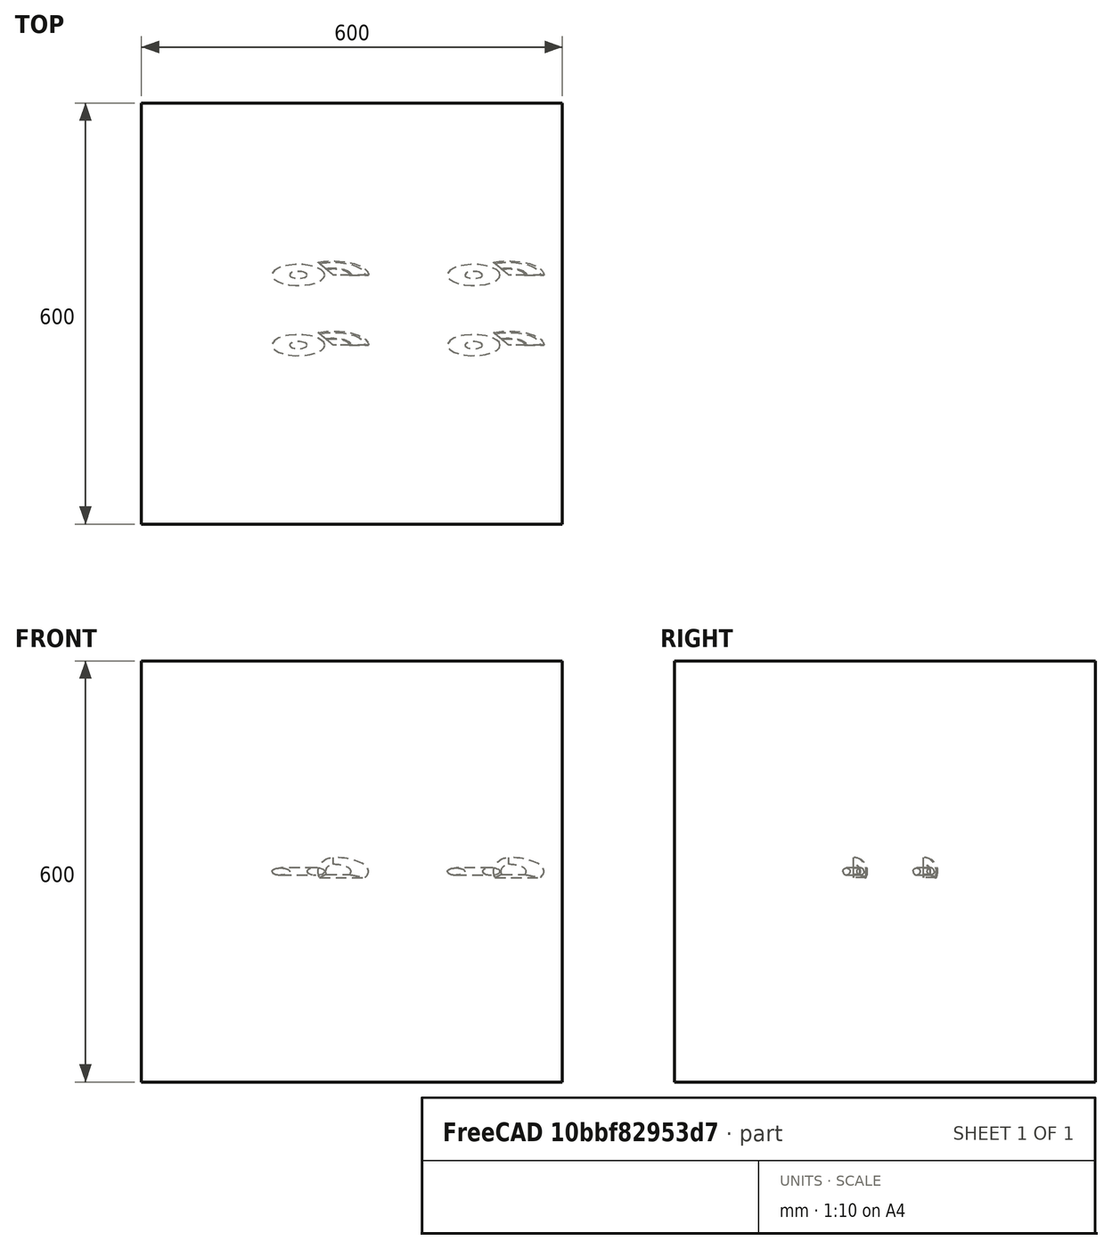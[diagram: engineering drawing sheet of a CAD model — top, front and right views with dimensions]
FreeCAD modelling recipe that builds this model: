
FCSTD DOCUMENT  (FreeCAD 0.19RUnknown)
Label: arrayTest-6_scaled
License: All rights reserved
LicenseURL: http://en.wikipedia.org/wiki/All_rights_reserved
objects: App::DocumentObjectGroupPython×1248, Part::FeaturePython×5, App::Part×2, Part::MultiFuse×1
note: 6 computed .brp shape members not serialized (recipe doc carries the construction recipe); baked Part::Feature solids carry a one-line shape summary decoded from their .brp

FEATURE [App::DocumentObjectGroupPython] HALFPI  # scripted group (container) (typed FeaturePython)
  name = HALFPI
  value = pi/2.
FEATURE [App::DocumentObjectGroupPython] PI  # scripted group (container) (typed FeaturePython)
  name = PI
  value = 1.*pi
FEATURE [App::DocumentObjectGroupPython] TWOPI  # scripted group (container) (typed FeaturePython)
  name = TWOPI
  value = 2.*pi
FEATURE [App::DocumentObjectGroupPython] Constants  # scripted group (container) (typed FeaturePython)
  Group = -> [HALFPI,PI,TWOPI]
FEATURE [App::DocumentObjectGroupPython] Variables  # scripted group (container) (typed FeaturePython)
FEATURE [App::DocumentObjectGroupPython] Quantities  # scripted group (container) (typed FeaturePython)
FEATURE [App::DocumentObjectGroupPython] Isotopes  # scripted group (container) (typed FeaturePython)
FEATURE [App::DocumentObjectGroupPython] Elements  # scripted group (container) (typed FeaturePython)
FEATURE [App::DocumentObjectGroupPython] G4Isotopes  # scripted group (container) (typed FeaturePython)
FEATURE [App::DocumentObjectGroupPython] H_element  # scripted group (container) (typed FeaturePython)
  Z = 1
  atom_value = 1.008
  formula = H
  name = H_element
FEATURE [App::DocumentObjectGroupPython] He_element  # scripted group (container) (typed FeaturePython)
  Z = 2
  atom_value = 4.0026
  formula = He
  name = He_element
FEATURE [App::DocumentObjectGroupPython] Li_element  # scripted group (container) (typed FeaturePython)
  Z = 3
  atom_value = 6.94
  formula = Li
  name = Li_element
FEATURE [App::DocumentObjectGroupPython] Be_element  # scripted group (container) (typed FeaturePython)
  Z = 4
  atom_value = 9.01218
  formula = Be
  name = Be_element
FEATURE [App::DocumentObjectGroupPython] B_element  # scripted group (container) (typed FeaturePython)
  Z = 5
  atom_value = 10.81
  formula = B
  name = B_element
FEATURE [App::DocumentObjectGroupPython] C_element  # scripted group (container) (typed FeaturePython)
  Z = 6
  atom_value = 12.011
  formula = C
  name = C_element
FEATURE [App::DocumentObjectGroupPython] N_element  # scripted group (container) (typed FeaturePython)
  Z = 7
  atom_value = 14.007
  formula = N
  name = N_element
FEATURE [App::DocumentObjectGroupPython] O_element  # scripted group (container) (typed FeaturePython)
  Z = 8
  atom_value = 15.999
  formula = O
  name = O_element
FEATURE [App::DocumentObjectGroupPython] F_element  # scripted group (container) (typed FeaturePython)
  Z = 9
  atom_value = 18.9984
  formula = F
  name = F_element
FEATURE [App::DocumentObjectGroupPython] Ne_element  # scripted group (container) (typed FeaturePython)
  Z = 10
  atom_value = 20.1797
  formula = Ne
  name = Ne_element
FEATURE [App::DocumentObjectGroupPython] Na_element  # scripted group (container) (typed FeaturePython)
  Z = 11
  atom_value = 22.9898
  formula = Na
  name = Na_element
FEATURE [App::DocumentObjectGroupPython] Mg_element  # scripted group (container) (typed FeaturePython)
  Z = 12
  atom_value = 24.305
  formula = Mg
  name = Mg_element
FEATURE [App::DocumentObjectGroupPython] Al_element  # scripted group (container) (typed FeaturePython)
  Z = 13
  atom_value = 26.9815
  formula = Al
  name = Al_element
FEATURE [App::DocumentObjectGroupPython] Si_element  # scripted group (container) (typed FeaturePython)
  Z = 14
  atom_value = 28.085
  formula = Si
  name = Si_element
FEATURE [App::DocumentObjectGroupPython] P_element  # scripted group (container) (typed FeaturePython)
  Z = 15
  atom_value = 30.9738
  formula = P
  name = P_element
FEATURE [App::DocumentObjectGroupPython] S_element  # scripted group (container) (typed FeaturePython)
  Z = 16
  atom_value = 32.06
  formula = S
  name = S_element
FEATURE [App::DocumentObjectGroupPython] Cl_element  # scripted group (container) (typed FeaturePython)
  Z = 17
  atom_value = 35.45
  formula = Cl
  name = Cl_element
FEATURE [App::DocumentObjectGroupPython] Ar_element  # scripted group (container) (typed FeaturePython)
  Z = 18
  atom_value = 39.95
  formula = Ar
  name = Ar_element
FEATURE [App::DocumentObjectGroupPython] K_element  # scripted group (container) (typed FeaturePython)
  Z = 19
  atom_value = 39.0983
  formula = K
  name = K_element
FEATURE [App::DocumentObjectGroupPython] Ca_element  # scripted group (container) (typed FeaturePython)
  Z = 20
  atom_value = 40.078
  formula = Ca
  name = Ca_element
FEATURE [App::DocumentObjectGroupPython] Sc_element  # scripted group (container) (typed FeaturePython)
  Z = 21
  atom_value = 44.9559
  formula = Sc
  name = Sc_element
FEATURE [App::DocumentObjectGroupPython] Ti_element  # scripted group (container) (typed FeaturePython)
  Z = 22
  atom_value = 47.867
  formula = Ti
  name = Ti_element
FEATURE [App::DocumentObjectGroupPython] V_element  # scripted group (container) (typed FeaturePython)
  Z = 23
  atom_value = 50.9415
  formula = V
  name = V_element
FEATURE [App::DocumentObjectGroupPython] Cr_element  # scripted group (container) (typed FeaturePython)
  Z = 24
  atom_value = 51.9961
  formula = Cr
  name = Cr_element
FEATURE [App::DocumentObjectGroupPython] Mn_element  # scripted group (container) (typed FeaturePython)
  Z = 25
  atom_value = 54.938
  formula = Mn
  name = Mn_element
FEATURE [App::DocumentObjectGroupPython] Fe_element  # scripted group (container) (typed FeaturePython)
  Z = 26
  atom_value = 55.845
  formula = Fe
  name = Fe_element
FEATURE [App::DocumentObjectGroupPython] Co_element  # scripted group (container) (typed FeaturePython)
  Z = 27
  atom_value = 58.9332
  formula = Co
  name = Co_element
FEATURE [App::DocumentObjectGroupPython] Ni_element  # scripted group (container) (typed FeaturePython)
  Z = 28
  atom_value = 58.6934
  formula = Ni
  name = Ni_element
FEATURE [App::DocumentObjectGroupPython] Cu_element  # scripted group (container) (typed FeaturePython)
  Z = 29
  atom_value = 63.546
  formula = Cu
  name = Cu_element
FEATURE [App::DocumentObjectGroupPython] Zn_element  # scripted group (container) (typed FeaturePython)
  Z = 30
  atom_value = 65.38
  formula = Zn
  name = Zn_element
FEATURE [App::DocumentObjectGroupPython] Ga_element  # scripted group (container) (typed FeaturePython)
  Z = 31
  atom_value = 69.723
  formula = Ga
  name = Ga_element
FEATURE [App::DocumentObjectGroupPython] Ge_element  # scripted group (container) (typed FeaturePython)
  Z = 32
  atom_value = 72.63
  formula = Ge
  name = Ge_element
FEATURE [App::DocumentObjectGroupPython] As_element  # scripted group (container) (typed FeaturePython)
  Z = 33
  atom_value = 74.9216
  formula = As
  name = As_element
FEATURE [App::DocumentObjectGroupPython] Se_element  # scripted group (container) (typed FeaturePython)
  Z = 34
  atom_value = 78.971
  formula = Se
  name = Se_element
FEATURE [App::DocumentObjectGroupPython] Br_element  # scripted group (container) (typed FeaturePython)
  Z = 35
  atom_value = 79.904
  formula = Br
  name = Br_element
FEATURE [App::DocumentObjectGroupPython] Kr_element  # scripted group (container) (typed FeaturePython)
  Z = 36
  atom_value = 83.798
  formula = Kr
  name = Kr_element
FEATURE [App::DocumentObjectGroupPython] Rb_element  # scripted group (container) (typed FeaturePython)
  Z = 37
  atom_value = 85.4678
  formula = Rb
  name = Rb_element
FEATURE [App::DocumentObjectGroupPython] Sr_element  # scripted group (container) (typed FeaturePython)
  Z = 38
  atom_value = 87.62
  formula = Sr
  name = Sr_element
FEATURE [App::DocumentObjectGroupPython] Y_element  # scripted group (container) (typed FeaturePython)
  Z = 39
  atom_value = 88.9058
  formula = Y
  name = Y_element
FEATURE [App::DocumentObjectGroupPython] Zr_element  # scripted group (container) (typed FeaturePython)
  Z = 40
  atom_value = 91.224
  formula = Zr
  name = Zr_element
FEATURE [App::DocumentObjectGroupPython] Nb_element  # scripted group (container) (typed FeaturePython)
  Z = 41
  atom_value = 92.9064
  formula = Nb
  name = Nb_element
FEATURE [App::DocumentObjectGroupPython] Mo_element  # scripted group (container) (typed FeaturePython)
  Z = 42
  atom_value = 95.95
  formula = Mo
  name = Mo_element
FEATURE [App::DocumentObjectGroupPython] Tc_element  # scripted group (container) (typed FeaturePython)
  Z = 43
  atom_value = 97
  formula = Tc
  name = Tc_element
FEATURE [App::DocumentObjectGroupPython] Ru_element  # scripted group (container) (typed FeaturePython)
  Z = 44
  atom_value = 101.07
  formula = Ru
  name = Ru_element
FEATURE [App::DocumentObjectGroupPython] Rh_element  # scripted group (container) (typed FeaturePython)
  Z = 45
  atom_value = 102.905
  formula = Rh
  name = Rh_element
FEATURE [App::DocumentObjectGroupPython] Pd_element  # scripted group (container) (typed FeaturePython)
  Z = 46
  atom_value = 106.42
  formula = Pd
  name = Pd_element
FEATURE [App::DocumentObjectGroupPython] Ag_element  # scripted group (container) (typed FeaturePython)
  Z = 47
  atom_value = 107.868
  formula = Ag
  name = Ag_element
FEATURE [App::DocumentObjectGroupPython] Cd_element  # scripted group (container) (typed FeaturePython)
  Z = 48
  atom_value = 112.414
  formula = Cd
  name = Cd_element
FEATURE [App::DocumentObjectGroupPython] In_element  # scripted group (container) (typed FeaturePython)
  Z = 49
  atom_value = 114.818
  formula = In
  name = In_element
FEATURE [App::DocumentObjectGroupPython] Sn_element  # scripted group (container) (typed FeaturePython)
  Z = 50
  atom_value = 118.71
  formula = Sn
  name = Sn_element
FEATURE [App::DocumentObjectGroupPython] Sb_element  # scripted group (container) (typed FeaturePython)
  Z = 51
  atom_value = 121.76
  formula = Sb
  name = Sb_element
FEATURE [App::DocumentObjectGroupPython] Te_element  # scripted group (container) (typed FeaturePython)
  Z = 52
  atom_value = 127.6
  formula = Te
  name = Te_element
FEATURE [App::DocumentObjectGroupPython] I_element  # scripted group (container) (typed FeaturePython)
  Z = 53
  atom_value = 126.904
  formula = I
  name = I_element
FEATURE [App::DocumentObjectGroupPython] Xe_element  # scripted group (container) (typed FeaturePython)
  Z = 54
  atom_value = 131.293
  formula = Xe
  name = Xe_element
FEATURE [App::DocumentObjectGroupPython] Cs_element  # scripted group (container) (typed FeaturePython)
  Z = 55
  atom_value = 132.905
  formula = Cs
  name = Cs_element
FEATURE [App::DocumentObjectGroupPython] Ba_element  # scripted group (container) (typed FeaturePython)
  Z = 56
  atom_value = 137.327
  formula = Ba
  name = Ba_element
FEATURE [App::DocumentObjectGroupPython] La_element  # scripted group (container) (typed FeaturePython)
  Z = 57
  atom_value = 138.905
  formula = La
  name = La_element
FEATURE [App::DocumentObjectGroupPython] Ce_element  # scripted group (container) (typed FeaturePython)
  Z = 58
  atom_value = 140.116
  formula = Ce
  name = Ce_element
FEATURE [App::DocumentObjectGroupPython] Pr_element  # scripted group (container) (typed FeaturePython)
  Z = 59
  atom_value = 140.908
  formula = Pr
  name = Pr_element
FEATURE [App::DocumentObjectGroupPython] Nd_element  # scripted group (container) (typed FeaturePython)
  Z = 60
  atom_value = 144.242
  formula = Nd
  name = Nd_element
FEATURE [App::DocumentObjectGroupPython] Pm_element  # scripted group (container) (typed FeaturePython)
  Z = 61
  atom_value = 145
  formula = Pm
  name = Pm_element
FEATURE [App::DocumentObjectGroupPython] Sm_element  # scripted group (container) (typed FeaturePython)
  Z = 62
  atom_value = 150.36
  formula = Sm
  name = Sm_element
FEATURE [App::DocumentObjectGroupPython] Eu_element  # scripted group (container) (typed FeaturePython)
  Z = 63
  atom_value = 151.964
  formula = Eu
  name = Eu_element
FEATURE [App::DocumentObjectGroupPython] Gd_element  # scripted group (container) (typed FeaturePython)
  Z = 64
  atom_value = 157.25
  formula = Gd
  name = Gd_element
FEATURE [App::DocumentObjectGroupPython] Tb_element  # scripted group (container) (typed FeaturePython)
  Z = 65
  atom_value = 158.925
  formula = Tb
  name = Tb_element
FEATURE [App::DocumentObjectGroupPython] Dy_element  # scripted group (container) (typed FeaturePython)
  Z = 66
  atom_value = 162.5
  formula = Dy
  name = Dy_element
FEATURE [App::DocumentObjectGroupPython] Ho_element  # scripted group (container) (typed FeaturePython)
  Z = 67
  atom_value = 164.93
  formula = Ho
  name = Ho_element
FEATURE [App::DocumentObjectGroupPython] Er_element  # scripted group (container) (typed FeaturePython)
  Z = 68
  atom_value = 167.259
  formula = Er
  name = Er_element
FEATURE [App::DocumentObjectGroupPython] Tm_element  # scripted group (container) (typed FeaturePython)
  Z = 69
  atom_value = 168.934
  formula = Tm
  name = Tm_element
FEATURE [App::DocumentObjectGroupPython] Yb_element  # scripted group (container) (typed FeaturePython)
  Z = 70
  atom_value = 173.045
  formula = Yb
  name = Yb_element
FEATURE [App::DocumentObjectGroupPython] Lu_element  # scripted group (container) (typed FeaturePython)
  Z = 71
  atom_value = 174.967
  formula = Lu
  name = Lu_element
FEATURE [App::DocumentObjectGroupPython] Hf_element  # scripted group (container) (typed FeaturePython)
  Z = 72
  atom_value = 178.49
  formula = Hf
  name = Hf_element
FEATURE [App::DocumentObjectGroupPython] Ta_element  # scripted group (container) (typed FeaturePython)
  Z = 73
  atom_value = 180.948
  formula = Ta
  name = Ta_element
FEATURE [App::DocumentObjectGroupPython] W_element  # scripted group (container) (typed FeaturePython)
  Z = 74
  atom_value = 183.84
  formula = W
  name = W_element
FEATURE [App::DocumentObjectGroupPython] Re_element  # scripted group (container) (typed FeaturePython)
  Z = 75
  atom_value = 186.207
  formula = Re
  name = Re_element
FEATURE [App::DocumentObjectGroupPython] Os_element  # scripted group (container) (typed FeaturePython)
  Z = 76
  atom_value = 190.23
  formula = Os
  name = Os_element
FEATURE [App::DocumentObjectGroupPython] Ir_element  # scripted group (container) (typed FeaturePython)
  Z = 77
  atom_value = 192.217
  formula = Ir
  name = Ir_element
FEATURE [App::DocumentObjectGroupPython] Pt_element  # scripted group (container) (typed FeaturePython)
  Z = 78
  atom_value = 195.084
  formula = Pt
  name = Pt_element
FEATURE [App::DocumentObjectGroupPython] Au_element  # scripted group (container) (typed FeaturePython)
  Z = 79
  atom_value = 196.967
  formula = Au
  name = Au_element
FEATURE [App::DocumentObjectGroupPython] Hg_element  # scripted group (container) (typed FeaturePython)
  Z = 80
  atom_value = 200.592
  formula = Hg
  name = Hg_element
FEATURE [App::DocumentObjectGroupPython] Tl_element  # scripted group (container) (typed FeaturePython)
  Z = 81
  atom_value = 204.38
  formula = Tl
  name = Tl_element
FEATURE [App::DocumentObjectGroupPython] Pb_element  # scripted group (container) (typed FeaturePython)
  Z = 82
  atom_value = 207.2
  formula = Pb
  name = Pb_element
FEATURE [App::DocumentObjectGroupPython] Bi_element  # scripted group (container) (typed FeaturePython)
  Z = 83
  atom_value = 208.98
  formula = Bi
  name = Bi_element
FEATURE [App::DocumentObjectGroupPython] Po_element  # scripted group (container) (typed FeaturePython)
  Z = 84
  atom_value = 209
  formula = Po
  name = Po_element
FEATURE [App::DocumentObjectGroupPython] At_element  # scripted group (container) (typed FeaturePython)
  Z = 85
  atom_value = 210
  formula = At
  name = At_element
FEATURE [App::DocumentObjectGroupPython] Rn_element  # scripted group (container) (typed FeaturePython)
  Z = 86
  atom_value = 222
  formula = Rn
  name = Rn_element
FEATURE [App::DocumentObjectGroupPython] Fr_element  # scripted group (container) (typed FeaturePython)
  Z = 87
  atom_value = 223
  formula = Fr
  name = Fr_element
FEATURE [App::DocumentObjectGroupPython] Ra_element  # scripted group (container) (typed FeaturePython)
  Z = 88
  atom_value = 226
  formula = Ra
  name = Ra_element
FEATURE [App::DocumentObjectGroupPython] Ac_element  # scripted group (container) (typed FeaturePython)
  Z = 89
  atom_value = 227
  formula = Ac
  name = Ac_element
FEATURE [App::DocumentObjectGroupPython] Th_element  # scripted group (container) (typed FeaturePython)
  Z = 90
  atom_value = 232.038
  formula = Th
  name = Th_element
FEATURE [App::DocumentObjectGroupPython] Pa_element  # scripted group (container) (typed FeaturePython)
  Z = 91
  atom_value = 231.036
  formula = Pa
  name = Pa_element
FEATURE [App::DocumentObjectGroupPython] U_element  # scripted group (container) (typed FeaturePython)
  Z = 92
  atom_value = 238.029
  formula = U
  name = U_element
FEATURE [App::DocumentObjectGroupPython] Np_element  # scripted group (container) (typed FeaturePython)
  Z = 93
  atom_value = 237
  formula = Np
  name = Np_element
FEATURE [App::DocumentObjectGroupPython] Pu_element  # scripted group (container) (typed FeaturePython)
  Z = 94
  atom_value = 244
  formula = Pu
  name = Pu_element
FEATURE [App::DocumentObjectGroupPython] Am_element  # scripted group (container) (typed FeaturePython)
  Z = 95
  atom_value = 243
  formula = Am
  name = Am_element
FEATURE [App::DocumentObjectGroupPython] Cm_element  # scripted group (container) (typed FeaturePython)
  Z = 96
  atom_value = 247
  formula = Cm
  name = Cm_element
FEATURE [App::DocumentObjectGroupPython] Bk_element  # scripted group (container) (typed FeaturePython)
  Z = 97
  atom_value = 247
  formula = Bk
  name = Bk_element
FEATURE [App::DocumentObjectGroupPython] Cf_element  # scripted group (container) (typed FeaturePython)
  Z = 98
  atom_value = 251
  formula = Cf
  name = Cf_element
FEATURE [App::DocumentObjectGroupPython] G4Elements  # scripted group (container) (typed FeaturePython)
  Group = -> [H_element,He_element,Li_element,Be_element,B_element,C_element,N_element,O_element,F_element,Ne_element,Na_element,Mg_element,Al_element,Si_element,P_element,S_element,Cl_element,Ar_element,K_element,Ca_element,Sc_element,Ti_element,V_element,Cr_element,Mn_element,Fe_element,Co_element,Ni_element,Cu_element,Zn_element,Ga_element,Ge_element,As_element,Se_element,Br_element,Kr_element,Rb_element,+61 more]
FEATURE [App::DocumentObjectGroupPython] H_element001  label="H_element : 0.101"  # scripted group (container) (typed FeaturePython)
  n = 0.101327
FEATURE [App::DocumentObjectGroupPython] C_element001  label="C_element : 0.775"  # scripted group (container) (typed FeaturePython)
  n = 0.7755
FEATURE [App::DocumentObjectGroupPython] N_element001  label="N_element : 0.035"  # scripted group (container) (typed FeaturePython)
  n = 0.035057
FEATURE [App::DocumentObjectGroupPython] O_element001  label="O_element : 0.052"  # scripted group (container) (typed FeaturePython)
  n = 0.0523159
FEATURE [App::DocumentObjectGroupPython] F_element001  label="F_element : 0.017"  # scripted group (container) (typed FeaturePython)
  n = 0.017422
FEATURE [App::DocumentObjectGroupPython] Ca_element001  label="Ca_element : 0.018"  # scripted group (container) (typed FeaturePython)
  n = 0.018378
FEATURE [App::DocumentObjectGroupPython] G4_A_150_TISSUE  label="G4_A-150_TISSUE"  # scripted group (container) (typed FeaturePython)
  Dunit = g/cm3
  Dvalue = 1.127
  Group = -> [H_element001,C_element001,N_element001,O_element001,F_element001,Ca_element001]
  conduct = 2
  density = 1
  expand = 3
  formula = G4_A-150_TISSUE
  name = G4_A-150_TISSUE
  specific = 4
FEATURE [App::DocumentObjectGroupPython] C_element002  label="C_element : 3"  # scripted group (container) (typed FeaturePython)
  n = 3
  ref = C_element
FEATURE [App::DocumentObjectGroupPython] H_element002  label="H_element : 6"  # scripted group (container) (typed FeaturePython)
  n = 6
  ref = H_element
FEATURE [App::DocumentObjectGroupPython] O_element002  label="O_element : 1"  # scripted group (container) (typed FeaturePython)
  n = 1
  ref = O_element
FEATURE [App::DocumentObjectGroupPython] G4_ACETONE  # scripted group (container) (typed FeaturePython)
  Dunit = g/cm3
  Dvalue = 0.7899
  Group = -> [C_element002,H_element002,O_element002]
  conduct = 2
  density = 1
  expand = 3
  formula = G4_ACETONE
  name = G4_ACETONE
  specific = 4
FEATURE [App::DocumentObjectGroupPython] C_element003  label="C_element : 2"  # scripted group (container) (typed FeaturePython)
  n = 2
  ref = C_element
FEATURE [App::DocumentObjectGroupPython] H_element003  label="H_element : 2"  # scripted group (container) (typed FeaturePython)
  n = 2
  ref = H_element
FEATURE [App::DocumentObjectGroupPython] G4_ACETYLENE  # scripted group (container) (typed FeaturePython)
  Dunit = g/cm3
  Dvalue = 0.0010967
  Group = -> [C_element003,H_element003]
  conduct = 2
  density = 1
  expand = 3
  formula = G4_ACETYLENE
  name = G4_ACETYLENE
  specific = 4
FEATURE [App::DocumentObjectGroupPython] C_element004  label="C_element : 5"  # scripted group (container) (typed FeaturePython)
  n = 5
  ref = C_element
FEATURE [App::DocumentObjectGroupPython] H_element004  label="H_element : 5"  # scripted group (container) (typed FeaturePython)
  n = 5
  ref = H_element
FEATURE [App::DocumentObjectGroupPython] N_element002  label="N_element : 5"  # scripted group (container) (typed FeaturePython)
  n = 5
  ref = N_element
FEATURE [App::DocumentObjectGroupPython] G4_ADENINE  # scripted group (container) (typed FeaturePython)
  Dunit = g/cm3
  Dvalue = 1.6
  Group = -> [C_element004,H_element004,N_element002]
  conduct = 2
  density = 1
  expand = 3
  formula = G4_ADENINE
  name = G4_ADENINE
  specific = 4
FEATURE [App::DocumentObjectGroupPython] H_element005  label="H_element : 0.114"  # scripted group (container) (typed FeaturePython)
  n = 0.114
FEATURE [App::DocumentObjectGroupPython] C_element005  label="C_element : 0.598"  # scripted group (container) (typed FeaturePython)
  n = 0.598
FEATURE [App::DocumentObjectGroupPython] N_element003  label="N_element : 0.007"  # scripted group (container) (typed FeaturePython)
  n = 0.007
FEATURE [App::DocumentObjectGroupPython] O_element003  label="O_element : 0.278"  # scripted group (container) (typed FeaturePython)
  n = 0.278
FEATURE [App::DocumentObjectGroupPython] Na_element001  label="Na_element : 0.001"  # scripted group (container) (typed FeaturePython)
  n = 0.001
FEATURE [App::DocumentObjectGroupPython] S_element001  label="S_element : 0.001"  # scripted group (container) (typed FeaturePython)
  n = 0.001
FEATURE [App::DocumentObjectGroupPython] Cl_element001  label="Cl_element : 0.001"  # scripted group (container) (typed FeaturePython)
  n = 0.001
FEATURE [App::DocumentObjectGroupPython] G4_ADIPOSE_TISSUE_ICRP  # scripted group (container) (typed FeaturePython)
  Dunit = g/cm3
  Dvalue = 0.95
  Group = -> [H_element005,C_element005,N_element003,O_element003,Na_element001,S_element001,Cl_element001]
  conduct = 2
  density = 1
  expand = 3
  formula = G4_ADIPOSE_TISSUE_ICRP
  name = G4_ADIPOSE_TISSUE_ICRP
  specific = 4
FEATURE [App::DocumentObjectGroupPython] C_element006  label="C_element : 0.000"  # scripted group (container) (typed FeaturePython)
  n = 0.000124
FEATURE [App::DocumentObjectGroupPython] N_element004  label="N_element : 0.755"  # scripted group (container) (typed FeaturePython)
  n = 0.755268
FEATURE [App::DocumentObjectGroupPython] O_element004  label="O_element : 0.232"  # scripted group (container) (typed FeaturePython)
  n = 0.231781
FEATURE [App::DocumentObjectGroupPython] Ar_element001  label="Ar_element : 0.013"  # scripted group (container) (typed FeaturePython)
  n = 0.012827
FEATURE [App::DocumentObjectGroupPython] G4_AIR  # scripted group (container) (typed FeaturePython)
  Dunit = g/cm3
  Dvalue = 0.00120479
  Group = -> [C_element006,N_element004,O_element004,Ar_element001]
  conduct = 2
  density = 1
  expand = 3
  formula = G4_AIR
  name = G4_AIR
  specific = 4
FEATURE [App::DocumentObjectGroupPython] C_element007  label="C_element : 006"  # scripted group (container) (typed FeaturePython)
  n = 3
  ref = C_element
FEATURE [App::DocumentObjectGroupPython] H_element006  label="H_element : 7"  # scripted group (container) (typed FeaturePython)
  n = 7
  ref = H_element
FEATURE [App::DocumentObjectGroupPython] N_element005  label="N_element : 1"  # scripted group (container) (typed FeaturePython)
  n = 1
  ref = N_element
FEATURE [App::DocumentObjectGroupPython] O_element005  label="O_element : 2"  # scripted group (container) (typed FeaturePython)
  n = 2
  ref = O_element
FEATURE [App::DocumentObjectGroupPython] G4_ALANINE  # scripted group (container) (typed FeaturePython)
  Dunit = g/cm3
  Dvalue = 1.42
  Group = -> [C_element007,H_element006,N_element005,O_element005]
  conduct = 2
  density = 1
  expand = 3
  formula = G4_ALANINE
  name = G4_ALANINE
  specific = 4
FEATURE [App::DocumentObjectGroupPython] Al_element001  label="Al_element : 2"  # scripted group (container) (typed FeaturePython)
  n = 2
  ref = Al_element
FEATURE [App::DocumentObjectGroupPython] O_element006  label="O_element : 3"  # scripted group (container) (typed FeaturePython)
  n = 3
  ref = O_element
FEATURE [App::DocumentObjectGroupPython] G4_ALUMINUM_OXIDE  # scripted group (container) (typed FeaturePython)
  Dunit = g/cm3
  Dvalue = 3.97
  Group = -> [Al_element001,O_element006]
  conduct = 2
  density = 1
  expand = 3
  formula = G4_ALUMINUM_OXIDE
  name = G4_ALUMINUM_OXIDE
  specific = 4
FEATURE [App::DocumentObjectGroupPython] H_element007  label="H_element : 0.106"  # scripted group (container) (typed FeaturePython)
  n = 0.10593
FEATURE [App::DocumentObjectGroupPython] C_element008  label="C_element : 0.789"  # scripted group (container) (typed FeaturePython)
  n = 0.788974
FEATURE [App::DocumentObjectGroupPython] O_element007  label="O_element : 0.105"  # scripted group (container) (typed FeaturePython)
  n = 0.105096
FEATURE [App::DocumentObjectGroupPython] G4_AMBER  # scripted group (container) (typed FeaturePython)
  Dunit = g/cm3
  Dvalue = 1.1
  Group = -> [H_element007,C_element008,O_element007]
  conduct = 2
  density = 1
  expand = 3
  formula = G4_AMBER
  name = G4_AMBER
  specific = 4
FEATURE [App::DocumentObjectGroupPython] N_element006  label="N_element : 006"  # scripted group (container) (typed FeaturePython)
  n = 1
  ref = N_element
FEATURE [App::DocumentObjectGroupPython] H_element008  label="H_element : 3"  # scripted group (container) (typed FeaturePython)
  n = 3
  ref = H_element
FEATURE [App::DocumentObjectGroupPython] G4_AMMONIA  # scripted group (container) (typed FeaturePython)
  Dunit = g/cm3
  Dvalue = 0.000826019
  Group = -> [N_element006,H_element008]
  conduct = 2
  density = 1
  expand = 3
  formula = G4_AMMONIA
  name = G4_AMMONIA
  specific = 4
FEATURE [App::DocumentObjectGroupPython] C_element009  label="C_element : 6"  # scripted group (container) (typed FeaturePython)
  n = 6
  ref = C_element
FEATURE [App::DocumentObjectGroupPython] H_element009  label="H_element : 008"  # scripted group (container) (typed FeaturePython)
  n = 7
  ref = H_element
FEATURE [App::DocumentObjectGroupPython] N_element007  label="N_element : 007"  # scripted group (container) (typed FeaturePython)
  n = 1
  ref = N_element
FEATURE [App::DocumentObjectGroupPython] G4_ANILINE  # scripted group (container) (typed FeaturePython)
  Dunit = g/cm3
  Dvalue = 1.0235
  Group = -> [C_element009,H_element009,N_element007]
  conduct = 2
  density = 1
  expand = 3
  formula = G4_ANILINE
  name = G4_ANILINE
  specific = 4
FEATURE [App::DocumentObjectGroupPython] C_element010  label="C_element : 14"  # scripted group (container) (typed FeaturePython)
  n = 14
  ref = C_element
FEATURE [App::DocumentObjectGroupPython] H_element010  label="H_element : 10"  # scripted group (container) (typed FeaturePython)
  n = 10
  ref = H_element
FEATURE [App::DocumentObjectGroupPython] G4_ANTHRACENE  # scripted group (container) (typed FeaturePython)
  Dunit = g/cm3
  Dvalue = 1.283
  Group = -> [C_element010,H_element010]
  conduct = 2
  density = 1
  expand = 3
  formula = G4_ANTHRACENE
  name = G4_ANTHRACENE
  specific = 4
FEATURE [App::DocumentObjectGroupPython] H_element011  label="H_element : 0.065"  # scripted group (container) (typed FeaturePython)
  n = 0.0654709
FEATURE [App::DocumentObjectGroupPython] C_element011  label="C_element : 0.537"  # scripted group (container) (typed FeaturePython)
  n = 0.536944
FEATURE [App::DocumentObjectGroupPython] N_element008  label="N_element : 0.021"  # scripted group (container) (typed FeaturePython)
  n = 0.0215
FEATURE [App::DocumentObjectGroupPython] O_element008  label="O_element : 0.032"  # scripted group (container) (typed FeaturePython)
  n = 0.032085
FEATURE [App::DocumentObjectGroupPython] F_element002  label="F_element : 0.167"  # scripted group (container) (typed FeaturePython)
  n = 0.167411
FEATURE [App::DocumentObjectGroupPython] Ca_element002  label="Ca_element : 0.177"  # scripted group (container) (typed FeaturePython)
  n = 0.176589
FEATURE [App::DocumentObjectGroupPython] G4_B_100_BONE  label="G4_B-100_BONE"  # scripted group (container) (typed FeaturePython)
  Dunit = g/cm3
  Dvalue = 1.45
  Group = -> [H_element011,C_element011,N_element008,O_element008,F_element002,Ca_element002]
  conduct = 2
  density = 1
  expand = 3
  formula = G4_B-100_BONE
  name = G4_B-100_BONE
  specific = 4
FEATURE [App::DocumentObjectGroupPython] H_element012  label="H_element : 0.057"  # scripted group (container) (typed FeaturePython)
  n = 0.057441
FEATURE [App::DocumentObjectGroupPython] C_element012  label="C_element : 0.790"  # scripted group (container) (typed FeaturePython)
  n = 0.774591
FEATURE [App::DocumentObjectGroupPython] O_element009  label="O_element : 0.168"  # scripted group (container) (typed FeaturePython)
  n = 0.167968
FEATURE [App::DocumentObjectGroupPython] G4_BAKELITE  # scripted group (container) (typed FeaturePython)
  Dunit = g/cm3
  Dvalue = 1.25
  Group = -> [H_element012,C_element012,O_element009]
  conduct = 2
  density = 1
  expand = 3
  formula = G4_BAKELITE
  name = G4_BAKELITE
  specific = 4
FEATURE [App::DocumentObjectGroupPython] Ba_element001  label="Ba_element : 1"  # scripted group (container) (typed FeaturePython)
  n = 1
  ref = Ba_element
FEATURE [App::DocumentObjectGroupPython] F_element003  label="F_element : 2"  # scripted group (container) (typed FeaturePython)
  n = 2
  ref = F_element
FEATURE [App::DocumentObjectGroupPython] G4_BARIUM_FLUORIDE  # scripted group (container) (typed FeaturePython)
  Dunit = g/cm3
  Dvalue = 4.89
  Group = -> [Ba_element001,F_element003]
  conduct = 2
  density = 1
  expand = 3
  formula = G4_BARIUM_FLUORIDE
  name = G4_BARIUM_FLUORIDE
  specific = 4
FEATURE [App::DocumentObjectGroupPython] Ba_element002  label="Ba_element : 002"  # scripted group (container) (typed FeaturePython)
  n = 1
  ref = Ba_element
FEATURE [App::DocumentObjectGroupPython] S_element002  label="S_element : 1"  # scripted group (container) (typed FeaturePython)
  n = 1
  ref = S_element
FEATURE [App::DocumentObjectGroupPython] O_element010  label="O_element : 4"  # scripted group (container) (typed FeaturePython)
  n = 4
  ref = O_element
FEATURE [App::DocumentObjectGroupPython] G4_BARIUM_SULFATE  # scripted group (container) (typed FeaturePython)
  Dunit = g/cm3
  Dvalue = 4.5
  Group = -> [Ba_element002,S_element002,O_element010]
  conduct = 2
  density = 1
  expand = 3
  formula = G4_BARIUM_SULFATE
  name = G4_BARIUM_SULFATE
  specific = 4
FEATURE [App::DocumentObjectGroupPython] C_element013  label="C_element : 007"  # scripted group (container) (typed FeaturePython)
  n = 6
  ref = C_element
FEATURE [App::DocumentObjectGroupPython] H_element013  label="H_element : 009"  # scripted group (container) (typed FeaturePython)
  n = 6
  ref = H_element
FEATURE [App::DocumentObjectGroupPython] G4_BENZENE  # scripted group (container) (typed FeaturePython)
  Dunit = g/cm3
  Dvalue = 0.87865
  Group = -> [C_element013,H_element013]
  conduct = 2
  density = 1
  expand = 3
  formula = G4_BENZENE
  name = G4_BENZENE
  specific = 4
FEATURE [App::DocumentObjectGroupPython] Be_element001  label="Be_element : 1"  # scripted group (container) (typed FeaturePython)
  n = 1
  ref = Be_element
FEATURE [App::DocumentObjectGroupPython] O_element011  label="O_element : 005"  # scripted group (container) (typed FeaturePython)
  n = 1
  ref = O_element
FEATURE [App::DocumentObjectGroupPython] G4_BERYLLIUM_OXIDE  # scripted group (container) (typed FeaturePython)
  Dunit = g/cm3
  Dvalue = 3.01
  Group = -> [Be_element001,O_element011]
  conduct = 2
  density = 1
  expand = 3
  formula = G4_BERYLLIUM_OXIDE
  name = G4_BERYLLIUM_OXIDE
  specific = 4
FEATURE [App::DocumentObjectGroupPython] Bi_element001  label="Bi_element : 4"  # scripted group (container) (typed FeaturePython)
  n = 4
  ref = Bi_element
FEATURE [App::DocumentObjectGroupPython] Ge_element001  label="Ge_element : 3"  # scripted group (container) (typed FeaturePython)
  n = 3
  ref = Ge_element
FEATURE [App::DocumentObjectGroupPython] O_element012  label="O_element : 12"  # scripted group (container) (typed FeaturePython)
  n = 12
  ref = O_element
FEATURE [App::DocumentObjectGroupPython] G4_BGO  # scripted group (container) (typed FeaturePython)
  Dunit = g/cm3
  Dvalue = 7.13
  Group = -> [Bi_element001,Ge_element001,O_element012]
  conduct = 2
  density = 1
  expand = 3
  formula = G4_BGO
  name = G4_BGO
  specific = 4
FEATURE [App::DocumentObjectGroupPython] H_element014  label="H_element : 0.102"  # scripted group (container) (typed FeaturePython)
  n = 0.102
FEATURE [App::DocumentObjectGroupPython] C_element014  label="C_element : 0.110"  # scripted group (container) (typed FeaturePython)
  n = 0.11
FEATURE [App::DocumentObjectGroupPython] N_element009  label="N_element : 0.033"  # scripted group (container) (typed FeaturePython)
  n = 0.033
FEATURE [App::DocumentObjectGroupPython] O_element013  label="O_element : 0.745"  # scripted group (container) (typed FeaturePython)
  n = 0.745
FEATURE [App::DocumentObjectGroupPython] Na_element002  label="Na_element : 0.002"  # scripted group (container) (typed FeaturePython)
  n = 0.001
FEATURE [App::DocumentObjectGroupPython] P_element001  label="P_element : 0.001"  # scripted group (container) (typed FeaturePython)
  n = 0.001
FEATURE [App::DocumentObjectGroupPython] S_element003  label="S_element : 0.002"  # scripted group (container) (typed FeaturePython)
  n = 0.002
FEATURE [App::DocumentObjectGroupPython] Cl_element002  label="Cl_element : 0.003"  # scripted group (container) (typed FeaturePython)
  n = 0.003
FEATURE [App::DocumentObjectGroupPython] K_element001  label="K_element : 0.002"  # scripted group (container) (typed FeaturePython)
  n = 0.002
FEATURE [App::DocumentObjectGroupPython] Fe_element001  label="Fe_element : 0.001"  # scripted group (container) (typed FeaturePython)
  n = 0.001
FEATURE [App::DocumentObjectGroupPython] G4_BLOOD_ICRP  # scripted group (container) (typed FeaturePython)
  Dunit = g/cm3
  Dvalue = 1.06
  Group = -> [H_element014,C_element014,N_element009,O_element013,Na_element002,P_element001,S_element003,Cl_element002,K_element001,Fe_element001]
  conduct = 2
  density = 1
  expand = 3
  formula = G4_BLOOD_ICRP
  name = G4_BLOOD_ICRP
  specific = 4
FEATURE [App::DocumentObjectGroupPython] H_element015  label="H_element : 0.064"  # scripted group (container) (typed FeaturePython)
  n = 0.064
FEATURE [App::DocumentObjectGroupPython] C_element015  label="C_element : 0.278"  # scripted group (container) (typed FeaturePython)
  n = 0.278
FEATURE [App::DocumentObjectGroupPython] N_element010  label="N_element : 0.027"  # scripted group (container) (typed FeaturePython)
  n = 0.027
FEATURE [App::DocumentObjectGroupPython] O_element014  label="O_element : 0.410"  # scripted group (container) (typed FeaturePython)
  n = 0.41
FEATURE [App::DocumentObjectGroupPython] Mg_element001  label="Mg_element : 0.002"  # scripted group (container) (typed FeaturePython)
  n = 0.002
FEATURE [App::DocumentObjectGroupPython] P_element002  label="P_element : 0.070"  # scripted group (container) (typed FeaturePython)
  n = 0.07
FEATURE [App::DocumentObjectGroupPython] S_element004  label="S_element : 0.003"  # scripted group (container) (typed FeaturePython)
  n = 0.002
FEATURE [App::DocumentObjectGroupPython] Ca_element003  label="Ca_element : 0.147"  # scripted group (container) (typed FeaturePython)
  n = 0.147
FEATURE [App::DocumentObjectGroupPython] G4_BONE_COMPACT_ICRU  # scripted group (container) (typed FeaturePython)
  Dunit = g/cm3
  Dvalue = 1.85
  Group = -> [H_element015,C_element015,N_element010,O_element014,Mg_element001,P_element002,S_element004,Ca_element003]
  conduct = 2
  density = 1
  expand = 3
  formula = G4_BONE_COMPACT_ICRU
  name = G4_BONE_COMPACT_ICRU
  specific = 4
FEATURE [App::DocumentObjectGroupPython] H_element016  label="H_element : 0.034"  # scripted group (container) (typed FeaturePython)
  n = 0.034
FEATURE [App::DocumentObjectGroupPython] C_element016  label="C_element : 0.155"  # scripted group (container) (typed FeaturePython)
  n = 0.155
FEATURE [App::DocumentObjectGroupPython] N_element011  label="N_element : 0.042"  # scripted group (container) (typed FeaturePython)
  n = 0.042
FEATURE [App::DocumentObjectGroupPython] O_element015  label="O_element : 0.435"  # scripted group (container) (typed FeaturePython)
  n = 0.435
FEATURE [App::DocumentObjectGroupPython] Na_element003  label="Na_element : 0.003"  # scripted group (container) (typed FeaturePython)
  n = 0.001
FEATURE [App::DocumentObjectGroupPython] Mg_element002  label="Mg_element : 0.003"  # scripted group (container) (typed FeaturePython)
  n = 0.002
FEATURE [App::DocumentObjectGroupPython] P_element003  label="P_element : 0.103"  # scripted group (container) (typed FeaturePython)
  n = 0.103
FEATURE [App::DocumentObjectGroupPython] S_element005  label="S_element : 0.004"  # scripted group (container) (typed FeaturePython)
  n = 0.003
FEATURE [App::DocumentObjectGroupPython] Ca_element004  label="Ca_element : 0.225"  # scripted group (container) (typed FeaturePython)
  n = 0.225
FEATURE [App::DocumentObjectGroupPython] G4_BONE_CORTICAL_ICRP  # scripted group (container) (typed FeaturePython)
  Dunit = g/cm3
  Dvalue = 1.92
  Group = -> [H_element016,C_element016,N_element011,O_element015,Na_element003,Mg_element002,P_element003,S_element005,Ca_element004]
  conduct = 2
  density = 1
  expand = 3
  formula = G4_BONE_CORTICAL_ICRP
  name = G4_BONE_CORTICAL_ICRP
  specific = 4
FEATURE [App::DocumentObjectGroupPython] B_element001  label="B_element : 4"  # scripted group (container) (typed FeaturePython)
  n = 4
  ref = B_element
FEATURE [App::DocumentObjectGroupPython] C_element017  label="C_element : 1"  # scripted group (container) (typed FeaturePython)
  n = 1
  ref = C_element
FEATURE [App::DocumentObjectGroupPython] G4_BORON_CARBIDE  # scripted group (container) (typed FeaturePython)
  Dunit = g/cm3
  Dvalue = 2.52
  Group = -> [B_element001,C_element017]
  conduct = 2
  density = 1
  expand = 3
  formula = G4_BORON_CARBIDE
  name = G4_BORON_CARBIDE
  specific = 4
FEATURE [App::DocumentObjectGroupPython] B_element002  label="B_element : 2"  # scripted group (container) (typed FeaturePython)
  n = 2
  ref = B_element
FEATURE [App::DocumentObjectGroupPython] O_element016  label="O_element : 006"  # scripted group (container) (typed FeaturePython)
  n = 3
  ref = O_element
FEATURE [App::DocumentObjectGroupPython] G4_BORON_OXIDE  # scripted group (container) (typed FeaturePython)
  Dunit = g/cm3
  Dvalue = 1.812
  Group = -> [B_element002,O_element016]
  conduct = 2
  density = 1
  expand = 3
  formula = G4_BORON_OXIDE
  name = G4_BORON_OXIDE
  specific = 4
FEATURE [App::DocumentObjectGroupPython] H_element017  label="H_element : 0.107"  # scripted group (container) (typed FeaturePython)
  n = 0.107
FEATURE [App::DocumentObjectGroupPython] C_element018  label="C_element : 0.145"  # scripted group (container) (typed FeaturePython)
  n = 0.145
FEATURE [App::DocumentObjectGroupPython] N_element012  label="N_element : 0.022"  # scripted group (container) (typed FeaturePython)
  n = 0.022
FEATURE [App::DocumentObjectGroupPython] O_element017  label="O_element : 0.712"  # scripted group (container) (typed FeaturePython)
  n = 0.712
FEATURE [App::DocumentObjectGroupPython] Na_element004  label="Na_element : 0.004"  # scripted group (container) (typed FeaturePython)
  n = 0.002
FEATURE [App::DocumentObjectGroupPython] P_element004  label="P_element : 0.004"  # scripted group (container) (typed FeaturePython)
  n = 0.004
FEATURE [App::DocumentObjectGroupPython] S_element006  label="S_element : 0.005"  # scripted group (container) (typed FeaturePython)
  n = 0.002
FEATURE [App::DocumentObjectGroupPython] Cl_element003  label="Cl_element : 0.004"  # scripted group (container) (typed FeaturePython)
  n = 0.003
FEATURE [App::DocumentObjectGroupPython] K_element002  label="K_element : 0.003"  # scripted group (container) (typed FeaturePython)
  n = 0.003
FEATURE [App::DocumentObjectGroupPython] G4_BRAIN_ICRP  # scripted group (container) (typed FeaturePython)
  Dunit = g/cm3
  Dvalue = 1.04
  Group = -> [H_element017,C_element018,N_element012,O_element017,Na_element004,P_element004,S_element006,Cl_element003,K_element002]
  conduct = 2
  density = 1
  expand = 3
  formula = G4_BRAIN_ICRP
  name = G4_BRAIN_ICRP
  specific = 4
FEATURE [App::DocumentObjectGroupPython] C_element019  label="C_element : 4"  # scripted group (container) (typed FeaturePython)
  n = 4
  ref = C_element
FEATURE [App::DocumentObjectGroupPython] H_element018  label="H_element : 010"  # scripted group (container) (typed FeaturePython)
  n = 10
  ref = H_element
FEATURE [App::DocumentObjectGroupPython] G4_BUTANE  # scripted group (container) (typed FeaturePython)
  Dunit = g/cm3
  Dvalue = 0.00249343
  Group = -> [C_element019,H_element018]
  conduct = 2
  density = 1
  expand = 3
  formula = G4_BUTANE
  name = G4_BUTANE
  specific = 4
FEATURE [App::DocumentObjectGroupPython] C_element020  label="C_element : 008"  # scripted group (container) (typed FeaturePython)
  n = 4
  ref = C_element
FEATURE [App::DocumentObjectGroupPython] H_element019  label="H_element : 011"  # scripted group (container) (typed FeaturePython)
  n = 10
  ref = H_element
FEATURE [App::DocumentObjectGroupPython] O_element018  label="O_element : 007"  # scripted group (container) (typed FeaturePython)
  n = 1
  ref = O_element
FEATURE [App::DocumentObjectGroupPython] G4_N_BUTYL_ALCOHOL  label="G4_N-BUTYL_ALCOHOL"  # scripted group (container) (typed FeaturePython)
  Dunit = g/cm3
  Dvalue = 0.8098
  Group = -> [C_element020,H_element019,O_element018]
  conduct = 2
  density = 1
  expand = 3
  formula = G4_N-BUTYL_ALCOHOL
  name = G4_N-BUTYL_ALCOHOL
  specific = 4
FEATURE [App::DocumentObjectGroupPython] H_element020  label="H_element : 0.025"  # scripted group (container) (typed FeaturePython)
  n = 0.02468
FEATURE [App::DocumentObjectGroupPython] C_element021  label="C_element : 0.502"  # scripted group (container) (typed FeaturePython)
  n = 0.501611
FEATURE [App::DocumentObjectGroupPython] O_element019  label="O_element : 0.005"  # scripted group (container) (typed FeaturePython)
  n = 0.004527
FEATURE [App::DocumentObjectGroupPython] F_element004  label="F_element : 0.465"  # scripted group (container) (typed FeaturePython)
  n = 0.465209
FEATURE [App::DocumentObjectGroupPython] Si_element001  label="Si_element : 0.004"  # scripted group (container) (typed FeaturePython)
  n = 0.003973
FEATURE [App::DocumentObjectGroupPython] G4_C_552  label="G4_C-552"  # scripted group (container) (typed FeaturePython)
  Dunit = g/cm3
  Dvalue = 1.76
  Group = -> [H_element020,C_element021,O_element019,F_element004,Si_element001]
  conduct = 2
  density = 1
  expand = 3
  formula = G4_C-552
  name = G4_C-552
  specific = 4
FEATURE [App::DocumentObjectGroupPython] Cd_element001  label="Cd_element : 1"  # scripted group (container) (typed FeaturePython)
  n = 1
  ref = Cd_element
FEATURE [App::DocumentObjectGroupPython] Te_element001  label="Te_element : 1"  # scripted group (container) (typed FeaturePython)
  n = 1
  ref = Te_element
FEATURE [App::DocumentObjectGroupPython] G4_CADMIUM_TELLURIDE  # scripted group (container) (typed FeaturePython)
  Dunit = g/cm3
  Dvalue = 6.2
  Group = -> [Cd_element001,Te_element001]
  conduct = 2
  density = 1
  expand = 3
  formula = G4_CADMIUM_TELLURIDE
  name = G4_CADMIUM_TELLURIDE
  specific = 4
FEATURE [App::DocumentObjectGroupPython] Cd_element002  label="Cd_element : 002"  # scripted group (container) (typed FeaturePython)
  n = 1
  ref = Cd_element
FEATURE [App::DocumentObjectGroupPython] W_element001  label="W_element : 1"  # scripted group (container) (typed FeaturePython)
  n = 1
  ref = W_element
FEATURE [App::DocumentObjectGroupPython] O_element020  label="O_element : 008"  # scripted group (container) (typed FeaturePython)
  n = 4
  ref = O_element
FEATURE [App::DocumentObjectGroupPython] G4_CADMIUM_TUNGSTATE  # scripted group (container) (typed FeaturePython)
  Dunit = g/cm3
  Dvalue = 7.9
  Group = -> [Cd_element002,W_element001,O_element020]
  conduct = 2
  density = 1
  expand = 3
  formula = G4_CADMIUM_TUNGSTATE
  name = G4_CADMIUM_TUNGSTATE
  specific = 4
FEATURE [App::DocumentObjectGroupPython] Ca_element005  label="Ca_element : 1"  # scripted group (container) (typed FeaturePython)
  n = 1
  ref = Ca_element
FEATURE [App::DocumentObjectGroupPython] C_element022  label="C_element : 009"  # scripted group (container) (typed FeaturePython)
  n = 1
  ref = C_element
FEATURE [App::DocumentObjectGroupPython] O_element021  label="O_element : 009"  # scripted group (container) (typed FeaturePython)
  n = 3
  ref = O_element
FEATURE [App::DocumentObjectGroupPython] G4_CALCIUM_CARBONATE  # scripted group (container) (typed FeaturePython)
  Dunit = g/cm3
  Dvalue = 2.8
  Group = -> [Ca_element005,C_element022,O_element021]
  conduct = 2
  density = 1
  expand = 3
  formula = G4_CALCIUM_CARBONATE
  name = G4_CALCIUM_CARBONATE
  specific = 4
FEATURE [App::DocumentObjectGroupPython] Ca_element006  label="Ca_element : 002"  # scripted group (container) (typed FeaturePython)
  n = 1
  ref = Ca_element
FEATURE [App::DocumentObjectGroupPython] F_element005  label="F_element : 003"  # scripted group (container) (typed FeaturePython)
  n = 2
  ref = F_element
FEATURE [App::DocumentObjectGroupPython] G4_CALCIUM_FLUORIDE  # scripted group (container) (typed FeaturePython)
  Dunit = g/cm3
  Dvalue = 3.18
  Group = -> [Ca_element006,F_element005]
  conduct = 2
  density = 1
  expand = 3
  formula = G4_CALCIUM_FLUORIDE
  name = G4_CALCIUM_FLUORIDE
  specific = 4
FEATURE [App::DocumentObjectGroupPython] Ca_element007  label="Ca_element : 003"  # scripted group (container) (typed FeaturePython)
  n = 1
  ref = Ca_element
FEATURE [App::DocumentObjectGroupPython] O_element022  label="O_element : 010"  # scripted group (container) (typed FeaturePython)
  n = 1
  ref = O_element
FEATURE [App::DocumentObjectGroupPython] G4_CALCIUM_OXIDE  # scripted group (container) (typed FeaturePython)
  Dunit = g/cm3
  Dvalue = 3.3
  Group = -> [Ca_element007,O_element022]
  conduct = 2
  density = 1
  expand = 3
  formula = G4_CALCIUM_OXIDE
  name = G4_CALCIUM_OXIDE
  specific = 4
FEATURE [App::DocumentObjectGroupPython] Ca_element008  label="Ca_element : 004"  # scripted group (container) (typed FeaturePython)
  n = 1
  ref = Ca_element
FEATURE [App::DocumentObjectGroupPython] S_element007  label="S_element : 002"  # scripted group (container) (typed FeaturePython)
  n = 1
  ref = S_element
FEATURE [App::DocumentObjectGroupPython] O_element023  label="O_element : 011"  # scripted group (container) (typed FeaturePython)
  n = 4
  ref = O_element
FEATURE [App::DocumentObjectGroupPython] G4_CALCIUM_SULFATE  # scripted group (container) (typed FeaturePython)
  Dunit = g/cm3
  Dvalue = 2.96
  Group = -> [Ca_element008,S_element007,O_element023]
  conduct = 2
  density = 1
  expand = 3
  formula = G4_CALCIUM_SULFATE
  name = G4_CALCIUM_SULFATE
  specific = 4
FEATURE [App::DocumentObjectGroupPython] Ca_element009  label="Ca_element : 005"  # scripted group (container) (typed FeaturePython)
  n = 1
  ref = Ca_element
FEATURE [App::DocumentObjectGroupPython] W_element002  label="W_element : 002"  # scripted group (container) (typed FeaturePython)
  n = 1
  ref = W_element
FEATURE [App::DocumentObjectGroupPython] O_element024  label="O_element : 012"  # scripted group (container) (typed FeaturePython)
  n = 4
  ref = O_element
FEATURE [App::DocumentObjectGroupPython] G4_CALCIUM_TUNGSTATE  # scripted group (container) (typed FeaturePython)
  Dunit = g/cm3
  Dvalue = 6.062
  Group = -> [Ca_element009,W_element002,O_element024]
  conduct = 2
  density = 1
  expand = 3
  formula = G4_CALCIUM_TUNGSTATE
  name = G4_CALCIUM_TUNGSTATE
  specific = 4
FEATURE [App::DocumentObjectGroupPython] C_element023  label="C_element : 010"  # scripted group (container) (typed FeaturePython)
  n = 1
  ref = C_element
FEATURE [App::DocumentObjectGroupPython] O_element025  label="O_element : 013"  # scripted group (container) (typed FeaturePython)
  n = 2
  ref = O_element
FEATURE [App::DocumentObjectGroupPython] G4_CARBON_DIOXIDE  # scripted group (container) (typed FeaturePython)
  Dunit = g/cm3
  Dvalue = 0.00184212
  Group = -> [C_element023,O_element025]
  conduct = 2
  density = 1
  expand = 3
  formula = G4_CARBON_DIOXIDE
  name = G4_CARBON_DIOXIDE
  specific = 4
FEATURE [App::DocumentObjectGroupPython] C_element024  label="C_element : 011"  # scripted group (container) (typed FeaturePython)
  n = 1
  ref = C_element
FEATURE [App::DocumentObjectGroupPython] Cl_element004  label="Cl_element : 4"  # scripted group (container) (typed FeaturePython)
  n = 4
  ref = Cl_element
FEATURE [App::DocumentObjectGroupPython] G4_CARBON_TETRACHLORIDE  # scripted group (container) (typed FeaturePython)
  Dunit = g/cm3
  Dvalue = 1.594
  Group = -> [C_element024,Cl_element004]
  conduct = 2
  density = 1
  expand = 3
  formula = G4_CARBON_TETRACHLORIDE
  name = G4_CARBON_TETRACHLORIDE
  specific = 4
FEATURE [App::DocumentObjectGroupPython] C_element025  label="C_element : 012"  # scripted group (container) (typed FeaturePython)
  n = 6
  ref = C_element
FEATURE [App::DocumentObjectGroupPython] H_element021  label="H_element : 012"  # scripted group (container) (typed FeaturePython)
  n = 10
  ref = H_element
FEATURE [App::DocumentObjectGroupPython] O_element026  label="O_element : 5"  # scripted group (container) (typed FeaturePython)
  n = 5
  ref = O_element
FEATURE [App::DocumentObjectGroupPython] G4_CELLULOSE_CELLOPHANE  # scripted group (container) (typed FeaturePython)
  Dunit = g/cm3
  Dvalue = 1.42
  Group = -> [C_element025,H_element021,O_element026]
  conduct = 2
  density = 1
  expand = 3
  formula = G4_CELLULOSE_CELLOPHANE
  name = G4_CELLULOSE_CELLOPHANE
  specific = 4
FEATURE [App::DocumentObjectGroupPython] H_element022  label="H_element : 0.067"  # scripted group (container) (typed FeaturePython)
  n = 0.067125
FEATURE [App::DocumentObjectGroupPython] C_element026  label="C_element : 0.545"  # scripted group (container) (typed FeaturePython)
  n = 0.545403
FEATURE [App::DocumentObjectGroupPython] O_element027  label="O_element : 0.387"  # scripted group (container) (typed FeaturePython)
  n = 0.387472
FEATURE [App::DocumentObjectGroupPython] G4_CELLULOSE_BUTYRATE  # scripted group (container) (typed FeaturePython)
  Dunit = g/cm3
  Dvalue = 1.2
  Group = -> [H_element022,C_element026,O_element027]
  conduct = 2
  density = 1
  expand = 3
  formula = G4_CELLULOSE_BUTYRATE
  name = G4_CELLULOSE_BUTYRATE
  specific = 4
FEATURE [App::DocumentObjectGroupPython] H_element023  label="H_element : 0.029"  # scripted group (container) (typed FeaturePython)
  n = 0.029216
FEATURE [App::DocumentObjectGroupPython] C_element027  label="C_element : 0.271"  # scripted group (container) (typed FeaturePython)
  n = 0.271296
FEATURE [App::DocumentObjectGroupPython] N_element013  label="N_element : 0.121"  # scripted group (container) (typed FeaturePython)
  n = 0.121276
FEATURE [App::DocumentObjectGroupPython] O_element028  label="O_element : 0.578"  # scripted group (container) (typed FeaturePython)
  n = 0.578212
FEATURE [App::DocumentObjectGroupPython] G4_CELLULOSE_NITRATE  # scripted group (container) (typed FeaturePython)
  Dunit = g/cm3
  Dvalue = 1.49
  Group = -> [H_element023,C_element027,N_element013,O_element028]
  conduct = 2
  density = 1
  expand = 3
  formula = G4_CELLULOSE_NITRATE
  name = G4_CELLULOSE_NITRATE
  specific = 4
FEATURE [App::DocumentObjectGroupPython] H_element024  label="H_element : 0.108"  # scripted group (container) (typed FeaturePython)
  n = 0.107596
FEATURE [App::DocumentObjectGroupPython] N_element014  label="N_element : 0.001"  # scripted group (container) (typed FeaturePython)
  n = 0.0008
FEATURE [App::DocumentObjectGroupPython] O_element029  label="O_element : 0.875"  # scripted group (container) (typed FeaturePython)
  n = 0.874976
FEATURE [App::DocumentObjectGroupPython] S_element008  label="S_element : 0.015"  # scripted group (container) (typed FeaturePython)
  n = 0.014627
FEATURE [App::DocumentObjectGroupPython] Ce_element001  label="Ce_element : 0.002"  # scripted group (container) (typed FeaturePython)
  n = 0.002001
FEATURE [App::DocumentObjectGroupPython] G4_CERIC_SULFATE  # scripted group (container) (typed FeaturePython)
  Dunit = g/cm3
  Dvalue = 1.03
  Group = -> [H_element024,N_element014,O_element029,S_element008,Ce_element001]
  conduct = 2
  density = 1
  expand = 3
  formula = G4_CERIC_SULFATE
  name = G4_CERIC_SULFATE
  specific = 4
FEATURE [App::DocumentObjectGroupPython] Cs_element001  label="Cs_element : 1"  # scripted group (container) (typed FeaturePython)
  n = 1
  ref = Cs_element
FEATURE [App::DocumentObjectGroupPython] F_element006  label="F_element : 1"  # scripted group (container) (typed FeaturePython)
  n = 1
  ref = F_element
FEATURE [App::DocumentObjectGroupPython] G4_CESIUM_FLUORIDE  # scripted group (container) (typed FeaturePython)
  Dunit = g/cm3
  Dvalue = 4.115
  Group = -> [Cs_element001,F_element006]
  conduct = 2
  density = 1
  expand = 3
  formula = G4_CESIUM_FLUORIDE
  name = G4_CESIUM_FLUORIDE
  specific = 4
FEATURE [App::DocumentObjectGroupPython] Cs_element002  label="Cs_element : 002"  # scripted group (container) (typed FeaturePython)
  n = 1
  ref = Cs_element
FEATURE [App::DocumentObjectGroupPython] I_element001  label="I_element : 1"  # scripted group (container) (typed FeaturePython)
  n = 1
  ref = I_element
FEATURE [App::DocumentObjectGroupPython] G4_CESIUM_IODIDE  # scripted group (container) (typed FeaturePython)
  Dunit = g/cm3
  Dvalue = 4.51
  Group = -> [Cs_element002,I_element001]
  conduct = 2
  density = 1
  expand = 3
  formula = G4_CESIUM_IODIDE
  name = G4_CESIUM_IODIDE
  specific = 4
FEATURE [App::DocumentObjectGroupPython] C_element028  label="C_element : 013"  # scripted group (container) (typed FeaturePython)
  n = 6
  ref = C_element
FEATURE [App::DocumentObjectGroupPython] H_element025  label="H_element : 013"  # scripted group (container) (typed FeaturePython)
  n = 5
  ref = H_element
FEATURE [App::DocumentObjectGroupPython] Cl_element005  label="Cl_element : 1"  # scripted group (container) (typed FeaturePython)
  n = 1
  ref = Cl_element
FEATURE [App::DocumentObjectGroupPython] G4_CHLOROBENZENE  # scripted group (container) (typed FeaturePython)
  Dunit = g/cm3
  Dvalue = 1.1058
  Group = -> [C_element028,H_element025,Cl_element005]
  conduct = 2
  density = 1
  expand = 3
  formula = G4_CHLOROBENZENE
  name = G4_CHLOROBENZENE
  specific = 4
FEATURE [App::DocumentObjectGroupPython] C_element029  label="C_element : 014"  # scripted group (container) (typed FeaturePython)
  n = 1
  ref = C_element
FEATURE [App::DocumentObjectGroupPython] H_element026  label="H_element : 1"  # scripted group (container) (typed FeaturePython)
  n = 1
  ref = H_element
FEATURE [App::DocumentObjectGroupPython] Cl_element006  label="Cl_element : 3"  # scripted group (container) (typed FeaturePython)
  n = 3
  ref = Cl_element
FEATURE [App::DocumentObjectGroupPython] G4_CHLOROFORM  # scripted group (container) (typed FeaturePython)
  Dunit = g/cm3
  Dvalue = 1.4832
  Group = -> [C_element029,H_element026,Cl_element006]
  conduct = 2
  density = 1
  expand = 3
  formula = G4_CHLOROFORM
  name = G4_CHLOROFORM
  specific = 4
FEATURE [App::DocumentObjectGroupPython] H_element027  label="H_element : 0.010"  # scripted group (container) (typed FeaturePython)
  n = 0.01
FEATURE [App::DocumentObjectGroupPython] C_element030  label="C_element : 0.001"  # scripted group (container) (typed FeaturePython)
  n = 0.001
FEATURE [App::DocumentObjectGroupPython] O_element030  label="O_element : 0.529"  # scripted group (container) (typed FeaturePython)
  n = 0.529107
FEATURE [App::DocumentObjectGroupPython] Na_element005  label="Na_element : 0.016"  # scripted group (container) (typed FeaturePython)
  n = 0.016
FEATURE [App::DocumentObjectGroupPython] Mg_element003  label="Mg_element : 0.004"  # scripted group (container) (typed FeaturePython)
  n = 0.002
FEATURE [App::DocumentObjectGroupPython] Al_element002  label="Al_element : 0.034"  # scripted group (container) (typed FeaturePython)
  n = 0.033872
FEATURE [App::DocumentObjectGroupPython] Si_element002  label="Si_element : 0.337"  # scripted group (container) (typed FeaturePython)
  n = 0.337021
FEATURE [App::DocumentObjectGroupPython] K_element003  label="K_element : 0.013"  # scripted group (container) (typed FeaturePython)
  n = 0.013
FEATURE [App::DocumentObjectGroupPython] Ca_element010  label="Ca_element : 0.044"  # scripted group (container) (typed FeaturePython)
  n = 0.044
FEATURE [App::DocumentObjectGroupPython] Fe_element002  label="Fe_element : 0.014"  # scripted group (container) (typed FeaturePython)
  n = 0.014
FEATURE [App::DocumentObjectGroupPython] G4_CONCRETE  # scripted group (container) (typed FeaturePython)
  Dunit = g/cm3
  Dvalue = 2.3
  Group = -> [H_element027,C_element030,O_element030,Na_element005,Mg_element003,Al_element002,Si_element002,K_element003,Ca_element010,Fe_element002]
  conduct = 2
  density = 1
  expand = 3
  formula = G4_CONCRETE
  name = G4_CONCRETE
  specific = 4
FEATURE [App::DocumentObjectGroupPython] C_element031  label="C_element : 015"  # scripted group (container) (typed FeaturePython)
  n = 6
  ref = C_element
FEATURE [App::DocumentObjectGroupPython] H_element028  label="H_element : 12"  # scripted group (container) (typed FeaturePython)
  n = 12
  ref = H_element
FEATURE [App::DocumentObjectGroupPython] G4_CYCLOHEXANE  # scripted group (container) (typed FeaturePython)
  Dunit = g/cm3
  Dvalue = 0.779
  Group = -> [C_element031,H_element028]
  conduct = 2
  density = 1
  expand = 3
  formula = G4_CYCLOHEXANE
  name = G4_CYCLOHEXANE
  specific = 4
FEATURE [App::DocumentObjectGroupPython] C_element032  label="C_element : 016"  # scripted group (container) (typed FeaturePython)
  n = 6
  ref = C_element
FEATURE [App::DocumentObjectGroupPython] H_element029  label="H_element : 4"  # scripted group (container) (typed FeaturePython)
  n = 4
  ref = H_element
FEATURE [App::DocumentObjectGroupPython] Cl_element007  label="Cl_element : 2"  # scripted group (container) (typed FeaturePython)
  n = 2
  ref = Cl_element
FEATURE [App::DocumentObjectGroupPython] G4_1_2_DICHLOROBENZENE  label="G4_1.2-DICHLOROBENZENE"  # scripted group (container) (typed FeaturePython)
  Dunit = g/cm3
  Dvalue = 1.3048
  Group = -> [C_element032,H_element029,Cl_element007]
  conduct = 2
  density = 1
  expand = 3
  formula = G4_1.2-DICHLOROBENZENE
  name = G4_1.2-DICHLOROBENZENE
  specific = 4
FEATURE [App::DocumentObjectGroupPython] C_element033  label="C_element : 017"  # scripted group (container) (typed FeaturePython)
  n = 4
  ref = C_element
FEATURE [App::DocumentObjectGroupPython] H_element030  label="H_element : 8"  # scripted group (container) (typed FeaturePython)
  n = 8
  ref = H_element
FEATURE [App::DocumentObjectGroupPython] O_element031  label="O_element : 014"  # scripted group (container) (typed FeaturePython)
  n = 1
  ref = O_element
FEATURE [App::DocumentObjectGroupPython] Cl_element008  label="Cl_element : 005"  # scripted group (container) (typed FeaturePython)
  n = 2
  ref = Cl_element
FEATURE [App::DocumentObjectGroupPython] G4_DICHLORODIETHYL_ETHER  # scripted group (container) (typed FeaturePython)
  Dunit = g/cm3
  Dvalue = 1.2199
  Group = -> [C_element033,H_element030,O_element031,Cl_element008]
  conduct = 2
  density = 1
  expand = 3
  formula = G4_DICHLORODIETHYL_ETHER
  name = G4_DICHLORODIETHYL_ETHER
  specific = 4
FEATURE [App::DocumentObjectGroupPython] C_element034  label="C_element : 018"  # scripted group (container) (typed FeaturePython)
  n = 2
  ref = C_element
FEATURE [App::DocumentObjectGroupPython] H_element031  label="H_element : 014"  # scripted group (container) (typed FeaturePython)
  n = 4
  ref = H_element
FEATURE [App::DocumentObjectGroupPython] Cl_element009  label="Cl_element : 006"  # scripted group (container) (typed FeaturePython)
  n = 2
  ref = Cl_element
FEATURE [App::DocumentObjectGroupPython] G4_1_2_DICHLOROETHANE  label="G4_1.2-DICHLOROETHANE"  # scripted group (container) (typed FeaturePython)
  Dunit = g/cm3
  Dvalue = 1.2351
  Group = -> [C_element034,H_element031,Cl_element009]
  conduct = 2
  density = 1
  expand = 3
  formula = G4_1.2-DICHLOROETHANE
  name = G4_1.2-DICHLOROETHANE
  specific = 4
FEATURE [App::DocumentObjectGroupPython] C_element035  label="C_element : 019"  # scripted group (container) (typed FeaturePython)
  n = 4
  ref = C_element
FEATURE [App::DocumentObjectGroupPython] H_element032  label="H_element : 015"  # scripted group (container) (typed FeaturePython)
  n = 10
  ref = H_element
FEATURE [App::DocumentObjectGroupPython] O_element032  label="O_element : 015"  # scripted group (container) (typed FeaturePython)
  n = 1
  ref = O_element
FEATURE [App::DocumentObjectGroupPython] G4_DIETHYL_ETHER  # scripted group (container) (typed FeaturePython)
  Dunit = g/cm3
  Dvalue = 0.71378
  Group = -> [C_element035,H_element032,O_element032]
  conduct = 2
  density = 1
  expand = 3
  formula = G4_DIETHYL_ETHER
  name = G4_DIETHYL_ETHER
  specific = 4
FEATURE [App::DocumentObjectGroupPython] C_element036  label="C_element : 020"  # scripted group (container) (typed FeaturePython)
  n = 3
  ref = C_element
FEATURE [App::DocumentObjectGroupPython] H_element033  label="H_element : 016"  # scripted group (container) (typed FeaturePython)
  n = 7
  ref = H_element
FEATURE [App::DocumentObjectGroupPython] N_element015  label="N_element : 008"  # scripted group (container) (typed FeaturePython)
  n = 1
  ref = N_element
FEATURE [App::DocumentObjectGroupPython] O_element033  label="O_element : 016"  # scripted group (container) (typed FeaturePython)
  n = 1
  ref = O_element
FEATURE [App::DocumentObjectGroupPython] G4_N_N_DIMETHYL_FORMAMIDE  label="G4_N.N-DIMETHYL_FORMAMIDE"  # scripted group (container) (typed FeaturePython)
  Dunit = g/cm3
  Dvalue = 0.9487
  Group = -> [C_element036,H_element033,N_element015,O_element033]
  conduct = 2
  density = 1
  expand = 3
  formula = G4_N.N-DIMETHYL_FORMAMIDE
  name = G4_N.N-DIMETHYL_FORMAMIDE
  specific = 4
FEATURE [App::DocumentObjectGroupPython] C_element037  label="C_element : 021"  # scripted group (container) (typed FeaturePython)
  n = 2
  ref = C_element
FEATURE [App::DocumentObjectGroupPython] H_element034  label="H_element : 017"  # scripted group (container) (typed FeaturePython)
  n = 6
  ref = H_element
FEATURE [App::DocumentObjectGroupPython] O_element034  label="O_element : 017"  # scripted group (container) (typed FeaturePython)
  n = 1
  ref = O_element
FEATURE [App::DocumentObjectGroupPython] S_element009  label="S_element : 003"  # scripted group (container) (typed FeaturePython)
  n = 1
  ref = S_element
FEATURE [App::DocumentObjectGroupPython] G4_DIMETHYL_SULFOXIDE  # scripted group (container) (typed FeaturePython)
  Dunit = g/cm3
  Dvalue = 1.1014
  Group = -> [C_element037,H_element034,O_element034,S_element009]
  conduct = 2
  density = 1
  expand = 3
  formula = G4_DIMETHYL_SULFOXIDE
  name = G4_DIMETHYL_SULFOXIDE
  specific = 4
FEATURE [App::DocumentObjectGroupPython] C_element038  label="C_element : 022"  # scripted group (container) (typed FeaturePython)
  n = 2
  ref = C_element
FEATURE [App::DocumentObjectGroupPython] H_element035  label="H_element : 018"  # scripted group (container) (typed FeaturePython)
  n = 6
  ref = H_element
FEATURE [App::DocumentObjectGroupPython] G4_ETHANE  # scripted group (container) (typed FeaturePython)
  Dunit = g/cm3
  Dvalue = 0.00125324
  Group = -> [C_element038,H_element035]
  conduct = 2
  density = 1
  expand = 3
  formula = G4_ETHANE
  name = G4_ETHANE
  specific = 4
FEATURE [App::DocumentObjectGroupPython] C_element039  label="C_element : 023"  # scripted group (container) (typed FeaturePython)
  n = 2
  ref = C_element
FEATURE [App::DocumentObjectGroupPython] H_element036  label="H_element : 019"  # scripted group (container) (typed FeaturePython)
  n = 6
  ref = H_element
FEATURE [App::DocumentObjectGroupPython] O_element035  label="O_element : 018"  # scripted group (container) (typed FeaturePython)
  n = 1
  ref = O_element
FEATURE [App::DocumentObjectGroupPython] G4_ETHYL_ALCOHOL  # scripted group (container) (typed FeaturePython)
  Dunit = g/cm3
  Dvalue = 0.7893
  Group = -> [C_element039,H_element036,O_element035]
  conduct = 2
  density = 1
  expand = 3
  formula = G4_ETHYL_ALCOHOL
  name = G4_ETHYL_ALCOHOL
  specific = 4
FEATURE [App::DocumentObjectGroupPython] H_element037  label="H_element : 0.090"  # scripted group (container) (typed FeaturePython)
  n = 0.090027
FEATURE [App::DocumentObjectGroupPython] C_element040  label="C_element : 0.585"  # scripted group (container) (typed FeaturePython)
  n = 0.585182
FEATURE [App::DocumentObjectGroupPython] O_element036  label="O_element : 0.325"  # scripted group (container) (typed FeaturePython)
  n = 0.324791
FEATURE [App::DocumentObjectGroupPython] G4_ETHYL_CELLULOSE  # scripted group (container) (typed FeaturePython)
  Dunit = g/cm3
  Dvalue = 1.13
  Group = -> [H_element037,C_element040,O_element036]
  conduct = 2
  density = 1
  expand = 3
  formula = G4_ETHYL_CELLULOSE
  name = G4_ETHYL_CELLULOSE
  specific = 4
FEATURE [App::DocumentObjectGroupPython] C_element041  label="C_element : 024"  # scripted group (container) (typed FeaturePython)
  n = 2
  ref = C_element
FEATURE [App::DocumentObjectGroupPython] H_element038  label="H_element : 020"  # scripted group (container) (typed FeaturePython)
  n = 4
  ref = H_element
FEATURE [App::DocumentObjectGroupPython] G4_ETHYLENE  # scripted group (container) (typed FeaturePython)
  Dunit = g/cm3
  Dvalue = 0.00117497
  Group = -> [C_element041,H_element038]
  conduct = 2
  density = 1
  expand = 3
  formula = G4_ETHYLENE
  name = G4_ETHYLENE
  specific = 4
FEATURE [App::DocumentObjectGroupPython] H_element039  label="H_element : 0.096"  # scripted group (container) (typed FeaturePython)
  n = 0.096
FEATURE [App::DocumentObjectGroupPython] C_element042  label="C_element : 0.195"  # scripted group (container) (typed FeaturePython)
  n = 0.195
FEATURE [App::DocumentObjectGroupPython] N_element016  label="N_element : 0.057"  # scripted group (container) (typed FeaturePython)
  n = 0.057
FEATURE [App::DocumentObjectGroupPython] O_element037  label="O_element : 0.646"  # scripted group (container) (typed FeaturePython)
  n = 0.646
FEATURE [App::DocumentObjectGroupPython] Na_element006  label="Na_element : 0.017"  # scripted group (container) (typed FeaturePython)
  n = 0.001
FEATURE [App::DocumentObjectGroupPython] P_element005  label="P_element : 0.104"  # scripted group (container) (typed FeaturePython)
  n = 0.001
FEATURE [App::DocumentObjectGroupPython] S_element010  label="S_element : 0.016"  # scripted group (container) (typed FeaturePython)
  n = 0.003
FEATURE [App::DocumentObjectGroupPython] Cl_element010  label="Cl_element : 0.005"  # scripted group (container) (typed FeaturePython)
  n = 0.001
FEATURE [App::DocumentObjectGroupPython] G4_EYE_LENS_ICRP  # scripted group (container) (typed FeaturePython)
  Dunit = g/cm3
  Dvalue = 1.07
  Group = -> [H_element039,C_element042,N_element016,O_element037,Na_element006,P_element005,S_element010,Cl_element010]
  conduct = 2
  density = 1
  expand = 3
  formula = G4_EYE_LENS_ICRP
  name = G4_EYE_LENS_ICRP
  specific = 4
FEATURE [App::DocumentObjectGroupPython] Fe_element003  label="Fe_element : 2"  # scripted group (container) (typed FeaturePython)
  n = 2
  ref = Fe_element
FEATURE [App::DocumentObjectGroupPython] O_element038  label="O_element : 019"  # scripted group (container) (typed FeaturePython)
  n = 3
  ref = O_element
FEATURE [App::DocumentObjectGroupPython] G4_FERRIC_OXIDE  # scripted group (container) (typed FeaturePython)
  Dunit = g/cm3
  Dvalue = 5.2
  Group = -> [Fe_element003,O_element038]
  conduct = 2
  density = 1
  expand = 3
  formula = G4_FERRIC_OXIDE
  name = G4_FERRIC_OXIDE
  specific = 4
FEATURE [App::DocumentObjectGroupPython] Fe_element004  label="Fe_element : 1"  # scripted group (container) (typed FeaturePython)
  n = 1
  ref = Fe_element
FEATURE [App::DocumentObjectGroupPython] B_element003  label="B_element : 1"  # scripted group (container) (typed FeaturePython)
  n = 1
  ref = B_element
FEATURE [App::DocumentObjectGroupPython] G4_FERROBORIDE  # scripted group (container) (typed FeaturePython)
  Dunit = g/cm3
  Dvalue = 7.15
  Group = -> [Fe_element004,B_element003]
  conduct = 2
  density = 1
  expand = 3
  formula = G4_FERROBORIDE
  name = G4_FERROBORIDE
  specific = 4
FEATURE [App::DocumentObjectGroupPython] Fe_element005  label="Fe_element : 003"  # scripted group (container) (typed FeaturePython)
  n = 1
  ref = Fe_element
FEATURE [App::DocumentObjectGroupPython] O_element039  label="O_element : 020"  # scripted group (container) (typed FeaturePython)
  n = 1
  ref = O_element
FEATURE [App::DocumentObjectGroupPython] G4_FERROUS_OXIDE  # scripted group (container) (typed FeaturePython)
  Dunit = g/cm3
  Dvalue = 5.7
  Group = -> [Fe_element005,O_element039]
  conduct = 2
  density = 1
  expand = 3
  formula = G4_FERROUS_OXIDE
  name = G4_FERROUS_OXIDE
  specific = 4
FEATURE [App::DocumentObjectGroupPython] H_element040  label="H_element : 0.115"  # scripted group (container) (typed FeaturePython)
  n = 0.108259
FEATURE [App::DocumentObjectGroupPython] N_element017  label="N_element : 0.000"  # scripted group (container) (typed FeaturePython)
  n = 2.7e-05
FEATURE [App::DocumentObjectGroupPython] O_element040  label="O_element : 0.879"  # scripted group (container) (typed FeaturePython)
  n = 0.878636
FEATURE [App::DocumentObjectGroupPython] Na_element007  label="Na_element : 0.000"  # scripted group (container) (typed FeaturePython)
  n = 2.2e-05
FEATURE [App::DocumentObjectGroupPython] S_element011  label="S_element : 0.013"  # scripted group (container) (typed FeaturePython)
  n = 0.012968
FEATURE [App::DocumentObjectGroupPython] Cl_element011  label="Cl_element : 0.000"  # scripted group (container) (typed FeaturePython)
  n = 3.4e-05
FEATURE [App::DocumentObjectGroupPython] Fe_element006  label="Fe_element : 0.000"  # scripted group (container) (typed FeaturePython)
  n = 5.4e-05
FEATURE [App::DocumentObjectGroupPython] G4_FERROUS_SULFATE  # scripted group (container) (typed FeaturePython)
  Dunit = g/cm3
  Dvalue = 1.024
  Group = -> [H_element040,N_element017,O_element040,Na_element007,S_element011,Cl_element011,Fe_element006]
  conduct = 2
  density = 1
  expand = 3
  formula = G4_FERROUS_SULFATE
  name = G4_FERROUS_SULFATE
  specific = 4
FEATURE [App::DocumentObjectGroupPython] C_element043  label="C_element : 0.099"  # scripted group (container) (typed FeaturePython)
  n = 0.099335
FEATURE [App::DocumentObjectGroupPython] F_element007  label="F_element : 0.314"  # scripted group (container) (typed FeaturePython)
  n = 0.314247
FEATURE [App::DocumentObjectGroupPython] Cl_element012  label="Cl_element : 0.586"  # scripted group (container) (typed FeaturePython)
  n = 0.586418
FEATURE [App::DocumentObjectGroupPython] G4_FREON_12  label="G4_FREON-12"  # scripted group (container) (typed FeaturePython)
  Dunit = g/cm3
  Dvalue = 1.12
  Group = -> [C_element043,F_element007,Cl_element012]
  conduct = 2
  density = 1
  expand = 3
  formula = G4_FREON-12
  name = G4_FREON-12
  specific = 4
FEATURE [App::DocumentObjectGroupPython] C_element044  label="C_element : 0.057"  # scripted group (container) (typed FeaturePython)
  n = 0.057245
FEATURE [App::DocumentObjectGroupPython] F_element008  label="F_element : 0.181"  # scripted group (container) (typed FeaturePython)
  n = 0.181096
FEATURE [App::DocumentObjectGroupPython] Br_element001  label="Br_element : 0.762"  # scripted group (container) (typed FeaturePython)
  n = 0.761659
FEATURE [App::DocumentObjectGroupPython] G4_FREON_12B2  label="G4_FREON-12B2"  # scripted group (container) (typed FeaturePython)
  Dunit = g/cm3
  Dvalue = 1.8
  Group = -> [C_element044,F_element008,Br_element001]
  conduct = 2
  density = 1
  expand = 3
  formula = G4_FREON-12B2
  name = G4_FREON-12B2
  specific = 4
FEATURE [App::DocumentObjectGroupPython] C_element045  label="C_element : 0.115"  # scripted group (container) (typed FeaturePython)
  n = 0.114983
FEATURE [App::DocumentObjectGroupPython] F_element009  label="F_element : 0.546"  # scripted group (container) (typed FeaturePython)
  n = 0.545621
FEATURE [App::DocumentObjectGroupPython] Cl_element013  label="Cl_element : 0.339"  # scripted group (container) (typed FeaturePython)
  n = 0.339396
FEATURE [App::DocumentObjectGroupPython] G4_FREON_13  label="G4_FREON-13"  # scripted group (container) (typed FeaturePython)
  Dunit = g/cm3
  Dvalue = 0.95
  Group = -> [C_element045,F_element009,Cl_element013]
  conduct = 2
  density = 1
  expand = 3
  formula = G4_FREON-13
  name = G4_FREON-13
  specific = 4
FEATURE [App::DocumentObjectGroupPython] C_element046  label="C_element : 025"  # scripted group (container) (typed FeaturePython)
  n = 1
  ref = C_element
FEATURE [App::DocumentObjectGroupPython] F_element010  label="F_element : 3"  # scripted group (container) (typed FeaturePython)
  n = 3
  ref = F_element
FEATURE [App::DocumentObjectGroupPython] Br_element002  label="Br_element : 1"  # scripted group (container) (typed FeaturePython)
  n = 1
  ref = Br_element
FEATURE [App::DocumentObjectGroupPython] G4_FREON_13B1  label="G4_FREON-13B1"  # scripted group (container) (typed FeaturePython)
  Dunit = g/cm3
  Dvalue = 1.5
  Group = -> [C_element046,F_element010,Br_element002]
  conduct = 2
  density = 1
  expand = 3
  formula = G4_FREON-13B1
  name = G4_FREON-13B1
  specific = 4
FEATURE [App::DocumentObjectGroupPython] C_element047  label="C_element : 0.061"  # scripted group (container) (typed FeaturePython)
  n = 0.061309
FEATURE [App::DocumentObjectGroupPython] F_element011  label="F_element : 0.291"  # scripted group (container) (typed FeaturePython)
  n = 0.290924
FEATURE [App::DocumentObjectGroupPython] I_element002  label="I_element : 0.648"  # scripted group (container) (typed FeaturePython)
  n = 0.647767
FEATURE [App::DocumentObjectGroupPython] G4_FREON_13I1  label="G4_FREON-13I1"  # scripted group (container) (typed FeaturePython)
  Dunit = g/cm3
  Dvalue = 1.8
  Group = -> [C_element047,F_element011,I_element002]
  conduct = 2
  density = 1
  expand = 3
  formula = G4_FREON-13I1
  name = G4_FREON-13I1
  specific = 4
FEATURE [App::DocumentObjectGroupPython] Gd_element001  label="Gd_element : 2"  # scripted group (container) (typed FeaturePython)
  n = 2
  ref = Gd_element
FEATURE [App::DocumentObjectGroupPython] O_element041  label="O_element : 021"  # scripted group (container) (typed FeaturePython)
  n = 2
  ref = O_element
FEATURE [App::DocumentObjectGroupPython] S_element012  label="S_element : 004"  # scripted group (container) (typed FeaturePython)
  n = 1
  ref = S_element
FEATURE [App::DocumentObjectGroupPython] G4_GADOLINIUM_OXYSULFIDE  # scripted group (container) (typed FeaturePython)
  Dunit = g/cm3
  Dvalue = 7.44
  Group = -> [Gd_element001,O_element041,S_element012]
  conduct = 2
  density = 1
  expand = 3
  formula = G4_GADOLINIUM_OXYSULFIDE
  name = G4_GADOLINIUM_OXYSULFIDE
  specific = 4
FEATURE [App::DocumentObjectGroupPython] Ga_element001  label="Ga_element : 1"  # scripted group (container) (typed FeaturePython)
  n = 1
  ref = Ga_element
FEATURE [App::DocumentObjectGroupPython] As_element001  label="As_element : 1"  # scripted group (container) (typed FeaturePython)
  n = 1
  ref = As_element
FEATURE [App::DocumentObjectGroupPython] G4_GALLIUM_ARSENIDE  # scripted group (container) (typed FeaturePython)
  Dunit = g/cm3
  Dvalue = 5.31
  Group = -> [Ga_element001,As_element001]
  conduct = 2
  density = 1
  expand = 3
  formula = G4_GALLIUM_ARSENIDE
  name = G4_GALLIUM_ARSENIDE
  specific = 4
FEATURE [App::DocumentObjectGroupPython] H_element041  label="H_element : 0.081"  # scripted group (container) (typed FeaturePython)
  n = 0.08118
FEATURE [App::DocumentObjectGroupPython] C_element048  label="C_element : 0.416"  # scripted group (container) (typed FeaturePython)
  n = 0.41606
FEATURE [App::DocumentObjectGroupPython] N_element018  label="N_element : 0.111"  # scripted group (container) (typed FeaturePython)
  n = 0.11124
FEATURE [App::DocumentObjectGroupPython] O_element042  label="O_element : 0.381"  # scripted group (container) (typed FeaturePython)
  n = 0.38064
FEATURE [App::DocumentObjectGroupPython] S_element013  label="S_element : 0.011"  # scripted group (container) (typed FeaturePython)
  n = 0.01088
FEATURE [App::DocumentObjectGroupPython] G4_GEL_PHOTO_EMULSION  # scripted group (container) (typed FeaturePython)
  Dunit = g/cm3
  Dvalue = 1.2914
  Group = -> [H_element041,C_element048,N_element018,O_element042,S_element013]
  conduct = 2
  density = 1
  expand = 3
  formula = G4_GEL_PHOTO_EMULSION
  name = G4_GEL_PHOTO_EMULSION
  specific = 4
FEATURE [App::DocumentObjectGroupPython] B_element004  label="B_element : 0.040"  # scripted group (container) (typed FeaturePython)
  n = 0.0400639
FEATURE [App::DocumentObjectGroupPython] O_element043  label="O_element : 0.540"  # scripted group (container) (typed FeaturePython)
  n = 0.539561
FEATURE [App::DocumentObjectGroupPython] Na_element008  label="Na_element : 0.028"  # scripted group (container) (typed FeaturePython)
  n = 0.0281909
FEATURE [App::DocumentObjectGroupPython] Al_element003  label="Al_element : 0.012"  # scripted group (container) (typed FeaturePython)
  n = 0.011644
FEATURE [App::DocumentObjectGroupPython] Si_element003  label="Si_element : 0.377"  # scripted group (container) (typed FeaturePython)
  n = 0.377219
FEATURE [App::DocumentObjectGroupPython] K_element004  label="K_element : 0.014"  # scripted group (container) (typed FeaturePython)
  n = 0.00332099
FEATURE [App::DocumentObjectGroupPython] G4_Pyrex_Glass  # scripted group (container) (typed FeaturePython)
  Dunit = g/cm3
  Dvalue = 2.23
  Group = -> [B_element004,O_element043,Na_element008,Al_element003,Si_element003,K_element004]
  conduct = 2
  density = 1
  expand = 3
  formula = G4_Pyrex_Glass
  name = G4_Pyrex_Glass
  specific = 4
FEATURE [App::DocumentObjectGroupPython] O_element044  label="O_element : 0.156"  # scripted group (container) (typed FeaturePython)
  n = 0.156453
FEATURE [App::DocumentObjectGroupPython] Si_element004  label="Si_element : 0.081"  # scripted group (container) (typed FeaturePython)
  n = 0.080866
FEATURE [App::DocumentObjectGroupPython] Ti_element001  label="Ti_element : 0.008"  # scripted group (container) (typed FeaturePython)
  n = 0.008092
FEATURE [App::DocumentObjectGroupPython] As_element002  label="As_element : 0.003"  # scripted group (container) (typed FeaturePython)
  n = 0.002651
FEATURE [App::DocumentObjectGroupPython] Pb_element001  label="Pb_element : 0.752"  # scripted group (container) (typed FeaturePython)
  n = 0.751938
FEATURE [App::DocumentObjectGroupPython] G4_GLASS_LEAD  # scripted group (container) (typed FeaturePython)
  Dunit = g/cm3
  Dvalue = 6.22
  Group = -> [O_element044,Si_element004,Ti_element001,As_element002,Pb_element001]
  conduct = 2
  density = 1
  expand = 3
  formula = G4_GLASS_LEAD
  name = G4_GLASS_LEAD
  specific = 4
FEATURE [App::DocumentObjectGroupPython] O_element045  label="O_element : 0.460"  # scripted group (container) (typed FeaturePython)
  n = 0.4598
FEATURE [App::DocumentObjectGroupPython] Na_element009  label="Na_element : 0.096"  # scripted group (container) (typed FeaturePython)
  n = 0.0964411
FEATURE [App::DocumentObjectGroupPython] Si_element005  label="Si_element : 0.378"  # scripted group (container) (typed FeaturePython)
  n = 0.336553
FEATURE [App::DocumentObjectGroupPython] Ca_element011  label="Ca_element : 0.107"  # scripted group (container) (typed FeaturePython)
  n = 0.107205
FEATURE [App::DocumentObjectGroupPython] G4_GLASS_PLATE  # scripted group (container) (typed FeaturePython)
  Dunit = g/cm3
  Dvalue = 2.4
  Group = -> [O_element045,Na_element009,Si_element005,Ca_element011]
  conduct = 2
  density = 1
  expand = 3
  formula = G4_GLASS_PLATE
  name = G4_GLASS_PLATE
  specific = 4
FEATURE [App::DocumentObjectGroupPython] C_element049  label="C_element : 026"  # scripted group (container) (typed FeaturePython)
  n = 5
  ref = C_element
FEATURE [App::DocumentObjectGroupPython] H_element042  label="H_element : 021"  # scripted group (container) (typed FeaturePython)
  n = 10
  ref = H_element
FEATURE [App::DocumentObjectGroupPython] N_element019  label="N_element : 2"  # scripted group (container) (typed FeaturePython)
  n = 2
  ref = N_element
FEATURE [App::DocumentObjectGroupPython] O_element046  label="O_element : 022"  # scripted group (container) (typed FeaturePython)
  n = 3
  ref = O_element
FEATURE [App::DocumentObjectGroupPython] G4_GLUTAMINE  # scripted group (container) (typed FeaturePython)
  Dunit = g/cm3
  Dvalue = 1.46
  Group = -> [C_element049,H_element042,N_element019,O_element046]
  conduct = 2
  density = 1
  expand = 3
  formula = G4_GLUTAMINE
  name = G4_GLUTAMINE
  specific = 4
FEATURE [App::DocumentObjectGroupPython] C_element050  label="C_element : 027"  # scripted group (container) (typed FeaturePython)
  n = 3
  ref = C_element
FEATURE [App::DocumentObjectGroupPython] H_element043  label="H_element : 022"  # scripted group (container) (typed FeaturePython)
  n = 8
  ref = H_element
FEATURE [App::DocumentObjectGroupPython] O_element047  label="O_element : 023"  # scripted group (container) (typed FeaturePython)
  n = 3
  ref = O_element
FEATURE [App::DocumentObjectGroupPython] G4_GLYCEROL  # scripted group (container) (typed FeaturePython)
  Dunit = g/cm3
  Dvalue = 1.2613
  Group = -> [C_element050,H_element043,O_element047]
  conduct = 2
  density = 1
  expand = 3
  formula = G4_GLYCEROL
  name = G4_GLYCEROL
  specific = 4
FEATURE [App::DocumentObjectGroupPython] C_element051  label="C_element : 028"  # scripted group (container) (typed FeaturePython)
  n = 5
  ref = C_element
FEATURE [App::DocumentObjectGroupPython] H_element044  label="H_element : 023"  # scripted group (container) (typed FeaturePython)
  n = 5
  ref = H_element
FEATURE [App::DocumentObjectGroupPython] N_element020  label="N_element : 009"  # scripted group (container) (typed FeaturePython)
  n = 5
  ref = N_element
FEATURE [App::DocumentObjectGroupPython] O_element048  label="O_element : 024"  # scripted group (container) (typed FeaturePython)
  n = 1
  ref = O_element
FEATURE [App::DocumentObjectGroupPython] G4_GUANINE  # scripted group (container) (typed FeaturePython)
  Dunit = g/cm3
  Dvalue = 2.2
  Group = -> [C_element051,H_element044,N_element020,O_element048]
  conduct = 2
  density = 1
  expand = 3
  formula = G4_GUANINE
  name = G4_GUANINE
  specific = 4
FEATURE [App::DocumentObjectGroupPython] Ca_element012  label="Ca_element : 006"  # scripted group (container) (typed FeaturePython)
  n = 1
  ref = Ca_element
FEATURE [App::DocumentObjectGroupPython] S_element014  label="S_element : 005"  # scripted group (container) (typed FeaturePython)
  n = 1
  ref = S_element
FEATURE [App::DocumentObjectGroupPython] O_element049  label="O_element : 6"  # scripted group (container) (typed FeaturePython)
  n = 6
  ref = O_element
FEATURE [App::DocumentObjectGroupPython] H_element045  label="H_element : 024"  # scripted group (container) (typed FeaturePython)
  n = 4
  ref = H_element
FEATURE [App::DocumentObjectGroupPython] G4_GYPSUM  # scripted group (container) (typed FeaturePython)
  Dunit = g/cm3
  Dvalue = 2.32
  Group = -> [Ca_element012,S_element014,O_element049,H_element045]
  conduct = 2
  density = 1
  expand = 3
  formula = G4_GYPSUM
  name = G4_GYPSUM
  specific = 4
FEATURE [App::DocumentObjectGroupPython] C_element052  label="C_element : 7"  # scripted group (container) (typed FeaturePython)
  n = 7
  ref = C_element
FEATURE [App::DocumentObjectGroupPython] H_element046  label="H_element : 16"  # scripted group (container) (typed FeaturePython)
  n = 16
  ref = H_element
FEATURE [App::DocumentObjectGroupPython] G4_N_HEPTANE  label="G4_N-HEPTANE"  # scripted group (container) (typed FeaturePython)
  Dunit = g/cm3
  Dvalue = 0.68376
  Group = -> [C_element052,H_element046]
  conduct = 2
  density = 1
  expand = 3
  formula = G4_N-HEPTANE
  name = G4_N-HEPTANE
  specific = 4
FEATURE [App::DocumentObjectGroupPython] C_element053  label="C_element : 029"  # scripted group (container) (typed FeaturePython)
  n = 6
  ref = C_element
FEATURE [App::DocumentObjectGroupPython] H_element047  label="H_element : 14"  # scripted group (container) (typed FeaturePython)
  n = 14
  ref = H_element
FEATURE [App::DocumentObjectGroupPython] G4_N_HEXANE  label="G4_N-HEXANE"  # scripted group (container) (typed FeaturePython)
  Dunit = g/cm3
  Dvalue = 0.6603
  Group = -> [C_element053,H_element047]
  conduct = 2
  density = 1
  expand = 3
  formula = G4_N-HEXANE
  name = G4_N-HEXANE
  specific = 4
FEATURE [App::DocumentObjectGroupPython] C_element054  label="C_element : 22"  # scripted group (container) (typed FeaturePython)
  n = 22
  ref = C_element
FEATURE [App::DocumentObjectGroupPython] H_element048  label="H_element : 025"  # scripted group (container) (typed FeaturePython)
  n = 10
  ref = H_element
FEATURE [App::DocumentObjectGroupPython] N_element021  label="N_element : 010"  # scripted group (container) (typed FeaturePython)
  n = 2
  ref = N_element
FEATURE [App::DocumentObjectGroupPython] O_element050  label="O_element : 025"  # scripted group (container) (typed FeaturePython)
  n = 5
  ref = O_element
FEATURE [App::DocumentObjectGroupPython] G4_KAPTON  # scripted group (container) (typed FeaturePython)
  Dunit = g/cm3
  Dvalue = 1.42
  Group = -> [C_element054,H_element048,N_element021,O_element050]
  conduct = 2
  density = 1
  expand = 3
  formula = G4_KAPTON
  name = G4_KAPTON
  specific = 4
FEATURE [App::DocumentObjectGroupPython] La_element001  label="La_element : 1"  # scripted group (container) (typed FeaturePython)
  n = 1
  ref = La_element
FEATURE [App::DocumentObjectGroupPython] Br_element003  label="Br_element : 002"  # scripted group (container) (typed FeaturePython)
  n = 1
  ref = Br_element
FEATURE [App::DocumentObjectGroupPython] O_element051  label="O_element : 026"  # scripted group (container) (typed FeaturePython)
  n = 1
  ref = O_element
FEATURE [App::DocumentObjectGroupPython] G4_LANTHANUM_OXYBROMIDE  # scripted group (container) (typed FeaturePython)
  Dunit = g/cm3
  Dvalue = 6.28
  Group = -> [La_element001,Br_element003,O_element051]
  conduct = 2
  density = 1
  expand = 3
  formula = G4_LANTHANUM_OXYBROMIDE
  name = G4_LANTHANUM_OXYBROMIDE
  specific = 4
FEATURE [App::DocumentObjectGroupPython] La_element002  label="La_element : 2"  # scripted group (container) (typed FeaturePython)
  n = 2
  ref = La_element
FEATURE [App::DocumentObjectGroupPython] O_element052  label="O_element : 027"  # scripted group (container) (typed FeaturePython)
  n = 2
  ref = O_element
FEATURE [App::DocumentObjectGroupPython] S_element015  label="S_element : 006"  # scripted group (container) (typed FeaturePython)
  n = 1
  ref = S_element
FEATURE [App::DocumentObjectGroupPython] G4_LANTHANUM_OXYSULFIDE  # scripted group (container) (typed FeaturePython)
  Dunit = g/cm3
  Dvalue = 5.86
  Group = -> [La_element002,O_element052,S_element015]
  conduct = 2
  density = 1
  expand = 3
  formula = G4_LANTHANUM_OXYSULFIDE
  name = G4_LANTHANUM_OXYSULFIDE
  specific = 4
FEATURE [App::DocumentObjectGroupPython] O_element053  label="O_element : 0.072"  # scripted group (container) (typed FeaturePython)
  n = 0.071682
FEATURE [App::DocumentObjectGroupPython] Pb_element002  label="Pb_element : 0.928"  # scripted group (container) (typed FeaturePython)
  n = 0.928318
FEATURE [App::DocumentObjectGroupPython] G4_LEAD_OXIDE  # scripted group (container) (typed FeaturePython)
  Dunit = g/cm3
  Dvalue = 9.53
  Group = -> [O_element053,Pb_element002]
  conduct = 2
  density = 1
  expand = 3
  formula = G4_LEAD_OXIDE
  name = G4_LEAD_OXIDE
  specific = 4
FEATURE [App::DocumentObjectGroupPython] Li_element001  label="Li_element : 1"  # scripted group (container) (typed FeaturePython)
  n = 1
  ref = Li_element
FEATURE [App::DocumentObjectGroupPython] N_element022  label="N_element : 011"  # scripted group (container) (typed FeaturePython)
  n = 1
  ref = N_element
FEATURE [App::DocumentObjectGroupPython] H_element049  label="H_element : 026"  # scripted group (container) (typed FeaturePython)
  n = 2
  ref = H_element
FEATURE [App::DocumentObjectGroupPython] G4_LITHIUM_AMIDE  # scripted group (container) (typed FeaturePython)
  Dunit = g/cm3
  Dvalue = 1.178
  Group = -> [Li_element001,N_element022,H_element049]
  conduct = 2
  density = 1
  expand = 3
  formula = G4_LITHIUM_AMIDE
  name = G4_LITHIUM_AMIDE
  specific = 4
FEATURE [App::DocumentObjectGroupPython] Li_element002  label="Li_element : 2"  # scripted group (container) (typed FeaturePython)
  n = 2
  ref = Li_element
FEATURE [App::DocumentObjectGroupPython] C_element055  label="C_element : 030"  # scripted group (container) (typed FeaturePython)
  n = 1
  ref = C_element
FEATURE [App::DocumentObjectGroupPython] O_element054  label="O_element : 028"  # scripted group (container) (typed FeaturePython)
  n = 3
  ref = O_element
FEATURE [App::DocumentObjectGroupPython] G4_LITHIUM_CARBONATE  # scripted group (container) (typed FeaturePython)
  Dunit = g/cm3
  Dvalue = 2.11
  Group = -> [Li_element002,C_element055,O_element054]
  conduct = 2
  density = 1
  expand = 3
  formula = G4_LITHIUM_CARBONATE
  name = G4_LITHIUM_CARBONATE
  specific = 4
FEATURE [App::DocumentObjectGroupPython] Li_element003  label="Li_element : 003"  # scripted group (container) (typed FeaturePython)
  n = 1
  ref = Li_element
FEATURE [App::DocumentObjectGroupPython] F_element012  label="F_element : 004"  # scripted group (container) (typed FeaturePython)
  n = 1
  ref = F_element
FEATURE [App::DocumentObjectGroupPython] G4_LITHIUM_FLUORIDE  # scripted group (container) (typed FeaturePython)
  Dunit = g/cm3
  Dvalue = 2.635
  Group = -> [Li_element003,F_element012]
  conduct = 2
  density = 1
  expand = 3
  formula = G4_LITHIUM_FLUORIDE
  name = G4_LITHIUM_FLUORIDE
  specific = 4
FEATURE [App::DocumentObjectGroupPython] Li_element004  label="Li_element : 004"  # scripted group (container) (typed FeaturePython)
  n = 1
  ref = Li_element
FEATURE [App::DocumentObjectGroupPython] H_element050  label="H_element : 027"  # scripted group (container) (typed FeaturePython)
  n = 1
  ref = H_element
FEATURE [App::DocumentObjectGroupPython] G4_LITHIUM_HYDRIDE  # scripted group (container) (typed FeaturePython)
  Dunit = g/cm3
  Dvalue = 0.82
  Group = -> [Li_element004,H_element050]
  conduct = 2
  density = 1
  expand = 3
  formula = G4_LITHIUM_HYDRIDE
  name = G4_LITHIUM_HYDRIDE
  specific = 4
FEATURE [App::DocumentObjectGroupPython] Li_element005  label="Li_element : 005"  # scripted group (container) (typed FeaturePython)
  n = 1
  ref = Li_element
FEATURE [App::DocumentObjectGroupPython] I_element003  label="I_element : 002"  # scripted group (container) (typed FeaturePython)
  n = 1
  ref = I_element
FEATURE [App::DocumentObjectGroupPython] G4_LITHIUM_IODIDE  # scripted group (container) (typed FeaturePython)
  Dunit = g/cm3
  Dvalue = 3.494
  Group = -> [Li_element005,I_element003]
  conduct = 2
  density = 1
  expand = 3
  formula = G4_LITHIUM_IODIDE
  name = G4_LITHIUM_IODIDE
  specific = 4
FEATURE [App::DocumentObjectGroupPython] Li_element006  label="Li_element : 006"  # scripted group (container) (typed FeaturePython)
  n = 2
  ref = Li_element
FEATURE [App::DocumentObjectGroupPython] O_element055  label="O_element : 029"  # scripted group (container) (typed FeaturePython)
  n = 1
  ref = O_element
FEATURE [App::DocumentObjectGroupPython] G4_LITHIUM_OXIDE  # scripted group (container) (typed FeaturePython)
  Dunit = g/cm3
  Dvalue = 2.013
  Group = -> [Li_element006,O_element055]
  conduct = 2
  density = 1
  expand = 3
  formula = G4_LITHIUM_OXIDE
  name = G4_LITHIUM_OXIDE
  specific = 4
FEATURE [App::DocumentObjectGroupPython] Li_element007  label="Li_element : 007"  # scripted group (container) (typed FeaturePython)
  n = 2
  ref = Li_element
FEATURE [App::DocumentObjectGroupPython] B_element005  label="B_element : 005"  # scripted group (container) (typed FeaturePython)
  n = 4
  ref = B_element
FEATURE [App::DocumentObjectGroupPython] O_element056  label="O_element : 7"  # scripted group (container) (typed FeaturePython)
  n = 7
  ref = O_element
FEATURE [App::DocumentObjectGroupPython] G4_LITHIUM_TETRABORATE  # scripted group (container) (typed FeaturePython)
  Dunit = g/cm3
  Dvalue = 2.44
  Group = -> [Li_element007,B_element005,O_element056]
  conduct = 2
  density = 1
  expand = 3
  formula = G4_LITHIUM_TETRABORATE
  name = G4_LITHIUM_TETRABORATE
  specific = 4
FEATURE [App::DocumentObjectGroupPython] H_element051  label="H_element : 0.105"  # scripted group (container) (typed FeaturePython)
  n = 0.105
FEATURE [App::DocumentObjectGroupPython] C_element056  label="C_element : 0.083"  # scripted group (container) (typed FeaturePython)
  n = 0.083
FEATURE [App::DocumentObjectGroupPython] N_element023  label="N_element : 0.023"  # scripted group (container) (typed FeaturePython)
  n = 0.023
FEATURE [App::DocumentObjectGroupPython] O_element057  label="O_element : 0.779"  # scripted group (container) (typed FeaturePython)
  n = 0.779
FEATURE [App::DocumentObjectGroupPython] Na_element010  label="Na_element : 0.097"  # scripted group (container) (typed FeaturePython)
  n = 0.002
FEATURE [App::DocumentObjectGroupPython] P_element006  label="P_element : 0.105"  # scripted group (container) (typed FeaturePython)
  n = 0.001
FEATURE [App::DocumentObjectGroupPython] S_element016  label="S_element : 0.017"  # scripted group (container) (typed FeaturePython)
  n = 0.002
FEATURE [App::DocumentObjectGroupPython] Cl_element014  label="Cl_element : 0.587"  # scripted group (container) (typed FeaturePython)
  n = 0.003
FEATURE [App::DocumentObjectGroupPython] K_element005  label="K_element : 0.015"  # scripted group (container) (typed FeaturePython)
  n = 0.002
FEATURE [App::DocumentObjectGroupPython] G4_LUNG_ICRP  # scripted group (container) (typed FeaturePython)
  Dunit = g/cm3
  Dvalue = 1.04
  Group = -> [H_element051,C_element056,N_element023,O_element057,Na_element010,P_element006,S_element016,Cl_element014,K_element005]
  conduct = 2
  density = 1
  expand = 3
  formula = G4_LUNG_ICRP
  name = G4_LUNG_ICRP
  specific = 4
FEATURE [App::DocumentObjectGroupPython] H_element052  label="H_element : 0.116"  # scripted group (container) (typed FeaturePython)
  n = 0.114318
FEATURE [App::DocumentObjectGroupPython] C_element057  label="C_element : 0.656"  # scripted group (container) (typed FeaturePython)
  n = 0.655824
FEATURE [App::DocumentObjectGroupPython] O_element058  label="O_element : 0.092"  # scripted group (container) (typed FeaturePython)
  n = 0.0921831
FEATURE [App::DocumentObjectGroupPython] Mg_element004  label="Mg_element : 0.135"  # scripted group (container) (typed FeaturePython)
  n = 0.134792
FEATURE [App::DocumentObjectGroupPython] Ca_element013  label="Ca_element : 0.003"  # scripted group (container) (typed FeaturePython)
  n = 0.002883
FEATURE [App::DocumentObjectGroupPython] G4_M3_WAX  # scripted group (container) (typed FeaturePython)
  Dunit = g/cm3
  Dvalue = 1.05
  Group = -> [H_element052,C_element057,O_element058,Mg_element004,Ca_element013]
  conduct = 2
  density = 1
  expand = 3
  formula = G4_M3_WAX
  name = G4_M3_WAX
  specific = 4
FEATURE [App::DocumentObjectGroupPython] Mg_element005  label="Mg_element : 1"  # scripted group (container) (typed FeaturePython)
  n = 1
  ref = Mg_element
FEATURE [App::DocumentObjectGroupPython] C_element058  label="C_element : 031"  # scripted group (container) (typed FeaturePython)
  n = 1
  ref = C_element
FEATURE [App::DocumentObjectGroupPython] O_element059  label="O_element : 030"  # scripted group (container) (typed FeaturePython)
  n = 3
  ref = O_element
FEATURE [App::DocumentObjectGroupPython] G4_MAGNESIUM_CARBONATE  # scripted group (container) (typed FeaturePython)
  Dunit = g/cm3
  Dvalue = 2.958
  Group = -> [Mg_element005,C_element058,O_element059]
  conduct = 2
  density = 1
  expand = 3
  formula = G4_MAGNESIUM_CARBONATE
  name = G4_MAGNESIUM_CARBONATE
  specific = 4
FEATURE [App::DocumentObjectGroupPython] Mg_element006  label="Mg_element : 002"  # scripted group (container) (typed FeaturePython)
  n = 1
  ref = Mg_element
FEATURE [App::DocumentObjectGroupPython] F_element013  label="F_element : 005"  # scripted group (container) (typed FeaturePython)
  n = 2
  ref = F_element
FEATURE [App::DocumentObjectGroupPython] G4_MAGNESIUM_FLUORIDE  # scripted group (container) (typed FeaturePython)
  Dunit = g/cm3
  Dvalue = 3
  Group = -> [Mg_element006,F_element013]
  conduct = 2
  density = 1
  expand = 3
  formula = G4_MAGNESIUM_FLUORIDE
  name = G4_MAGNESIUM_FLUORIDE
  specific = 4
FEATURE [App::DocumentObjectGroupPython] Mg_element007  label="Mg_element : 003"  # scripted group (container) (typed FeaturePython)
  n = 1
  ref = Mg_element
FEATURE [App::DocumentObjectGroupPython] O_element060  label="O_element : 031"  # scripted group (container) (typed FeaturePython)
  n = 1
  ref = O_element
FEATURE [App::DocumentObjectGroupPython] G4_MAGNESIUM_OXIDE  # scripted group (container) (typed FeaturePython)
  Dunit = g/cm3
  Dvalue = 3.58
  Group = -> [Mg_element007,O_element060]
  conduct = 2
  density = 1
  expand = 3
  formula = G4_MAGNESIUM_OXIDE
  name = G4_MAGNESIUM_OXIDE
  specific = 4
FEATURE [App::DocumentObjectGroupPython] Mg_element008  label="Mg_element : 004"  # scripted group (container) (typed FeaturePython)
  n = 1
  ref = Mg_element
FEATURE [App::DocumentObjectGroupPython] B_element006  label="B_element : 006"  # scripted group (container) (typed FeaturePython)
  n = 4
  ref = B_element
FEATURE [App::DocumentObjectGroupPython] O_element061  label="O_element : 032"  # scripted group (container) (typed FeaturePython)
  n = 7
  ref = O_element
FEATURE [App::DocumentObjectGroupPython] G4_MAGNESIUM_TETRABORATE  # scripted group (container) (typed FeaturePython)
  Dunit = g/cm3
  Dvalue = 2.53
  Group = -> [Mg_element008,B_element006,O_element061]
  conduct = 2
  density = 1
  expand = 3
  formula = G4_MAGNESIUM_TETRABORATE
  name = G4_MAGNESIUM_TETRABORATE
  specific = 4
FEATURE [App::DocumentObjectGroupPython] Hg_element001  label="Hg_element : 1"  # scripted group (container) (typed FeaturePython)
  n = 1
  ref = Hg_element
FEATURE [App::DocumentObjectGroupPython] I_element004  label="I_element : 2"  # scripted group (container) (typed FeaturePython)
  n = 2
  ref = I_element
FEATURE [App::DocumentObjectGroupPython] G4_MERCURIC_IODIDE  # scripted group (container) (typed FeaturePython)
  Dunit = g/cm3
  Dvalue = 6.36
  Group = -> [Hg_element001,I_element004]
  conduct = 2
  density = 1
  expand = 3
  formula = G4_MERCURIC_IODIDE
  name = G4_MERCURIC_IODIDE
  specific = 4
FEATURE [App::DocumentObjectGroupPython] C_element059  label="C_element : 032"  # scripted group (container) (typed FeaturePython)
  n = 1
  ref = C_element
FEATURE [App::DocumentObjectGroupPython] H_element053  label="H_element : 028"  # scripted group (container) (typed FeaturePython)
  n = 4
  ref = H_element
FEATURE [App::DocumentObjectGroupPython] G4_METHANE  # scripted group (container) (typed FeaturePython)
  Dunit = g/cm3
  Dvalue = 0.000667151
  Group = -> [C_element059,H_element053]
  conduct = 2
  density = 1
  expand = 3
  formula = G4_METHANE
  name = G4_METHANE
  specific = 4
FEATURE [App::DocumentObjectGroupPython] C_element060  label="C_element : 033"  # scripted group (container) (typed FeaturePython)
  n = 1
  ref = C_element
FEATURE [App::DocumentObjectGroupPython] H_element054  label="H_element : 029"  # scripted group (container) (typed FeaturePython)
  n = 4
  ref = H_element
FEATURE [App::DocumentObjectGroupPython] O_element062  label="O_element : 033"  # scripted group (container) (typed FeaturePython)
  n = 1
  ref = O_element
FEATURE [App::DocumentObjectGroupPython] G4_METHANOL  # scripted group (container) (typed FeaturePython)
  Dunit = g/cm3
  Dvalue = 0.7914
  Group = -> [C_element060,H_element054,O_element062]
  conduct = 2
  density = 1
  expand = 3
  formula = G4_METHANOL
  name = G4_METHANOL
  specific = 4
FEATURE [App::DocumentObjectGroupPython] H_element055  label="H_element : 0.134"  # scripted group (container) (typed FeaturePython)
  n = 0.13404
FEATURE [App::DocumentObjectGroupPython] C_element061  label="C_element : 0.778"  # scripted group (container) (typed FeaturePython)
  n = 0.77796
FEATURE [App::DocumentObjectGroupPython] O_element063  label="O_element : 0.035"  # scripted group (container) (typed FeaturePython)
  n = 0.03502
FEATURE [App::DocumentObjectGroupPython] Mg_element009  label="Mg_element : 0.039"  # scripted group (container) (typed FeaturePython)
  n = 0.038594
FEATURE [App::DocumentObjectGroupPython] Ti_element002  label="Ti_element : 0.014"  # scripted group (container) (typed FeaturePython)
  n = 0.014386
FEATURE [App::DocumentObjectGroupPython] G4_MIX_D_WAX  # scripted group (container) (typed FeaturePython)
  Dunit = g/cm3
  Dvalue = 0.99
  Group = -> [H_element055,C_element061,O_element063,Mg_element009,Ti_element002]
  conduct = 2
  density = 1
  expand = 3
  formula = G4_MIX_D_WAX
  name = G4_MIX_D_WAX
  specific = 4
FEATURE [App::DocumentObjectGroupPython] H_element056  label="H_element : 0.135"  # scripted group (container) (typed FeaturePython)
  n = 0.081192
FEATURE [App::DocumentObjectGroupPython] C_element062  label="C_element : 0.583"  # scripted group (container) (typed FeaturePython)
  n = 0.583442
FEATURE [App::DocumentObjectGroupPython] N_element024  label="N_element : 0.018"  # scripted group (container) (typed FeaturePython)
  n = 0.017798
FEATURE [App::DocumentObjectGroupPython] O_element064  label="O_element : 0.186"  # scripted group (container) (typed FeaturePython)
  n = 0.186381
FEATURE [App::DocumentObjectGroupPython] Mg_element010  label="Mg_element : 0.130"  # scripted group (container) (typed FeaturePython)
  n = 0.130287
FEATURE [App::DocumentObjectGroupPython] Cl_element015  label="Cl_element : 0.588"  # scripted group (container) (typed FeaturePython)
  n = 0.0009
FEATURE [App::DocumentObjectGroupPython] G4_MS20_TISSUE  # scripted group (container) (typed FeaturePython)
  Dunit = g/cm3
  Dvalue = 1
  Group = -> [H_element056,C_element062,N_element024,O_element064,Mg_element010,Cl_element015]
  conduct = 2
  density = 1
  expand = 3
  formula = G4_MS20_TISSUE
  name = G4_MS20_TISSUE
  specific = 4
FEATURE [App::DocumentObjectGroupPython] H_element057  label="H_element : 0.136"  # scripted group (container) (typed FeaturePython)
  n = 0.102
FEATURE [App::DocumentObjectGroupPython] C_element063  label="C_element : 0.143"  # scripted group (container) (typed FeaturePython)
  n = 0.143
FEATURE [App::DocumentObjectGroupPython] N_element025  label="N_element : 0.034"  # scripted group (container) (typed FeaturePython)
  n = 0.034
FEATURE [App::DocumentObjectGroupPython] O_element065  label="O_element : 0.710"  # scripted group (container) (typed FeaturePython)
  n = 0.71
FEATURE [App::DocumentObjectGroupPython] Na_element011  label="Na_element : 0.098"  # scripted group (container) (typed FeaturePython)
  n = 0.001
FEATURE [App::DocumentObjectGroupPython] P_element007  label="P_element : 0.002"  # scripted group (container) (typed FeaturePython)
  n = 0.002
FEATURE [App::DocumentObjectGroupPython] S_element017  label="S_element : 0.018"  # scripted group (container) (typed FeaturePython)
  n = 0.003
FEATURE [App::DocumentObjectGroupPython] Cl_element016  label="Cl_element : 0.589"  # scripted group (container) (typed FeaturePython)
  n = 0.001
FEATURE [App::DocumentObjectGroupPython] K_element006  label="K_element : 0.004"  # scripted group (container) (typed FeaturePython)
  n = 0.004
FEATURE [App::DocumentObjectGroupPython] G4_MUSCLE_SKELETAL_ICRP  # scripted group (container) (typed FeaturePython)
  Dunit = g/cm3
  Dvalue = 1.05
  Group = -> [H_element057,C_element063,N_element025,O_element065,Na_element011,P_element007,S_element017,Cl_element016,K_element006]
  conduct = 2
  density = 1
  expand = 3
  formula = G4_MUSCLE_SKELETAL_ICRP
  name = G4_MUSCLE_SKELETAL_ICRP
  specific = 4
FEATURE [App::DocumentObjectGroupPython] H_element058  label="H_element : 0.137"  # scripted group (container) (typed FeaturePython)
  n = 0.102102
FEATURE [App::DocumentObjectGroupPython] C_element064  label="C_element : 0.123"  # scripted group (container) (typed FeaturePython)
  n = 0.123123
FEATURE [App::DocumentObjectGroupPython] N_element026  label="N_element : 0.756"  # scripted group (container) (typed FeaturePython)
  n = 0.035035
FEATURE [App::DocumentObjectGroupPython] O_element066  label="O_element : 0.730"  # scripted group (container) (typed FeaturePython)
  n = 0.72973
FEATURE [App::DocumentObjectGroupPython] Na_element012  label="Na_element : 0.099"  # scripted group (container) (typed FeaturePython)
  n = 0.001001
FEATURE [App::DocumentObjectGroupPython] P_element008  label="P_element : 0.106"  # scripted group (container) (typed FeaturePython)
  n = 0.002002
FEATURE [App::DocumentObjectGroupPython] S_element018  label="S_element : 0.019"  # scripted group (container) (typed FeaturePython)
  n = 0.004004
FEATURE [App::DocumentObjectGroupPython] K_element007  label="K_element : 0.016"  # scripted group (container) (typed FeaturePython)
  n = 0.003003
FEATURE [App::DocumentObjectGroupPython] G4_MUSCLE_STRIATED_ICRU  # scripted group (container) (typed FeaturePython)
  Dunit = g/cm3
  Dvalue = 1.04
  Group = -> [H_element058,C_element064,N_element026,O_element066,Na_element012,P_element008,S_element018,K_element007]
  conduct = 2
  density = 1
  expand = 3
  formula = G4_MUSCLE_STRIATED_ICRU
  name = G4_MUSCLE_STRIATED_ICRU
  specific = 4
FEATURE [App::DocumentObjectGroupPython] H_element059  label="H_element : 0.098"  # scripted group (container) (typed FeaturePython)
  n = 0.0982341
FEATURE [App::DocumentObjectGroupPython] C_element065  label="C_element : 0.156"  # scripted group (container) (typed FeaturePython)
  n = 0.156214
FEATURE [App::DocumentObjectGroupPython] N_element027  label="N_element : 0.757"  # scripted group (container) (typed FeaturePython)
  n = 0.035451
FEATURE [App::DocumentObjectGroupPython] O_element067  label="O_element : 0.880"  # scripted group (container) (typed FeaturePython)
  n = 0.710101
FEATURE [App::DocumentObjectGroupPython] G4_MUSCLE_WITH_SUCROSE  # scripted group (container) (typed FeaturePython)
  Dunit = g/cm3
  Dvalue = 1.11
  Group = -> [H_element059,C_element065,N_element027,O_element067]
  conduct = 2
  density = 1
  expand = 3
  formula = G4_MUSCLE_WITH_SUCROSE
  name = G4_MUSCLE_WITH_SUCROSE
  specific = 4
FEATURE [App::DocumentObjectGroupPython] H_element060  label="H_element : 0.138"  # scripted group (container) (typed FeaturePython)
  n = 0.101969
FEATURE [App::DocumentObjectGroupPython] C_element066  label="C_element : 0.120"  # scripted group (container) (typed FeaturePython)
  n = 0.120058
FEATURE [App::DocumentObjectGroupPython] N_element028  label="N_element : 0.758"  # scripted group (container) (typed FeaturePython)
  n = 0.035451
FEATURE [App::DocumentObjectGroupPython] O_element068  label="O_element : 0.743"  # scripted group (container) (typed FeaturePython)
  n = 0.742522
FEATURE [App::DocumentObjectGroupPython] G4_MUSCLE_WITHOUT_SUCROSE  # scripted group (container) (typed FeaturePython)
  Dunit = g/cm3
  Dvalue = 1.07
  Group = -> [H_element060,C_element066,N_element028,O_element068]
  conduct = 2
  density = 1
  expand = 3
  formula = G4_MUSCLE_WITHOUT_SUCROSE
  name = G4_MUSCLE_WITHOUT_SUCROSE
  specific = 4
FEATURE [App::DocumentObjectGroupPython] C_element067  label="C_element : 10"  # scripted group (container) (typed FeaturePython)
  n = 10
  ref = C_element
FEATURE [App::DocumentObjectGroupPython] H_element061  label="H_element : 030"  # scripted group (container) (typed FeaturePython)
  n = 8
  ref = H_element
FEATURE [App::DocumentObjectGroupPython] G4_NAPHTHALENE  # scripted group (container) (typed FeaturePython)
  Dunit = g/cm3
  Dvalue = 1.145
  Group = -> [C_element067,H_element061]
  conduct = 2
  density = 1
  expand = 3
  formula = G4_NAPHTHALENE
  name = G4_NAPHTHALENE
  specific = 4
FEATURE [App::DocumentObjectGroupPython] C_element068  label="C_element : 034"  # scripted group (container) (typed FeaturePython)
  n = 6
  ref = C_element
FEATURE [App::DocumentObjectGroupPython] H_element062  label="H_element : 031"  # scripted group (container) (typed FeaturePython)
  n = 5
  ref = H_element
FEATURE [App::DocumentObjectGroupPython] N_element029  label="N_element : 012"  # scripted group (container) (typed FeaturePython)
  n = 1
  ref = N_element
FEATURE [App::DocumentObjectGroupPython] O_element069  label="O_element : 034"  # scripted group (container) (typed FeaturePython)
  n = 2
  ref = O_element
FEATURE [App::DocumentObjectGroupPython] G4_NITROBENZENE  # scripted group (container) (typed FeaturePython)
  Dunit = g/cm3
  Dvalue = 1.19867
  Group = -> [C_element068,H_element062,N_element029,O_element069]
  conduct = 2
  density = 1
  expand = 3
  formula = G4_NITROBENZENE
  name = G4_NITROBENZENE
  specific = 4
FEATURE [App::DocumentObjectGroupPython] N_element030  label="N_element : 013"  # scripted group (container) (typed FeaturePython)
  n = 2
  ref = N_element
FEATURE [App::DocumentObjectGroupPython] O_element070  label="O_element : 035"  # scripted group (container) (typed FeaturePython)
  n = 1
  ref = O_element
FEATURE [App::DocumentObjectGroupPython] G4_NITROUS_OXIDE  # scripted group (container) (typed FeaturePython)
  Dunit = g/cm3
  Dvalue = 0.00183094
  Group = -> [N_element030,O_element070]
  conduct = 2
  density = 1
  expand = 3
  formula = G4_NITROUS_OXIDE
  name = G4_NITROUS_OXIDE
  specific = 4
FEATURE [App::DocumentObjectGroupPython] H_element063  label="H_element : 0.104"  # scripted group (container) (typed FeaturePython)
  n = 0.103509
FEATURE [App::DocumentObjectGroupPython] C_element069  label="C_element : 0.648"  # scripted group (container) (typed FeaturePython)
  n = 0.648416
FEATURE [App::DocumentObjectGroupPython] N_element031  label="N_element : 0.100"  # scripted group (container) (typed FeaturePython)
  n = 0.0995361
FEATURE [App::DocumentObjectGroupPython] O_element071  label="O_element : 0.149"  # scripted group (container) (typed FeaturePython)
  n = 0.148539
FEATURE [App::DocumentObjectGroupPython] G4_NYLON_8062  label="G4_NYLON-8062"  # scripted group (container) (typed FeaturePython)
  Dunit = g/cm3
  Dvalue = 1.08
  Group = -> [H_element063,C_element069,N_element031,O_element071]
  conduct = 2
  density = 1
  expand = 3
  formula = G4_NYLON-8062
  name = G4_NYLON-8062
  specific = 4
FEATURE [App::DocumentObjectGroupPython] C_element070  label="C_element : 035"  # scripted group (container) (typed FeaturePython)
  n = 6
  ref = C_element
FEATURE [App::DocumentObjectGroupPython] H_element064  label="H_element : 11"  # scripted group (container) (typed FeaturePython)
  n = 11
  ref = H_element
FEATURE [App::DocumentObjectGroupPython] N_element032  label="N_element : 014"  # scripted group (container) (typed FeaturePython)
  n = 1
  ref = N_element
FEATURE [App::DocumentObjectGroupPython] O_element072  label="O_element : 036"  # scripted group (container) (typed FeaturePython)
  n = 1
  ref = O_element
FEATURE [App::DocumentObjectGroupPython] G4_NYLON_6_6  label="G4_NYLON-6-6"  # scripted group (container) (typed FeaturePython)
  Dunit = g/cm3
  Dvalue = 1.14
  Group = -> [C_element070,H_element064,N_element032,O_element072]
  conduct = 2
  density = 1
  expand = 3
  formula = G4_NYLON-6-6
  name = G4_NYLON-6-6
  specific = 4
FEATURE [App::DocumentObjectGroupPython] H_element065  label="H_element : 0.139"  # scripted group (container) (typed FeaturePython)
  n = 0.107062
FEATURE [App::DocumentObjectGroupPython] C_element071  label="C_element : 0.680"  # scripted group (container) (typed FeaturePython)
  n = 0.680449
FEATURE [App::DocumentObjectGroupPython] N_element033  label="N_element : 0.099"  # scripted group (container) (typed FeaturePython)
  n = 0.099189
FEATURE [App::DocumentObjectGroupPython] O_element073  label="O_element : 0.113"  # scripted group (container) (typed FeaturePython)
  n = 0.1133
FEATURE [App::DocumentObjectGroupPython] G4_NYLON_6_10  label="G4_NYLON-6-10"  # scripted group (container) (typed FeaturePython)
  Dunit = g/cm3
  Dvalue = 1.14
  Group = -> [H_element065,C_element071,N_element033,O_element073]
  conduct = 2
  density = 1
  expand = 3
  formula = G4_NYLON-6-10
  name = G4_NYLON-6-10
  specific = 4
FEATURE [App::DocumentObjectGroupPython] H_element066  label="H_element : 0.140"  # scripted group (container) (typed FeaturePython)
  n = 0.115476
FEATURE [App::DocumentObjectGroupPython] C_element072  label="C_element : 0.721"  # scripted group (container) (typed FeaturePython)
  n = 0.720818
FEATURE [App::DocumentObjectGroupPython] N_element034  label="N_element : 0.076"  # scripted group (container) (typed FeaturePython)
  n = 0.0764169
FEATURE [App::DocumentObjectGroupPython] O_element074  label="O_element : 0.087"  # scripted group (container) (typed FeaturePython)
  n = 0.0872889
FEATURE [App::DocumentObjectGroupPython] G4_NYLON_11_RILSAN  label="G4_NYLON-11_RILSAN"  # scripted group (container) (typed FeaturePython)
  Dunit = g/cm3
  Dvalue = 1.425
  Group = -> [H_element066,C_element072,N_element034,O_element074]
  conduct = 2
  density = 1
  expand = 3
  formula = G4_NYLON-11_RILSAN
  name = G4_NYLON-11_RILSAN
  specific = 4
FEATURE [App::DocumentObjectGroupPython] C_element073  label="C_element : 8"  # scripted group (container) (typed FeaturePython)
  n = 8
  ref = C_element
FEATURE [App::DocumentObjectGroupPython] H_element067  label="H_element : 18"  # scripted group (container) (typed FeaturePython)
  n = 18
  ref = H_element
FEATURE [App::DocumentObjectGroupPython] G4_OCTANE  # scripted group (container) (typed FeaturePython)
  Dunit = g/cm3
  Dvalue = 0.7026
  Group = -> [C_element073,H_element067]
  conduct = 2
  density = 1
  expand = 3
  formula = G4_OCTANE
  name = G4_OCTANE
  specific = 4
FEATURE [App::DocumentObjectGroupPython] C_element074  label="C_element : 25"  # scripted group (container) (typed FeaturePython)
  n = 25
  ref = C_element
FEATURE [App::DocumentObjectGroupPython] H_element068  label="H_element : 52"  # scripted group (container) (typed FeaturePython)
  n = 52
  ref = H_element
FEATURE [App::DocumentObjectGroupPython] G4_PARAFFIN  # scripted group (container) (typed FeaturePython)
  Dunit = g/cm3
  Dvalue = 0.93
  Group = -> [C_element074,H_element068]
  conduct = 2
  density = 1
  expand = 3
  formula = G4_PARAFFIN
  name = G4_PARAFFIN
  specific = 4
FEATURE [App::DocumentObjectGroupPython] C_element075  label="C_element : 036"  # scripted group (container) (typed FeaturePython)
  n = 5
  ref = C_element
FEATURE [App::DocumentObjectGroupPython] H_element069  label="H_element : 032"  # scripted group (container) (typed FeaturePython)
  n = 12
  ref = H_element
FEATURE [App::DocumentObjectGroupPython] G4_N_PENTANE  label="G4_N-PENTANE"  # scripted group (container) (typed FeaturePython)
  Dunit = g/cm3
  Dvalue = 0.6262
  Group = -> [C_element075,H_element069]
  conduct = 2
  density = 1
  expand = 3
  formula = G4_N-PENTANE
  name = G4_N-PENTANE
  specific = 4
FEATURE [App::DocumentObjectGroupPython] H_element070  label="H_element : 0.014"  # scripted group (container) (typed FeaturePython)
  n = 0.0141
FEATURE [App::DocumentObjectGroupPython] C_element076  label="C_element : 0.072"  # scripted group (container) (typed FeaturePython)
  n = 0.072261
FEATURE [App::DocumentObjectGroupPython] N_element035  label="N_element : 0.019"  # scripted group (container) (typed FeaturePython)
  n = 0.01932
FEATURE [App::DocumentObjectGroupPython] O_element075  label="O_element : 0.066"  # scripted group (container) (typed FeaturePython)
  n = 0.066101
FEATURE [App::DocumentObjectGroupPython] S_element019  label="S_element : 0.020"  # scripted group (container) (typed FeaturePython)
  n = 0.00189
FEATURE [App::DocumentObjectGroupPython] Br_element004  label="Br_element : 0.349"  # scripted group (container) (typed FeaturePython)
  n = 0.349103
FEATURE [App::DocumentObjectGroupPython] Ag_element001  label="Ag_element : 0.474"  # scripted group (container) (typed FeaturePython)
  n = 0.474105
FEATURE [App::DocumentObjectGroupPython] I_element005  label="I_element : 0.003"  # scripted group (container) (typed FeaturePython)
  n = 0.00312
FEATURE [App::DocumentObjectGroupPython] G4_PHOTO_EMULSION  # scripted group (container) (typed FeaturePython)
  Dunit = g/cm3
  Dvalue = 3.815
  Group = -> [H_element070,C_element076,N_element035,O_element075,S_element019,Br_element004,Ag_element001,I_element005]
  conduct = 2
  density = 1
  expand = 3
  formula = G4_PHOTO_EMULSION
  name = G4_PHOTO_EMULSION
  specific = 4
FEATURE [App::DocumentObjectGroupPython] C_element077  label="C_element : 9"  # scripted group (container) (typed FeaturePython)
  n = 9
  ref = C_element
FEATURE [App::DocumentObjectGroupPython] H_element071  label="H_element : 033"  # scripted group (container) (typed FeaturePython)
  n = 10
  ref = H_element
FEATURE [App::DocumentObjectGroupPython] G4_PLASTIC_SC_VINYLTOLUENE  # scripted group (container) (typed FeaturePython)
  Dunit = g/cm3
  Dvalue = 1.032
  Group = -> [C_element077,H_element071]
  conduct = 2
  density = 1
  expand = 3
  formula = G4_PLASTIC_SC_VINYLTOLUENE
  name = G4_PLASTIC_SC_VINYLTOLUENE
  specific = 4
FEATURE [App::DocumentObjectGroupPython] Pu_element001  label="Pu_element : 1"  # scripted group (container) (typed FeaturePython)
  n = 1
  ref = Pu_element
FEATURE [App::DocumentObjectGroupPython] O_element076  label="O_element : 037"  # scripted group (container) (typed FeaturePython)
  n = 2
  ref = O_element
FEATURE [App::DocumentObjectGroupPython] G4_PLUTONIUM_DIOXIDE  # scripted group (container) (typed FeaturePython)
  Dunit = g/cm3
  Dvalue = 11.46
  Group = -> [Pu_element001,O_element076]
  conduct = 2
  density = 1
  expand = 3
  formula = G4_PLUTONIUM_DIOXIDE
  name = G4_PLUTONIUM_DIOXIDE
  specific = 4
FEATURE [App::DocumentObjectGroupPython] C_element078  label="C_element : 037"  # scripted group (container) (typed FeaturePython)
  n = 3
  ref = C_element
FEATURE [App::DocumentObjectGroupPython] H_element072  label="H_element : 034"  # scripted group (container) (typed FeaturePython)
  n = 3
  ref = H_element
FEATURE [App::DocumentObjectGroupPython] N_element036  label="N_element : 015"  # scripted group (container) (typed FeaturePython)
  n = 1
  ref = N_element
FEATURE [App::DocumentObjectGroupPython] G4_POLYACRYLONITRILE  # scripted group (container) (typed FeaturePython)
  Dunit = g/cm3
  Dvalue = 1.17
  Group = -> [C_element078,H_element072,N_element036]
  conduct = 2
  density = 1
  expand = 3
  formula = G4_POLYACRYLONITRILE
  name = G4_POLYACRYLONITRILE
  specific = 4
FEATURE [App::DocumentObjectGroupPython] C_element079  label="C_element : 16"  # scripted group (container) (typed FeaturePython)
  n = 16
  ref = C_element
FEATURE [App::DocumentObjectGroupPython] H_element073  label="H_element : 035"  # scripted group (container) (typed FeaturePython)
  n = 14
  ref = H_element
FEATURE [App::DocumentObjectGroupPython] O_element077  label="O_element : 038"  # scripted group (container) (typed FeaturePython)
  n = 3
  ref = O_element
FEATURE [App::DocumentObjectGroupPython] G4_POLYCARBONATE  # scripted group (container) (typed FeaturePython)
  Dunit = g/cm3
  Dvalue = 1.2
  Group = -> [C_element079,H_element073,O_element077]
  conduct = 2
  density = 1
  expand = 3
  formula = G4_POLYCARBONATE
  name = G4_POLYCARBONATE
  specific = 4
FEATURE [App::DocumentObjectGroupPython] C_element080  label="C_element : 038"  # scripted group (container) (typed FeaturePython)
  n = 8
  ref = C_element
FEATURE [App::DocumentObjectGroupPython] H_element074  label="H_element : 036"  # scripted group (container) (typed FeaturePython)
  n = 7
  ref = H_element
FEATURE [App::DocumentObjectGroupPython] Cl_element017  label="Cl_element : 007"  # scripted group (container) (typed FeaturePython)
  n = 1
  ref = Cl_element
FEATURE [App::DocumentObjectGroupPython] G4_POLYCHLOROSTYRENE  # scripted group (container) (typed FeaturePython)
  Dunit = g/cm3
  Dvalue = 1.3
  Group = -> [C_element080,H_element074,Cl_element017]
  conduct = 2
  density = 1
  expand = 3
  formula = G4_POLYCHLOROSTYRENE
  name = G4_POLYCHLOROSTYRENE
  specific = 4
FEATURE [App::DocumentObjectGroupPython] C_element081  label="C_element : 039"  # scripted group (container) (typed FeaturePython)
  n = 1
  ref = C_element
FEATURE [App::DocumentObjectGroupPython] H_element075  label="H_element : 037"  # scripted group (container) (typed FeaturePython)
  n = 2
  ref = H_element
FEATURE [App::DocumentObjectGroupPython] G4_POLYETHYLENE  # scripted group (container) (typed FeaturePython)
  Dunit = g/cm3
  Dvalue = 0.94
  Group = -> [C_element081,H_element075]
  conduct = 2
  density = 1
  expand = 3
  formula = G4_POLYETHYLENE
  name = G4_POLYETHYLENE
  specific = 4
FEATURE [App::DocumentObjectGroupPython] C_element082  label="C_element : 040"  # scripted group (container) (typed FeaturePython)
  n = 10
  ref = C_element
FEATURE [App::DocumentObjectGroupPython] H_element076  label="H_element : 038"  # scripted group (container) (typed FeaturePython)
  n = 8
  ref = H_element
FEATURE [App::DocumentObjectGroupPython] O_element078  label="O_element : 039"  # scripted group (container) (typed FeaturePython)
  n = 4
  ref = O_element
FEATURE [App::DocumentObjectGroupPython] G4_MYLAR  # scripted group (container) (typed FeaturePython)
  Dunit = g/cm3
  Dvalue = 1.4
  Group = -> [C_element082,H_element076,O_element078]
  conduct = 2
  density = 1
  expand = 3
  formula = G4_MYLAR
  name = G4_MYLAR
  specific = 4
FEATURE [App::DocumentObjectGroupPython] C_element083  label="C_element : 041"  # scripted group (container) (typed FeaturePython)
  n = 5
  ref = C_element
FEATURE [App::DocumentObjectGroupPython] H_element077  label="H_element : 039"  # scripted group (container) (typed FeaturePython)
  n = 8
  ref = H_element
FEATURE [App::DocumentObjectGroupPython] O_element079  label="O_element : 040"  # scripted group (container) (typed FeaturePython)
  n = 2
  ref = O_element
FEATURE [App::DocumentObjectGroupPython] G4_PLEXIGLASS  # scripted group (container) (typed FeaturePython)
  Dunit = g/cm3
  Dvalue = 1.19
  Group = -> [C_element083,H_element077,O_element079]
  conduct = 2
  density = 1
  expand = 3
  formula = G4_PLEXIGLASS
  name = G4_PLEXIGLASS
  specific = 4
FEATURE [App::DocumentObjectGroupPython] C_element084  label="C_element : 042"  # scripted group (container) (typed FeaturePython)
  n = 1
  ref = C_element
FEATURE [App::DocumentObjectGroupPython] H_element078  label="H_element : 040"  # scripted group (container) (typed FeaturePython)
  n = 2
  ref = H_element
FEATURE [App::DocumentObjectGroupPython] O_element080  label="O_element : 041"  # scripted group (container) (typed FeaturePython)
  n = 1
  ref = O_element
FEATURE [App::DocumentObjectGroupPython] G4_POLYOXYMETHYLENE  # scripted group (container) (typed FeaturePython)
  Dunit = g/cm3
  Dvalue = 1.425
  Group = -> [C_element084,H_element078,O_element080]
  conduct = 2
  density = 1
  expand = 3
  formula = G4_POLYOXYMETHYLENE
  name = G4_POLYOXYMETHYLENE
  specific = 4
FEATURE [App::DocumentObjectGroupPython] C_element085  label="C_element : 043"  # scripted group (container) (typed FeaturePython)
  n = 2
  ref = C_element
FEATURE [App::DocumentObjectGroupPython] H_element079  label="H_element : 041"  # scripted group (container) (typed FeaturePython)
  n = 4
  ref = H_element
FEATURE [App::DocumentObjectGroupPython] G4_POLYPROPYLENE  # scripted group (container) (typed FeaturePython)
  Dunit = g/cm3
  Dvalue = 0.9
  Group = -> [C_element085,H_element079]
  conduct = 2
  density = 1
  expand = 3
  formula = G4_POLYPROPYLENE
  name = G4_POLYPROPYLENE
  specific = 4
FEATURE [App::DocumentObjectGroupPython] C_element086  label="C_element : 044"  # scripted group (container) (typed FeaturePython)
  n = 8
  ref = C_element
FEATURE [App::DocumentObjectGroupPython] H_element080  label="H_element : 042"  # scripted group (container) (typed FeaturePython)
  n = 8
  ref = H_element
FEATURE [App::DocumentObjectGroupPython] G4_POLYSTYRENE  # scripted group (container) (typed FeaturePython)
  Dunit = g/cm3
  Dvalue = 1.06
  Group = -> [C_element086,H_element080]
  conduct = 2
  density = 1
  expand = 3
  formula = G4_POLYSTYRENE
  name = G4_POLYSTYRENE
  specific = 4
FEATURE [App::DocumentObjectGroupPython] C_element087  label="C_element : 045"  # scripted group (container) (typed FeaturePython)
  n = 2
  ref = C_element
FEATURE [App::DocumentObjectGroupPython] F_element014  label="F_element : 4"  # scripted group (container) (typed FeaturePython)
  n = 4
  ref = F_element
FEATURE [App::DocumentObjectGroupPython] G4_TEFLON  # scripted group (container) (typed FeaturePython)
  Dunit = g/cm3
  Dvalue = 2.2
  Group = -> [C_element087,F_element014]
  conduct = 2
  density = 1
  expand = 3
  formula = G4_TEFLON
  name = G4_TEFLON
  specific = 4
FEATURE [App::DocumentObjectGroupPython] C_element088  label="C_element : 046"  # scripted group (container) (typed FeaturePython)
  n = 2
  ref = C_element
FEATURE [App::DocumentObjectGroupPython] F_element015  label="F_element : 006"  # scripted group (container) (typed FeaturePython)
  n = 3
  ref = F_element
FEATURE [App::DocumentObjectGroupPython] Cl_element018  label="Cl_element : 008"  # scripted group (container) (typed FeaturePython)
  n = 1
  ref = Cl_element
FEATURE [App::DocumentObjectGroupPython] G4_POLYTRIFLUOROCHLOROETHYLENE  # scripted group (container) (typed FeaturePython)
  Dunit = g/cm3
  Dvalue = 2.1
  Group = -> [C_element088,F_element015,Cl_element018]
  conduct = 2
  density = 1
  expand = 3
  formula = G4_POLYTRIFLUOROCHLOROETHYLENE
  name = G4_POLYTRIFLUOROCHLOROETHYLENE
  specific = 4
FEATURE [App::DocumentObjectGroupPython] C_element089  label="C_element : 047"  # scripted group (container) (typed FeaturePython)
  n = 4
  ref = C_element
FEATURE [App::DocumentObjectGroupPython] H_element081  label="H_element : 043"  # scripted group (container) (typed FeaturePython)
  n = 6
  ref = H_element
FEATURE [App::DocumentObjectGroupPython] O_element081  label="O_element : 042"  # scripted group (container) (typed FeaturePython)
  n = 2
  ref = O_element
FEATURE [App::DocumentObjectGroupPython] G4_POLYVINYL_ACETATE  # scripted group (container) (typed FeaturePython)
  Dunit = g/cm3
  Dvalue = 1.19
  Group = -> [C_element089,H_element081,O_element081]
  conduct = 2
  density = 1
  expand = 3
  formula = G4_POLYVINYL_ACETATE
  name = G4_POLYVINYL_ACETATE
  specific = 4
FEATURE [App::DocumentObjectGroupPython] C_element090  label="C_element : 048"  # scripted group (container) (typed FeaturePython)
  n = 2
  ref = C_element
FEATURE [App::DocumentObjectGroupPython] H_element082  label="H_element : 044"  # scripted group (container) (typed FeaturePython)
  n = 4
  ref = H_element
FEATURE [App::DocumentObjectGroupPython] O_element082  label="O_element : 043"  # scripted group (container) (typed FeaturePython)
  n = 1
  ref = O_element
FEATURE [App::DocumentObjectGroupPython] G4_POLYVINYL_ALCOHOL  # scripted group (container) (typed FeaturePython)
  Dunit = g/cm3
  Dvalue = 1.3
  Group = -> [C_element090,H_element082,O_element082]
  conduct = 2
  density = 1
  expand = 3
  formula = G4_POLYVINYL_ALCOHOL
  name = G4_POLYVINYL_ALCOHOL
  specific = 4
FEATURE [App::DocumentObjectGroupPython] C_element091  label="C_element : 049"  # scripted group (container) (typed FeaturePython)
  n = 8
  ref = C_element
FEATURE [App::DocumentObjectGroupPython] H_element083  label="H_element : 045"  # scripted group (container) (typed FeaturePython)
  n = 14
  ref = H_element
FEATURE [App::DocumentObjectGroupPython] O_element083  label="O_element : 044"  # scripted group (container) (typed FeaturePython)
  n = 2
  ref = O_element
FEATURE [App::DocumentObjectGroupPython] G4_POLYVINYL_BUTYRAL  # scripted group (container) (typed FeaturePython)
  Dunit = g/cm3
  Dvalue = 1.12
  Group = -> [C_element091,H_element083,O_element083]
  conduct = 2
  density = 1
  expand = 3
  formula = G4_POLYVINYL_BUTYRAL
  name = G4_POLYVINYL_BUTYRAL
  specific = 4
FEATURE [App::DocumentObjectGroupPython] C_element092  label="C_element : 050"  # scripted group (container) (typed FeaturePython)
  n = 2
  ref = C_element
FEATURE [App::DocumentObjectGroupPython] H_element084  label="H_element : 046"  # scripted group (container) (typed FeaturePython)
  n = 3
  ref = H_element
FEATURE [App::DocumentObjectGroupPython] Cl_element019  label="Cl_element : 009"  # scripted group (container) (typed FeaturePython)
  n = 1
  ref = Cl_element
FEATURE [App::DocumentObjectGroupPython] G4_POLYVINYL_CHLORIDE  # scripted group (container) (typed FeaturePython)
  Dunit = g/cm3
  Dvalue = 1.3
  Group = -> [C_element092,H_element084,Cl_element019]
  conduct = 2
  density = 1
  expand = 3
  formula = G4_POLYVINYL_CHLORIDE
  name = G4_POLYVINYL_CHLORIDE
  specific = 4
FEATURE [App::DocumentObjectGroupPython] C_element093  label="C_element : 051"  # scripted group (container) (typed FeaturePython)
  n = 2
  ref = C_element
FEATURE [App::DocumentObjectGroupPython] H_element085  label="H_element : 047"  # scripted group (container) (typed FeaturePython)
  n = 2
  ref = H_element
FEATURE [App::DocumentObjectGroupPython] Cl_element020  label="Cl_element : 010"  # scripted group (container) (typed FeaturePython)
  n = 2
  ref = Cl_element
FEATURE [App::DocumentObjectGroupPython] G4_POLYVINYLIDENE_CHLORIDE  # scripted group (container) (typed FeaturePython)
  Dunit = g/cm3
  Dvalue = 1.7
  Group = -> [C_element093,H_element085,Cl_element020]
  conduct = 2
  density = 1
  expand = 3
  formula = G4_POLYVINYLIDENE_CHLORIDE
  name = G4_POLYVINYLIDENE_CHLORIDE
  specific = 4
FEATURE [App::DocumentObjectGroupPython] C_element094  label="C_element : 052"  # scripted group (container) (typed FeaturePython)
  n = 2
  ref = C_element
FEATURE [App::DocumentObjectGroupPython] H_element086  label="H_element : 048"  # scripted group (container) (typed FeaturePython)
  n = 2
  ref = H_element
FEATURE [App::DocumentObjectGroupPython] F_element016  label="F_element : 007"  # scripted group (container) (typed FeaturePython)
  n = 2
  ref = F_element
FEATURE [App::DocumentObjectGroupPython] G4_POLYVINYLIDENE_FLUORIDE  # scripted group (container) (typed FeaturePython)
  Dunit = g/cm3
  Dvalue = 1.76
  Group = -> [C_element094,H_element086,F_element016]
  conduct = 2
  density = 1
  expand = 3
  formula = G4_POLYVINYLIDENE_FLUORIDE
  name = G4_POLYVINYLIDENE_FLUORIDE
  specific = 4
FEATURE [App::DocumentObjectGroupPython] C_element095  label="C_element : 053"  # scripted group (container) (typed FeaturePython)
  n = 6
  ref = C_element
FEATURE [App::DocumentObjectGroupPython] H_element087  label="H_element : 9"  # scripted group (container) (typed FeaturePython)
  n = 9
  ref = H_element
FEATURE [App::DocumentObjectGroupPython] N_element037  label="N_element : 016"  # scripted group (container) (typed FeaturePython)
  n = 1
  ref = N_element
FEATURE [App::DocumentObjectGroupPython] O_element084  label="O_element : 045"  # scripted group (container) (typed FeaturePython)
  n = 1
  ref = O_element
FEATURE [App::DocumentObjectGroupPython] G4_POLYVINYL_PYRROLIDONE  # scripted group (container) (typed FeaturePython)
  Dunit = g/cm3
  Dvalue = 1.25
  Group = -> [C_element095,H_element087,N_element037,O_element084]
  conduct = 2
  density = 1
  expand = 3
  formula = G4_POLYVINYL_PYRROLIDONE
  name = G4_POLYVINYL_PYRROLIDONE
  specific = 4
FEATURE [App::DocumentObjectGroupPython] K_element008  label="K_element : 1"  # scripted group (container) (typed FeaturePython)
  n = 1
  ref = K_element
FEATURE [App::DocumentObjectGroupPython] I_element006  label="I_element : 003"  # scripted group (container) (typed FeaturePython)
  n = 1
  ref = I_element
FEATURE [App::DocumentObjectGroupPython] G4_POTASSIUM_IODIDE  # scripted group (container) (typed FeaturePython)
  Dunit = g/cm3
  Dvalue = 3.13
  Group = -> [K_element008,I_element006]
  conduct = 2
  density = 1
  expand = 3
  formula = G4_POTASSIUM_IODIDE
  name = G4_POTASSIUM_IODIDE
  specific = 4
FEATURE [App::DocumentObjectGroupPython] K_element009  label="K_element : 2"  # scripted group (container) (typed FeaturePython)
  n = 2
  ref = K_element
FEATURE [App::DocumentObjectGroupPython] O_element085  label="O_element : 046"  # scripted group (container) (typed FeaturePython)
  n = 1
  ref = O_element
FEATURE [App::DocumentObjectGroupPython] G4_POTASSIUM_OXIDE  # scripted group (container) (typed FeaturePython)
  Dunit = g/cm3
  Dvalue = 2.32
  Group = -> [K_element009,O_element085]
  conduct = 2
  density = 1
  expand = 3
  formula = G4_POTASSIUM_OXIDE
  name = G4_POTASSIUM_OXIDE
  specific = 4
FEATURE [App::DocumentObjectGroupPython] C_element096  label="C_element : 054"  # scripted group (container) (typed FeaturePython)
  n = 3
  ref = C_element
FEATURE [App::DocumentObjectGroupPython] H_element088  label="H_element : 049"  # scripted group (container) (typed FeaturePython)
  n = 8
  ref = H_element
FEATURE [App::DocumentObjectGroupPython] G4_PROPANE  # scripted group (container) (typed FeaturePython)
  Dunit = g/cm3
  Dvalue = 0.00187939
  Group = -> [C_element096,H_element088]
  conduct = 2
  density = 1
  expand = 3
  formula = G4_PROPANE
  name = G4_PROPANE
  specific = 4
FEATURE [App::DocumentObjectGroupPython] C_element097  label="C_element : 055"  # scripted group (container) (typed FeaturePython)
  n = 3
  ref = C_element
FEATURE [App::DocumentObjectGroupPython] H_element089  label="H_element : 050"  # scripted group (container) (typed FeaturePython)
  n = 8
  ref = H_element
FEATURE [App::DocumentObjectGroupPython] G4_lPROPANE  # scripted group (container) (typed FeaturePython)
  Dunit = g/cm3
  Dvalue = 0.43
  Group = -> [C_element097,H_element089]
  conduct = 2
  density = 1
  expand = 3
  formula = G4_lPROPANE
  name = G4_lPROPANE
  specific = 4
FEATURE [App::DocumentObjectGroupPython] C_element098  label="C_element : 056"  # scripted group (container) (typed FeaturePython)
  n = 3
  ref = C_element
FEATURE [App::DocumentObjectGroupPython] H_element090  label="H_element : 051"  # scripted group (container) (typed FeaturePython)
  n = 8
  ref = H_element
FEATURE [App::DocumentObjectGroupPython] O_element086  label="O_element : 047"  # scripted group (container) (typed FeaturePython)
  n = 1
  ref = O_element
FEATURE [App::DocumentObjectGroupPython] G4_N_PROPYL_ALCOHOL  label="G4_N-PROPYL_ALCOHOL"  # scripted group (container) (typed FeaturePython)
  Dunit = g/cm3
  Dvalue = 0.8035
  Group = -> [C_element098,H_element090,O_element086]
  conduct = 2
  density = 1
  expand = 3
  formula = G4_N-PROPYL_ALCOHOL
  name = G4_N-PROPYL_ALCOHOL
  specific = 4
FEATURE [App::DocumentObjectGroupPython] C_element099  label="C_element : 057"  # scripted group (container) (typed FeaturePython)
  n = 5
  ref = C_element
FEATURE [App::DocumentObjectGroupPython] H_element091  label="H_element : 052"  # scripted group (container) (typed FeaturePython)
  n = 5
  ref = H_element
FEATURE [App::DocumentObjectGroupPython] N_element038  label="N_element : 017"  # scripted group (container) (typed FeaturePython)
  n = 1
  ref = N_element
FEATURE [App::DocumentObjectGroupPython] G4_PYRIDINE  # scripted group (container) (typed FeaturePython)
  Dunit = g/cm3
  Dvalue = 0.9819
  Group = -> [C_element099,H_element091,N_element038]
  conduct = 2
  density = 1
  expand = 3
  formula = G4_PYRIDINE
  name = G4_PYRIDINE
  specific = 4
FEATURE [App::DocumentObjectGroupPython] H_element092  label="H_element : 0.144"  # scripted group (container) (typed FeaturePython)
  n = 0.143711
FEATURE [App::DocumentObjectGroupPython] C_element100  label="C_element : 0.856"  # scripted group (container) (typed FeaturePython)
  n = 0.856289
FEATURE [App::DocumentObjectGroupPython] G4_RUBBER_BUTYL  # scripted group (container) (typed FeaturePython)
  Dunit = g/cm3
  Dvalue = 0.92
  Group = -> [H_element092,C_element100]
  conduct = 2
  density = 1
  expand = 3
  formula = G4_RUBBER_BUTYL
  name = G4_RUBBER_BUTYL
  specific = 4
FEATURE [App::DocumentObjectGroupPython] H_element093  label="H_element : 0.118"  # scripted group (container) (typed FeaturePython)
  n = 0.118371
FEATURE [App::DocumentObjectGroupPython] C_element101  label="C_element : 0.882"  # scripted group (container) (typed FeaturePython)
  n = 0.881629
FEATURE [App::DocumentObjectGroupPython] G4_RUBBER_NATURAL  # scripted group (container) (typed FeaturePython)
  Dunit = g/cm3
  Dvalue = 0.92
  Group = -> [H_element093,C_element101]
  conduct = 2
  density = 1
  expand = 3
  formula = G4_RUBBER_NATURAL
  name = G4_RUBBER_NATURAL
  specific = 4
FEATURE [App::DocumentObjectGroupPython] H_element094  label="H_element : 0.145"  # scripted group (container) (typed FeaturePython)
  n = 0.05692
FEATURE [App::DocumentObjectGroupPython] C_element102  label="C_element : 0.543"  # scripted group (container) (typed FeaturePython)
  n = 0.542646
FEATURE [App::DocumentObjectGroupPython] Cl_element021  label="Cl_element : 0.400"  # scripted group (container) (typed FeaturePython)
  n = 0.400434
FEATURE [App::DocumentObjectGroupPython] G4_RUBBER_NEOPRENE  # scripted group (container) (typed FeaturePython)
  Dunit = g/cm3
  Dvalue = 1.23
  Group = -> [H_element094,C_element102,Cl_element021]
  conduct = 2
  density = 1
  expand = 3
  formula = G4_RUBBER_NEOPRENE
  name = G4_RUBBER_NEOPRENE
  specific = 4
FEATURE [App::DocumentObjectGroupPython] Si_element006  label="Si_element : 1"  # scripted group (container) (typed FeaturePython)
  n = 1
  ref = Si_element
FEATURE [App::DocumentObjectGroupPython] O_element087  label="O_element : 048"  # scripted group (container) (typed FeaturePython)
  n = 2
  ref = O_element
FEATURE [App::DocumentObjectGroupPython] G4_SILICON_DIOXIDE  # scripted group (container) (typed FeaturePython)
  Dunit = g/cm3
  Dvalue = 2.32
  Group = -> [Si_element006,O_element087]
  conduct = 2
  density = 1
  expand = 3
  formula = G4_SILICON_DIOXIDE
  name = G4_SILICON_DIOXIDE
  specific = 4
FEATURE [App::DocumentObjectGroupPython] Ag_element002  label="Ag_element : 1"  # scripted group (container) (typed FeaturePython)
  n = 1
  ref = Ag_element
FEATURE [App::DocumentObjectGroupPython] Br_element005  label="Br_element : 003"  # scripted group (container) (typed FeaturePython)
  n = 1
  ref = Br_element
FEATURE [App::DocumentObjectGroupPython] G4_SILVER_BROMIDE  # scripted group (container) (typed FeaturePython)
  Dunit = g/cm3
  Dvalue = 6.473
  Group = -> [Ag_element002,Br_element005]
  conduct = 2
  density = 1
  expand = 3
  formula = G4_SILVER_BROMIDE
  name = G4_SILVER_BROMIDE
  specific = 4
FEATURE [App::DocumentObjectGroupPython] Ag_element003  label="Ag_element : 002"  # scripted group (container) (typed FeaturePython)
  n = 1
  ref = Ag_element
FEATURE [App::DocumentObjectGroupPython] Cl_element022  label="Cl_element : 011"  # scripted group (container) (typed FeaturePython)
  n = 1
  ref = Cl_element
FEATURE [App::DocumentObjectGroupPython] G4_SILVER_CHLORIDE  # scripted group (container) (typed FeaturePython)
  Dunit = g/cm3
  Dvalue = 5.56
  Group = -> [Ag_element003,Cl_element022]
  conduct = 2
  density = 1
  expand = 3
  formula = G4_SILVER_CHLORIDE
  name = G4_SILVER_CHLORIDE
  specific = 4
FEATURE [App::DocumentObjectGroupPython] Br_element006  label="Br_element : 0.423"  # scripted group (container) (typed FeaturePython)
  n = 0.422895
FEATURE [App::DocumentObjectGroupPython] Ag_element004  label="Ag_element : 0.574"  # scripted group (container) (typed FeaturePython)
  n = 0.573748
FEATURE [App::DocumentObjectGroupPython] I_element007  label="I_element : 0.649"  # scripted group (container) (typed FeaturePython)
  n = 0.003357
FEATURE [App::DocumentObjectGroupPython] G4_SILVER_HALIDES  # scripted group (container) (typed FeaturePython)
  Dunit = g/cm3
  Dvalue = 6.47
  Group = -> [Br_element006,Ag_element004,I_element007]
  conduct = 2
  density = 1
  expand = 3
  formula = G4_SILVER_HALIDES
  name = G4_SILVER_HALIDES
  specific = 4
FEATURE [App::DocumentObjectGroupPython] Ag_element005  label="Ag_element : 003"  # scripted group (container) (typed FeaturePython)
  n = 1
  ref = Ag_element
FEATURE [App::DocumentObjectGroupPython] I_element008  label="I_element : 004"  # scripted group (container) (typed FeaturePython)
  n = 1
  ref = I_element
FEATURE [App::DocumentObjectGroupPython] G4_SILVER_IODIDE  # scripted group (container) (typed FeaturePython)
  Dunit = g/cm3
  Dvalue = 6.01
  Group = -> [Ag_element005,I_element008]
  conduct = 2
  density = 1
  expand = 3
  formula = G4_SILVER_IODIDE
  name = G4_SILVER_IODIDE
  specific = 4
FEATURE [App::DocumentObjectGroupPython] H_element095  label="H_element : 0.100"  # scripted group (container) (typed FeaturePython)
  n = 0.1
FEATURE [App::DocumentObjectGroupPython] C_element103  label="C_element : 0.204"  # scripted group (container) (typed FeaturePython)
  n = 0.204
FEATURE [App::DocumentObjectGroupPython] N_element039  label="N_element : 0.759"  # scripted group (container) (typed FeaturePython)
  n = 0.042
FEATURE [App::DocumentObjectGroupPython] O_element088  label="O_element : 0.645"  # scripted group (container) (typed FeaturePython)
  n = 0.645
FEATURE [App::DocumentObjectGroupPython] Na_element013  label="Na_element : 0.100"  # scripted group (container) (typed FeaturePython)
  n = 0.002
FEATURE [App::DocumentObjectGroupPython] P_element009  label="P_element : 0.107"  # scripted group (container) (typed FeaturePython)
  n = 0.001
FEATURE [App::DocumentObjectGroupPython] S_element020  label="S_element : 0.021"  # scripted group (container) (typed FeaturePython)
  n = 0.002
FEATURE [App::DocumentObjectGroupPython] Cl_element023  label="Cl_element : 0.590"  # scripted group (container) (typed FeaturePython)
  n = 0.003
FEATURE [App::DocumentObjectGroupPython] K_element010  label="K_element : 0.001"  # scripted group (container) (typed FeaturePython)
  n = 0.001
FEATURE [App::DocumentObjectGroupPython] G4_SKIN_ICRP  # scripted group (container) (typed FeaturePython)
  Dunit = g/cm3
  Dvalue = 1.09
  Group = -> [H_element095,C_element103,N_element039,O_element088,Na_element013,P_element009,S_element020,Cl_element023,K_element010]
  conduct = 2
  density = 1
  expand = 3
  formula = G4_SKIN_ICRP
  name = G4_SKIN_ICRP
  specific = 4
FEATURE [App::DocumentObjectGroupPython] Na_element014  label="Na_element : 2"  # scripted group (container) (typed FeaturePython)
  n = 2
  ref = Na_element
FEATURE [App::DocumentObjectGroupPython] C_element104  label="C_element : 058"  # scripted group (container) (typed FeaturePython)
  n = 1
  ref = C_element
FEATURE [App::DocumentObjectGroupPython] O_element089  label="O_element : 049"  # scripted group (container) (typed FeaturePython)
  n = 3
  ref = O_element
FEATURE [App::DocumentObjectGroupPython] G4_SODIUM_CARBONATE  # scripted group (container) (typed FeaturePython)
  Dunit = g/cm3
  Dvalue = 2.532
  Group = -> [Na_element014,C_element104,O_element089]
  conduct = 2
  density = 1
  expand = 3
  formula = G4_SODIUM_CARBONATE
  name = G4_SODIUM_CARBONATE
  specific = 4
FEATURE [App::DocumentObjectGroupPython] Na_element015  label="Na_element : 1"  # scripted group (container) (typed FeaturePython)
  n = 1
  ref = Na_element
FEATURE [App::DocumentObjectGroupPython] I_element009  label="I_element : 005"  # scripted group (container) (typed FeaturePython)
  n = 1
  ref = I_element
FEATURE [App::DocumentObjectGroupPython] G4_SODIUM_IODIDE  # scripted group (container) (typed FeaturePython)
  Dunit = g/cm3
  Dvalue = 3.667
  Group = -> [Na_element015,I_element009]
  conduct = 2
  density = 1
  expand = 3
  formula = G4_SODIUM_IODIDE
  name = G4_SODIUM_IODIDE
  specific = 4
FEATURE [App::DocumentObjectGroupPython] Na_element016  label="Na_element : 003"  # scripted group (container) (typed FeaturePython)
  n = 2
  ref = Na_element
FEATURE [App::DocumentObjectGroupPython] O_element090  label="O_element : 050"  # scripted group (container) (typed FeaturePython)
  n = 1
  ref = O_element
FEATURE [App::DocumentObjectGroupPython] G4_SODIUM_MONOXIDE  # scripted group (container) (typed FeaturePython)
  Dunit = g/cm3
  Dvalue = 2.27
  Group = -> [Na_element016,O_element090]
  conduct = 2
  density = 1
  expand = 3
  formula = G4_SODIUM_MONOXIDE
  name = G4_SODIUM_MONOXIDE
  specific = 4
FEATURE [App::DocumentObjectGroupPython] Na_element017  label="Na_element : 004"  # scripted group (container) (typed FeaturePython)
  n = 1
  ref = Na_element
FEATURE [App::DocumentObjectGroupPython] N_element040  label="N_element : 018"  # scripted group (container) (typed FeaturePython)
  n = 1
  ref = N_element
FEATURE [App::DocumentObjectGroupPython] O_element091  label="O_element : 051"  # scripted group (container) (typed FeaturePython)
  n = 3
  ref = O_element
FEATURE [App::DocumentObjectGroupPython] G4_SODIUM_NITRATE  # scripted group (container) (typed FeaturePython)
  Dunit = g/cm3
  Dvalue = 2.261
  Group = -> [Na_element017,N_element040,O_element091]
  conduct = 2
  density = 1
  expand = 3
  formula = G4_SODIUM_NITRATE
  name = G4_SODIUM_NITRATE
  specific = 4
FEATURE [App::DocumentObjectGroupPython] C_element105  label="C_element : 059"  # scripted group (container) (typed FeaturePython)
  n = 14
  ref = C_element
FEATURE [App::DocumentObjectGroupPython] H_element096  label="H_element : 053"  # scripted group (container) (typed FeaturePython)
  n = 12
  ref = H_element
FEATURE [App::DocumentObjectGroupPython] G4_STILBENE  # scripted group (container) (typed FeaturePython)
  Dunit = g/cm3
  Dvalue = 0.9707
  Group = -> [C_element105,H_element096]
  conduct = 2
  density = 1
  expand = 3
  formula = G4_STILBENE
  name = G4_STILBENE
  specific = 4
FEATURE [App::DocumentObjectGroupPython] C_element106  label="C_element : 12"  # scripted group (container) (typed FeaturePython)
  n = 12
  ref = C_element
FEATURE [App::DocumentObjectGroupPython] H_element097  label="H_element : 22"  # scripted group (container) (typed FeaturePython)
  n = 22
  ref = H_element
FEATURE [App::DocumentObjectGroupPython] O_element092  label="O_element : 11"  # scripted group (container) (typed FeaturePython)
  n = 11
  ref = O_element
FEATURE [App::DocumentObjectGroupPython] G4_SUCROSE  # scripted group (container) (typed FeaturePython)
  Dunit = g/cm3
  Dvalue = 1.5805
  Group = -> [C_element106,H_element097,O_element092]
  conduct = 2
  density = 1
  expand = 3
  formula = G4_SUCROSE
  name = G4_SUCROSE
  specific = 4
FEATURE [App::DocumentObjectGroupPython] C_element107  label="C_element : 18"  # scripted group (container) (typed FeaturePython)
  n = 18
  ref = C_element
FEATURE [App::DocumentObjectGroupPython] H_element098  label="H_element : 054"  # scripted group (container) (typed FeaturePython)
  n = 14
  ref = H_element
FEATURE [App::DocumentObjectGroupPython] G4_TERPHENYL  # scripted group (container) (typed FeaturePython)
  Dunit = g/cm3
  Dvalue = 1.24
  Group = -> [C_element107,H_element098]
  conduct = 2
  density = 1
  expand = 3
  formula = G4_TERPHENYL
  name = G4_TERPHENYL
  specific = 4
FEATURE [App::DocumentObjectGroupPython] H_element099  label="H_element : 0.146"  # scripted group (container) (typed FeaturePython)
  n = 0.106
FEATURE [App::DocumentObjectGroupPython] C_element108  label="C_element : 0.883"  # scripted group (container) (typed FeaturePython)
  n = 0.099
FEATURE [App::DocumentObjectGroupPython] N_element041  label="N_element : 0.020"  # scripted group (container) (typed FeaturePython)
  n = 0.02
FEATURE [App::DocumentObjectGroupPython] O_element093  label="O_element : 0.766"  # scripted group (container) (typed FeaturePython)
  n = 0.766
FEATURE [App::DocumentObjectGroupPython] Na_element018  label="Na_element : 0.101"  # scripted group (container) (typed FeaturePython)
  n = 0.002
FEATURE [App::DocumentObjectGroupPython] P_element010  label="P_element : 0.108"  # scripted group (container) (typed FeaturePython)
  n = 0.001
FEATURE [App::DocumentObjectGroupPython] S_element021  label="S_element : 0.022"  # scripted group (container) (typed FeaturePython)
  n = 0.002
FEATURE [App::DocumentObjectGroupPython] Cl_element024  label="Cl_element : 0.002"  # scripted group (container) (typed FeaturePython)
  n = 0.002
FEATURE [App::DocumentObjectGroupPython] K_element011  label="K_element : 0.017"  # scripted group (container) (typed FeaturePython)
  n = 0.002
FEATURE [App::DocumentObjectGroupPython] G4_TESTIS_ICRP  # scripted group (container) (typed FeaturePython)
  Dunit = g/cm3
  Dvalue = 1.04
  Group = -> [H_element099,C_element108,N_element041,O_element093,Na_element018,P_element010,S_element021,Cl_element024,K_element011]
  conduct = 2
  density = 1
  expand = 3
  formula = G4_TESTIS_ICRP
  name = G4_TESTIS_ICRP
  specific = 4
FEATURE [App::DocumentObjectGroupPython] C_element109  label="C_element : 060"  # scripted group (container) (typed FeaturePython)
  n = 2
  ref = C_element
FEATURE [App::DocumentObjectGroupPython] Cl_element025  label="Cl_element : 012"  # scripted group (container) (typed FeaturePython)
  n = 4
  ref = Cl_element
FEATURE [App::DocumentObjectGroupPython] G4_TETRACHLOROETHYLENE  # scripted group (container) (typed FeaturePython)
  Dunit = g/cm3
  Dvalue = 1.625
  Group = -> [C_element109,Cl_element025]
  conduct = 2
  density = 1
  expand = 3
  formula = G4_TETRACHLOROETHYLENE
  name = G4_TETRACHLOROETHYLENE
  specific = 4
FEATURE [App::DocumentObjectGroupPython] Tl_element001  label="Tl_element : 1"  # scripted group (container) (typed FeaturePython)
  n = 1
  ref = Tl_element
FEATURE [App::DocumentObjectGroupPython] Cl_element026  label="Cl_element : 013"  # scripted group (container) (typed FeaturePython)
  n = 1
  ref = Cl_element
FEATURE [App::DocumentObjectGroupPython] G4_THALLIUM_CHLORIDE  # scripted group (container) (typed FeaturePython)
  Dunit = g/cm3
  Dvalue = 7.004
  Group = -> [Tl_element001,Cl_element026]
  conduct = 2
  density = 1
  expand = 3
  formula = G4_THALLIUM_CHLORIDE
  name = G4_THALLIUM_CHLORIDE
  specific = 4
FEATURE [App::DocumentObjectGroupPython] H_element100  label="H_element : 0.147"  # scripted group (container) (typed FeaturePython)
  n = 0.105
FEATURE [App::DocumentObjectGroupPython] C_element110  label="C_element : 0.256"  # scripted group (container) (typed FeaturePython)
  n = 0.256
FEATURE [App::DocumentObjectGroupPython] N_element042  label="N_element : 0.760"  # scripted group (container) (typed FeaturePython)
  n = 0.027
FEATURE [App::DocumentObjectGroupPython] O_element094  label="O_element : 0.602"  # scripted group (container) (typed FeaturePython)
  n = 0.602
FEATURE [App::DocumentObjectGroupPython] Na_element019  label="Na_element : 0.102"  # scripted group (container) (typed FeaturePython)
  n = 0.001
FEATURE [App::DocumentObjectGroupPython] P_element011  label="P_element : 0.109"  # scripted group (container) (typed FeaturePython)
  n = 0.002
FEATURE [App::DocumentObjectGroupPython] S_element022  label="S_element : 0.023"  # scripted group (container) (typed FeaturePython)
  n = 0.003
FEATURE [App::DocumentObjectGroupPython] Cl_element027  label="Cl_element : 0.591"  # scripted group (container) (typed FeaturePython)
  n = 0.002
FEATURE [App::DocumentObjectGroupPython] K_element012  label="K_element : 0.018"  # scripted group (container) (typed FeaturePython)
  n = 0.002
FEATURE [App::DocumentObjectGroupPython] G4_TISSUE_SOFT_ICRP  # scripted group (container) (typed FeaturePython)
  Dunit = g/cm3
  Dvalue = 1.03
  Group = -> [H_element100,C_element110,N_element042,O_element094,Na_element019,P_element011,S_element022,Cl_element027,K_element012]
  conduct = 2
  density = 1
  expand = 3
  formula = G4_TISSUE_SOFT_ICRP
  name = G4_TISSUE_SOFT_ICRP
  specific = 4
FEATURE [App::DocumentObjectGroupPython] H_element101  label="H_element : 0.148"  # scripted group (container) (typed FeaturePython)
  n = 0.101
FEATURE [App::DocumentObjectGroupPython] C_element111  label="C_element : 0.111"  # scripted group (container) (typed FeaturePython)
  n = 0.111
FEATURE [App::DocumentObjectGroupPython] N_element043  label="N_element : 0.026"  # scripted group (container) (typed FeaturePython)
  n = 0.026
FEATURE [App::DocumentObjectGroupPython] O_element095  label="O_element : 0.762"  # scripted group (container) (typed FeaturePython)
  n = 0.762
FEATURE [App::DocumentObjectGroupPython] G4_TISSUE_SOFT_ICRU_4  label="G4_TISSUE_SOFT_ICRU-4"  # scripted group (container) (typed FeaturePython)
  Dunit = g/cm3
  Dvalue = 1
  Group = -> [H_element101,C_element111,N_element043,O_element095]
  conduct = 2
  density = 1
  expand = 3
  formula = G4_TISSUE_SOFT_ICRU-4
  name = G4_TISSUE_SOFT_ICRU-4
  specific = 4
FEATURE [App::DocumentObjectGroupPython] H_element102  label="H_element : 0.149"  # scripted group (container) (typed FeaturePython)
  n = 0.101869
FEATURE [App::DocumentObjectGroupPython] C_element112  label="C_element : 0.456"  # scripted group (container) (typed FeaturePython)
  n = 0.456179
FEATURE [App::DocumentObjectGroupPython] N_element044  label="N_element : 0.761"  # scripted group (container) (typed FeaturePython)
  n = 0.035172
FEATURE [App::DocumentObjectGroupPython] O_element096  label="O_element : 0.407"  # scripted group (container) (typed FeaturePython)
  n = 0.40678
FEATURE [App::DocumentObjectGroupPython] G4_TISSUE_METHANE  label="G4_TISSUE-METHANE"  # scripted group (container) (typed FeaturePython)
  Dunit = g/cm3
  Dvalue = 0.00106409
  Group = -> [H_element102,C_element112,N_element044,O_element096]
  conduct = 2
  density = 1
  expand = 3
  formula = G4_TISSUE-METHANE
  name = G4_TISSUE-METHANE
  specific = 4
FEATURE [App::DocumentObjectGroupPython] H_element103  label="H_element : 0.103"  # scripted group (container) (typed FeaturePython)
  n = 0.102672
FEATURE [App::DocumentObjectGroupPython] C_element113  label="C_element : 0.569"  # scripted group (container) (typed FeaturePython)
  n = 0.56894
FEATURE [App::DocumentObjectGroupPython] N_element045  label="N_element : 0.762"  # scripted group (container) (typed FeaturePython)
  n = 0.035022
FEATURE [App::DocumentObjectGroupPython] O_element097  label="O_element : 0.293"  # scripted group (container) (typed FeaturePython)
  n = 0.293366
FEATURE [App::DocumentObjectGroupPython] G4_TISSUE_PROPANE  label="G4_TISSUE-PROPANE"  # scripted group (container) (typed FeaturePython)
  Dunit = g/cm3
  Dvalue = 0.00182628
  Group = -> [H_element103,C_element113,N_element045,O_element097]
  conduct = 2
  density = 1
  expand = 3
  formula = G4_TISSUE-PROPANE
  name = G4_TISSUE-PROPANE
  specific = 4
FEATURE [App::DocumentObjectGroupPython] Ti_element003  label="Ti_element : 1"  # scripted group (container) (typed FeaturePython)
  n = 1
  ref = Ti_element
FEATURE [App::DocumentObjectGroupPython] O_element098  label="O_element : 052"  # scripted group (container) (typed FeaturePython)
  n = 2
  ref = O_element
FEATURE [App::DocumentObjectGroupPython] G4_TITANIUM_DIOXIDE  # scripted group (container) (typed FeaturePython)
  Dunit = g/cm3
  Dvalue = 4.26
  Group = -> [Ti_element003,O_element098]
  conduct = 2
  density = 1
  expand = 3
  formula = G4_TITANIUM_DIOXIDE
  name = G4_TITANIUM_DIOXIDE
  specific = 4
FEATURE [App::DocumentObjectGroupPython] C_element114  label="C_element : 061"  # scripted group (container) (typed FeaturePython)
  n = 7
  ref = C_element
FEATURE [App::DocumentObjectGroupPython] H_element104  label="H_element : 055"  # scripted group (container) (typed FeaturePython)
  n = 8
  ref = H_element
FEATURE [App::DocumentObjectGroupPython] G4_TOLUENE  # scripted group (container) (typed FeaturePython)
  Dunit = g/cm3
  Dvalue = 0.8669
  Group = -> [C_element114,H_element104]
  conduct = 2
  density = 1
  expand = 3
  formula = G4_TOLUENE
  name = G4_TOLUENE
  specific = 4
FEATURE [App::DocumentObjectGroupPython] C_element115  label="C_element : 062"  # scripted group (container) (typed FeaturePython)
  n = 2
  ref = C_element
FEATURE [App::DocumentObjectGroupPython] H_element105  label="H_element : 056"  # scripted group (container) (typed FeaturePython)
  n = 1
  ref = H_element
FEATURE [App::DocumentObjectGroupPython] Cl_element028  label="Cl_element : 014"  # scripted group (container) (typed FeaturePython)
  n = 3
  ref = Cl_element
FEATURE [App::DocumentObjectGroupPython] G4_TRICHLOROETHYLENE  # scripted group (container) (typed FeaturePython)
  Dunit = g/cm3
  Dvalue = 1.46
  Group = -> [C_element115,H_element105,Cl_element028]
  conduct = 2
  density = 1
  expand = 3
  formula = G4_TRICHLOROETHYLENE
  name = G4_TRICHLOROETHYLENE
  specific = 4
FEATURE [App::DocumentObjectGroupPython] C_element116  label="C_element : 063"  # scripted group (container) (typed FeaturePython)
  n = 6
  ref = C_element
FEATURE [App::DocumentObjectGroupPython] H_element106  label="H_element : 15"  # scripted group (container) (typed FeaturePython)
  n = 15
  ref = H_element
FEATURE [App::DocumentObjectGroupPython] O_element099  label="O_element : 053"  # scripted group (container) (typed FeaturePython)
  n = 4
  ref = O_element
FEATURE [App::DocumentObjectGroupPython] P_element012  label="P_element : 1"  # scripted group (container) (typed FeaturePython)
  n = 1
  ref = P_element
FEATURE [App::DocumentObjectGroupPython] G4_TRIETHYL_PHOSPHATE  # scripted group (container) (typed FeaturePython)
  Dunit = g/cm3
  Dvalue = 1.07
  Group = -> [C_element116,H_element106,O_element099,P_element012]
  conduct = 2
  density = 1
  expand = 3
  formula = G4_TRIETHYL_PHOSPHATE
  name = G4_TRIETHYL_PHOSPHATE
  specific = 4
FEATURE [App::DocumentObjectGroupPython] W_element003  label="W_element : 003"  # scripted group (container) (typed FeaturePython)
  n = 1
  ref = W_element
FEATURE [App::DocumentObjectGroupPython] F_element017  label="F_element : 6"  # scripted group (container) (typed FeaturePython)
  n = 6
  ref = F_element
FEATURE [App::DocumentObjectGroupPython] G4_TUNGSTEN_HEXAFLUORIDE  # scripted group (container) (typed FeaturePython)
  Dunit = g/cm3
  Dvalue = 2.4
  Group = -> [W_element003,F_element017]
  conduct = 2
  density = 1
  expand = 3
  formula = G4_TUNGSTEN_HEXAFLUORIDE
  name = G4_TUNGSTEN_HEXAFLUORIDE
  specific = 4
FEATURE [App::DocumentObjectGroupPython] U_element001  label="U_element : 1"  # scripted group (container) (typed FeaturePython)
  n = 1
  ref = U_element
FEATURE [App::DocumentObjectGroupPython] C_element117  label="C_element : 064"  # scripted group (container) (typed FeaturePython)
  n = 2
  ref = C_element
FEATURE [App::DocumentObjectGroupPython] G4_URANIUM_DICARBIDE  # scripted group (container) (typed FeaturePython)
  Dunit = g/cm3
  Dvalue = 11.28
  Group = -> [U_element001,C_element117]
  conduct = 2
  density = 1
  expand = 3
  formula = G4_URANIUM_DICARBIDE
  name = G4_URANIUM_DICARBIDE
  specific = 4
FEATURE [App::DocumentObjectGroupPython] U_element002  label="U_element : 002"  # scripted group (container) (typed FeaturePython)
  n = 1
  ref = U_element
FEATURE [App::DocumentObjectGroupPython] C_element118  label="C_element : 065"  # scripted group (container) (typed FeaturePython)
  n = 1
  ref = C_element
FEATURE [App::DocumentObjectGroupPython] G4_URANIUM_MONOCARBIDE  # scripted group (container) (typed FeaturePython)
  Dunit = g/cm3
  Dvalue = 13.63
  Group = -> [U_element002,C_element118]
  conduct = 2
  density = 1
  expand = 3
  formula = G4_URANIUM_MONOCARBIDE
  name = G4_URANIUM_MONOCARBIDE
  specific = 4
FEATURE [App::DocumentObjectGroupPython] U_element003  label="U_element : 003"  # scripted group (container) (typed FeaturePython)
  n = 1
  ref = U_element
FEATURE [App::DocumentObjectGroupPython] O_element100  label="O_element : 054"  # scripted group (container) (typed FeaturePython)
  n = 2
  ref = O_element
FEATURE [App::DocumentObjectGroupPython] G4_URANIUM_OXIDE  # scripted group (container) (typed FeaturePython)
  Dunit = g/cm3
  Dvalue = 10.96
  Group = -> [U_element003,O_element100]
  conduct = 2
  density = 1
  expand = 3
  formula = G4_URANIUM_OXIDE
  name = G4_URANIUM_OXIDE
  specific = 4
FEATURE [App::DocumentObjectGroupPython] C_element119  label="C_element : 066"  # scripted group (container) (typed FeaturePython)
  n = 1
  ref = C_element
FEATURE [App::DocumentObjectGroupPython] H_element107  label="H_element : 057"  # scripted group (container) (typed FeaturePython)
  n = 4
  ref = H_element
FEATURE [App::DocumentObjectGroupPython] N_element046  label="N_element : 019"  # scripted group (container) (typed FeaturePython)
  n = 2
  ref = N_element
FEATURE [App::DocumentObjectGroupPython] O_element101  label="O_element : 055"  # scripted group (container) (typed FeaturePython)
  n = 1
  ref = O_element
FEATURE [App::DocumentObjectGroupPython] G4_UREA  # scripted group (container) (typed FeaturePython)
  Dunit = g/cm3
  Dvalue = 1.323
  Group = -> [C_element119,H_element107,N_element046,O_element101]
  conduct = 2
  density = 1
  expand = 3
  formula = G4_UREA
  name = G4_UREA
  specific = 4
FEATURE [App::DocumentObjectGroupPython] C_element120  label="C_element : 067"  # scripted group (container) (typed FeaturePython)
  n = 5
  ref = C_element
FEATURE [App::DocumentObjectGroupPython] H_element108  label="H_element : 058"  # scripted group (container) (typed FeaturePython)
  n = 11
  ref = H_element
FEATURE [App::DocumentObjectGroupPython] N_element047  label="N_element : 020"  # scripted group (container) (typed FeaturePython)
  n = 1
  ref = N_element
FEATURE [App::DocumentObjectGroupPython] O_element102  label="O_element : 056"  # scripted group (container) (typed FeaturePython)
  n = 2
  ref = O_element
FEATURE [App::DocumentObjectGroupPython] G4_VALINE  # scripted group (container) (typed FeaturePython)
  Dunit = g/cm3
  Dvalue = 1.23
  Group = -> [C_element120,H_element108,N_element047,O_element102]
  conduct = 2
  density = 1
  expand = 3
  formula = G4_VALINE
  name = G4_VALINE
  specific = 4
FEATURE [App::DocumentObjectGroupPython] H_element109  label="H_element : 0.009"  # scripted group (container) (typed FeaturePython)
  n = 0.009417
FEATURE [App::DocumentObjectGroupPython] C_element121  label="C_element : 0.281"  # scripted group (container) (typed FeaturePython)
  n = 0.280555
FEATURE [App::DocumentObjectGroupPython] F_element018  label="F_element : 0.710"  # scripted group (container) (typed FeaturePython)
  n = 0.710028
FEATURE [App::DocumentObjectGroupPython] G4_VITON  # scripted group (container) (typed FeaturePython)
  Dunit = g/cm3
  Dvalue = 1.8
  Group = -> [H_element109,C_element121,F_element018]
  conduct = 2
  density = 1
  expand = 3
  formula = G4_VITON
  name = G4_VITON
  specific = 4
FEATURE [App::DocumentObjectGroupPython] H_element110  label="H_element : 059"  # scripted group (container) (typed FeaturePython)
  n = 2
  ref = H_element
FEATURE [App::DocumentObjectGroupPython] O_element103  label="O_element : 057"  # scripted group (container) (typed FeaturePython)
  n = 1
  ref = O_element
FEATURE [App::DocumentObjectGroupPython] G4_WATER  # scripted group (container) (typed FeaturePython)
  Dunit = g/cm3
  Dvalue = 1
  Group = -> [H_element110,O_element103]
  conduct = 2
  density = 1
  expand = 3
  formula = G4_WATER
  name = G4_WATER
  specific = 4
FEATURE [App::DocumentObjectGroupPython] H_element111  label="H_element : 060"  # scripted group (container) (typed FeaturePython)
  n = 2
  ref = H_element
FEATURE [App::DocumentObjectGroupPython] O_element104  label="O_element : 058"  # scripted group (container) (typed FeaturePython)
  n = 1
  ref = O_element
FEATURE [App::DocumentObjectGroupPython] G4_WATER_VAPOR  # scripted group (container) (typed FeaturePython)
  Dunit = g/cm3
  Dvalue = 0.000756182
  Group = -> [H_element111,O_element104]
  conduct = 2
  density = 1
  expand = 3
  formula = G4_WATER_VAPOR
  name = G4_WATER_VAPOR
  specific = 4
FEATURE [App::DocumentObjectGroupPython] C_element122  label="C_element : 068"  # scripted group (container) (typed FeaturePython)
  n = 8
  ref = C_element
FEATURE [App::DocumentObjectGroupPython] H_element112  label="H_element : 061"  # scripted group (container) (typed FeaturePython)
  n = 10
  ref = H_element
FEATURE [App::DocumentObjectGroupPython] G4_XYLENE  # scripted group (container) (typed FeaturePython)
  Dunit = g/cm3
  Dvalue = 0.87
  Group = -> [C_element122,H_element112]
  conduct = 2
  density = 1
  expand = 3
  formula = G4_XYLENE
  name = G4_XYLENE
  specific = 4
FEATURE [App::DocumentObjectGroupPython] C_element123  label="C_element : 069"  # scripted group (container) (typed FeaturePython)
  n = 1
  ref = C_element
FEATURE [App::DocumentObjectGroupPython] G4_GRAPHITE  # scripted group (container) (typed FeaturePython)
  Dunit = g/cm3
  Dvalue = 2.21
  Group = -> [C_element123]
  conduct = 2
  density = 1
  expand = 3
  formula = G4_GRAPHITE
  name = G4_GRAPHITE
  specific = 4
FEATURE [App::DocumentObjectGroupPython] NIST  # scripted group (container) (typed FeaturePython)
  Group = -> [G4_A_150_TISSUE,G4_ACETONE,G4_ACETYLENE,G4_ADENINE,G4_ADIPOSE_TISSUE_ICRP,G4_AIR,G4_ALANINE,G4_ALUMINUM_OXIDE,G4_AMBER,G4_AMMONIA,G4_ANILINE,G4_ANTHRACENE,G4_B_100_BONE,G4_BAKELITE,G4_BARIUM_FLUORIDE,G4_BARIUM_SULFATE,G4_BENZENE,G4_BERYLLIUM_OXIDE,G4_BGO,G4_BLOOD_ICRP,G4_BONE_COMPACT_ICRU,G4_BONE_CORTICAL_ICRP,G4_BORON_CARBIDE,G4_BORON_OXIDE,G4_BRAIN_ICRP,G4_BUTANE,G4_N_BUTYL_ALCOHOL,G4_C_552,+152 more]
FEATURE [App::DocumentObjectGroupPython] H_element113  label="H_element : 062"  # scripted group (container) (typed FeaturePython)
  n = 1
  ref = H_element
FEATURE [App::DocumentObjectGroupPython] G4_H  # scripted group (container) (typed FeaturePython)
  Dunit = g/cm3
  Dvalue = 8.3748e-05
  Group = -> [H_element113]
  conduct = 2
  density = 1
  expand = 3
  formula = H
  name = G4_H
  specific = 4
FEATURE [App::DocumentObjectGroupPython] He_element001  label="He_element : 1"  # scripted group (container) (typed FeaturePython)
  n = 1
  ref = He_element
FEATURE [App::DocumentObjectGroupPython] G4_He  # scripted group (container) (typed FeaturePython)
  Dunit = g/cm3
  Dvalue = 0.000166322
  Group = -> [He_element001]
  conduct = 2
  density = 1
  expand = 3
  formula = He
  name = G4_He
  specific = 4
FEATURE [App::DocumentObjectGroupPython] Li_element008  label="Li_element : 008"  # scripted group (container) (typed FeaturePython)
  n = 1
  ref = Li_element
FEATURE [App::DocumentObjectGroupPython] G4_Li  # scripted group (container) (typed FeaturePython)
  Dunit = g/cm3
  Dvalue = 0.534
  Group = -> [Li_element008]
  conduct = 2
  density = 1
  expand = 3
  formula = Li
  name = G4_Li
  specific = 4
FEATURE [App::DocumentObjectGroupPython] Be_element002  label="Be_element : 002"  # scripted group (container) (typed FeaturePython)
  n = 1
  ref = Be_element
FEATURE [App::DocumentObjectGroupPython] G4_Be  # scripted group (container) (typed FeaturePython)
  Dunit = g/cm3
  Dvalue = 1.848
  Group = -> [Be_element002]
  conduct = 2
  density = 1
  expand = 3
  formula = Be
  name = G4_Be
  specific = 4
FEATURE [App::DocumentObjectGroupPython] B_element007  label="B_element : 007"  # scripted group (container) (typed FeaturePython)
  n = 1
  ref = B_element
FEATURE [App::DocumentObjectGroupPython] G4_B  # scripted group (container) (typed FeaturePython)
  Dunit = g/cm3
  Dvalue = 2.37
  Group = -> [B_element007]
  conduct = 2
  density = 1
  expand = 3
  formula = B
  name = G4_B
  specific = 4
FEATURE [App::DocumentObjectGroupPython] C_element124  label="C_element : 070"  # scripted group (container) (typed FeaturePython)
  n = 1
  ref = C_element
FEATURE [App::DocumentObjectGroupPython] G4_C  # scripted group (container) (typed FeaturePython)
  Dunit = g/cm3
  Dvalue = 2
  Group = -> [C_element124]
  conduct = 2
  density = 1
  expand = 3
  formula = C
  name = G4_C
  specific = 4
FEATURE [App::DocumentObjectGroupPython] N_element048  label="N_element : 021"  # scripted group (container) (typed FeaturePython)
  n = 1
  ref = N_element
FEATURE [App::DocumentObjectGroupPython] G4_N  # scripted group (container) (typed FeaturePython)
  Dunit = g/cm3
  Dvalue = 0.0011652
  Group = -> [N_element048]
  conduct = 2
  density = 1
  expand = 3
  formula = N
  name = G4_N
  specific = 4
FEATURE [App::DocumentObjectGroupPython] O_element105  label="O_element : 059"  # scripted group (container) (typed FeaturePython)
  n = 1
  ref = O_element
FEATURE [App::DocumentObjectGroupPython] G4_O  # scripted group (container) (typed FeaturePython)
  Dunit = g/cm3
  Dvalue = 0.00133151
  Group = -> [O_element105]
  conduct = 2
  density = 1
  expand = 3
  formula = O
  name = G4_O
  specific = 4
FEATURE [App::DocumentObjectGroupPython] F_element019  label="F_element : 008"  # scripted group (container) (typed FeaturePython)
  n = 1
  ref = F_element
FEATURE [App::DocumentObjectGroupPython] G4_F  # scripted group (container) (typed FeaturePython)
  Dunit = g/cm3
  Dvalue = 0.00158029
  Group = -> [F_element019]
  conduct = 2
  density = 1
  expand = 3
  formula = F
  name = G4_F
  specific = 4
FEATURE [App::DocumentObjectGroupPython] Ne_element001  label="Ne_element : 1"  # scripted group (container) (typed FeaturePython)
  n = 1
  ref = Ne_element
FEATURE [App::DocumentObjectGroupPython] G4_Ne  # scripted group (container) (typed FeaturePython)
  Dunit = g/cm3
  Dvalue = 0.000838505
  Group = -> [Ne_element001]
  conduct = 2
  density = 1
  expand = 3
  formula = Ne
  name = G4_Ne
  specific = 4
FEATURE [App::DocumentObjectGroupPython] Na_element020  label="Na_element : 005"  # scripted group (container) (typed FeaturePython)
  n = 1
  ref = Na_element
FEATURE [App::DocumentObjectGroupPython] G4_Na  # scripted group (container) (typed FeaturePython)
  Dunit = g/cm3
  Dvalue = 0.971
  Group = -> [Na_element020]
  conduct = 2
  density = 1
  expand = 3
  formula = Na
  name = G4_Na
  specific = 4
FEATURE [App::DocumentObjectGroupPython] Mg_element011  label="Mg_element : 005"  # scripted group (container) (typed FeaturePython)
  n = 1
  ref = Mg_element
FEATURE [App::DocumentObjectGroupPython] G4_Mg  # scripted group (container) (typed FeaturePython)
  Dunit = g/cm3
  Dvalue = 1.74
  Group = -> [Mg_element011]
  conduct = 2
  density = 1
  expand = 3
  formula = Mg
  name = G4_Mg
  specific = 4
FEATURE [App::DocumentObjectGroupPython] Al_element004  label="Al_element : 1"  # scripted group (container) (typed FeaturePython)
  n = 1
  ref = Al_element
FEATURE [App::DocumentObjectGroupPython] G4_Al  # scripted group (container) (typed FeaturePython)
  Dunit = g/cm3
  Dvalue = 2.699
  Group = -> [Al_element004]
  conduct = 2
  density = 1
  expand = 3
  formula = Al
  name = G4_Al
  specific = 4
FEATURE [App::DocumentObjectGroupPython] Si_element007  label="Si_element : 002"  # scripted group (container) (typed FeaturePython)
  n = 1
  ref = Si_element
FEATURE [App::DocumentObjectGroupPython] G4_Si  # scripted group (container) (typed FeaturePython)
  Dunit = g/cm3
  Dvalue = 2.33
  Group = -> [Si_element007]
  conduct = 2
  density = 1
  expand = 3
  formula = Si
  name = G4_Si
  specific = 4
FEATURE [App::DocumentObjectGroupPython] P_element013  label="P_element : 002"  # scripted group (container) (typed FeaturePython)
  n = 1
  ref = P_element
FEATURE [App::DocumentObjectGroupPython] G4_P  # scripted group (container) (typed FeaturePython)
  Dunit = g/cm3
  Dvalue = 2.2
  Group = -> [P_element013]
  conduct = 2
  density = 1
  expand = 3
  formula = P
  name = G4_P
  specific = 4
FEATURE [App::DocumentObjectGroupPython] S_element023  label="S_element : 007"  # scripted group (container) (typed FeaturePython)
  n = 1
  ref = S_element
FEATURE [App::DocumentObjectGroupPython] G4_S  # scripted group (container) (typed FeaturePython)
  Dunit = g/cm3
  Dvalue = 2
  Group = -> [S_element023]
  conduct = 2
  density = 1
  expand = 3
  formula = S
  name = G4_S
  specific = 4
FEATURE [App::DocumentObjectGroupPython] Cl_element029  label="Cl_element : 015"  # scripted group (container) (typed FeaturePython)
  n = 1
  ref = Cl_element
FEATURE [App::DocumentObjectGroupPython] G4_Cl  # scripted group (container) (typed FeaturePython)
  Dunit = g/cm3
  Dvalue = 0.00299473
  Group = -> [Cl_element029]
  conduct = 2
  density = 1
  expand = 3
  formula = Cl
  name = G4_Cl
  specific = 4
FEATURE [App::DocumentObjectGroupPython] Ar_element002  label="Ar_element : 1"  # scripted group (container) (typed FeaturePython)
  n = 1
  ref = Ar_element
FEATURE [App::DocumentObjectGroupPython] G4_Ar  # scripted group (container) (typed FeaturePython)
  Dunit = g/cm3
  Dvalue = 0.00166201
  Group = -> [Ar_element002]
  conduct = 2
  density = 1
  expand = 3
  formula = Ar
  name = G4_Ar
  specific = 4
FEATURE [App::DocumentObjectGroupPython] K_element013  label="K_element : 003"  # scripted group (container) (typed FeaturePython)
  n = 1
  ref = K_element
FEATURE [App::DocumentObjectGroupPython] G4_K  # scripted group (container) (typed FeaturePython)
  Dunit = g/cm3
  Dvalue = 0.862
  Group = -> [K_element013]
  conduct = 2
  density = 1
  expand = 3
  formula = K
  name = G4_K
  specific = 4
FEATURE [App::DocumentObjectGroupPython] Ca_element014  label="Ca_element : 007"  # scripted group (container) (typed FeaturePython)
  n = 1
  ref = Ca_element
FEATURE [App::DocumentObjectGroupPython] G4_Ca  # scripted group (container) (typed FeaturePython)
  Dunit = g/cm3
  Dvalue = 1.55
  Group = -> [Ca_element014]
  conduct = 2
  density = 1
  expand = 3
  formula = Ca
  name = G4_Ca
  specific = 4
FEATURE [App::DocumentObjectGroupPython] Sc_element001  label="Sc_element : 1"  # scripted group (container) (typed FeaturePython)
  n = 1
  ref = Sc_element
FEATURE [App::DocumentObjectGroupPython] G4_Sc  # scripted group (container) (typed FeaturePython)
  Dunit = g/cm3
  Dvalue = 2.989
  Group = -> [Sc_element001]
  conduct = 2
  density = 1
  expand = 3
  formula = Sc
  name = G4_Sc
  specific = 4
FEATURE [App::DocumentObjectGroupPython] Ti_element004  label="Ti_element : 002"  # scripted group (container) (typed FeaturePython)
  n = 1
  ref = Ti_element
FEATURE [App::DocumentObjectGroupPython] G4_Ti  # scripted group (container) (typed FeaturePython)
  Dunit = g/cm3
  Dvalue = 4.54
  Group = -> [Ti_element004]
  conduct = 2
  density = 1
  expand = 3
  formula = Ti
  name = G4_Ti
  specific = 4
FEATURE [App::DocumentObjectGroupPython] V_element001  label="V_element : 1"  # scripted group (container) (typed FeaturePython)
  n = 1
  ref = V_element
FEATURE [App::DocumentObjectGroupPython] G4_V  # scripted group (container) (typed FeaturePython)
  Dunit = g/cm3
  Dvalue = 6.11
  Group = -> [V_element001]
  conduct = 2
  density = 1
  expand = 3
  formula = V
  name = G4_V
  specific = 4
FEATURE [App::DocumentObjectGroupPython] Cr_element001  label="Cr_element : 1"  # scripted group (container) (typed FeaturePython)
  n = 1
  ref = Cr_element
FEATURE [App::DocumentObjectGroupPython] G4_Cr  # scripted group (container) (typed FeaturePython)
  Dunit = g/cm3
  Dvalue = 7.18
  Group = -> [Cr_element001]
  conduct = 2
  density = 1
  expand = 3
  formula = Cr
  name = G4_Cr
  specific = 4
FEATURE [App::DocumentObjectGroupPython] Mn_element001  label="Mn_element : 1"  # scripted group (container) (typed FeaturePython)
  n = 1
  ref = Mn_element
FEATURE [App::DocumentObjectGroupPython] G4_Mn  # scripted group (container) (typed FeaturePython)
  Dunit = g/cm3
  Dvalue = 7.44
  Group = -> [Mn_element001]
  conduct = 2
  density = 1
  expand = 3
  formula = Mn
  name = G4_Mn
  specific = 4
FEATURE [App::DocumentObjectGroupPython] Fe_element007  label="Fe_element : 004"  # scripted group (container) (typed FeaturePython)
  n = 1
  ref = Fe_element
FEATURE [App::DocumentObjectGroupPython] G4_Fe  # scripted group (container) (typed FeaturePython)
  Dunit = g/cm3
  Dvalue = 7.874
  Group = -> [Fe_element007]
  conduct = 2
  density = 1
  expand = 3
  formula = Fe
  name = G4_Fe
  specific = 4
FEATURE [App::DocumentObjectGroupPython] Co_element001  label="Co_element : 1"  # scripted group (container) (typed FeaturePython)
  n = 1
  ref = Co_element
FEATURE [App::DocumentObjectGroupPython] G4_Co  # scripted group (container) (typed FeaturePython)
  Dunit = g/cm3
  Dvalue = 8.9
  Group = -> [Co_element001]
  conduct = 2
  density = 1
  expand = 3
  formula = Co
  name = G4_Co
  specific = 4
FEATURE [App::DocumentObjectGroupPython] Ni_element001  label="Ni_element : 1"  # scripted group (container) (typed FeaturePython)
  n = 1
  ref = Ni_element
FEATURE [App::DocumentObjectGroupPython] G4_Ni  # scripted group (container) (typed FeaturePython)
  Dunit = g/cm3
  Dvalue = 8.902
  Group = -> [Ni_element001]
  conduct = 2
  density = 1
  expand = 3
  formula = Ni
  name = G4_Ni
  specific = 4
FEATURE [App::DocumentObjectGroupPython] Cu_element001  label="Cu_element : 1"  # scripted group (container) (typed FeaturePython)
  n = 1
  ref = Cu_element
FEATURE [App::DocumentObjectGroupPython] G4_Cu  # scripted group (container) (typed FeaturePython)
  Dunit = g/cm3
  Dvalue = 8.96
  Group = -> [Cu_element001]
  conduct = 2
  density = 1
  expand = 3
  formula = Cu
  name = G4_Cu
  specific = 4
FEATURE [App::DocumentObjectGroupPython] Zn_element001  label="Zn_element : 1"  # scripted group (container) (typed FeaturePython)
  n = 1
  ref = Zn_element
FEATURE [App::DocumentObjectGroupPython] G4_Zn  # scripted group (container) (typed FeaturePython)
  Dunit = g/cm3
  Dvalue = 7.133
  Group = -> [Zn_element001]
  conduct = 2
  density = 1
  expand = 3
  formula = Zn
  name = G4_Zn
  specific = 4
FEATURE [App::DocumentObjectGroupPython] Ga_element002  label="Ga_element : 002"  # scripted group (container) (typed FeaturePython)
  n = 1
  ref = Ga_element
FEATURE [App::DocumentObjectGroupPython] G4_Ga  # scripted group (container) (typed FeaturePython)
  Dunit = g/cm3
  Dvalue = 5.904
  Group = -> [Ga_element002]
  conduct = 2
  density = 1
  expand = 3
  formula = Ga
  name = G4_Ga
  specific = 4
FEATURE [App::DocumentObjectGroupPython] Ge_element002  label="Ge_element : 1"  # scripted group (container) (typed FeaturePython)
  n = 1
  ref = Ge_element
FEATURE [App::DocumentObjectGroupPython] G4_Ge  # scripted group (container) (typed FeaturePython)
  Dunit = g/cm3
  Dvalue = 5.323
  Group = -> [Ge_element002]
  conduct = 2
  density = 1
  expand = 3
  formula = Ge
  name = G4_Ge
  specific = 4
FEATURE [App::DocumentObjectGroupPython] As_element003  label="As_element : 002"  # scripted group (container) (typed FeaturePython)
  n = 1
  ref = As_element
FEATURE [App::DocumentObjectGroupPython] G4_As  # scripted group (container) (typed FeaturePython)
  Dunit = g/cm3
  Dvalue = 5.73
  Group = -> [As_element003]
  conduct = 2
  density = 1
  expand = 3
  formula = As
  name = G4_As
  specific = 4
FEATURE [App::DocumentObjectGroupPython] Se_element001  label="Se_element : 1"  # scripted group (container) (typed FeaturePython)
  n = 1
  ref = Se_element
FEATURE [App::DocumentObjectGroupPython] G4_Se  # scripted group (container) (typed FeaturePython)
  Dunit = g/cm3
  Dvalue = 4.5
  Group = -> [Se_element001]
  conduct = 2
  density = 1
  expand = 3
  formula = Se
  name = G4_Se
  specific = 4
FEATURE [App::DocumentObjectGroupPython] Br_element007  label="Br_element : 004"  # scripted group (container) (typed FeaturePython)
  n = 1
  ref = Br_element
FEATURE [App::DocumentObjectGroupPython] G4_Br  # scripted group (container) (typed FeaturePython)
  Dunit = g/cm3
  Dvalue = 0.0070721
  Group = -> [Br_element007]
  conduct = 2
  density = 1
  expand = 3
  formula = Br
  name = G4_Br
  specific = 4
FEATURE [App::DocumentObjectGroupPython] Kr_element001  label="Kr_element : 1"  # scripted group (container) (typed FeaturePython)
  n = 1
  ref = Kr_element
FEATURE [App::DocumentObjectGroupPython] G4_Kr  # scripted group (container) (typed FeaturePython)
  Dunit = g/cm3
  Dvalue = 0.00347832
  Group = -> [Kr_element001]
  conduct = 2
  density = 1
  expand = 3
  formula = Kr
  name = G4_Kr
  specific = 4
FEATURE [App::DocumentObjectGroupPython] Rb_element001  label="Rb_element : 1"  # scripted group (container) (typed FeaturePython)
  n = 1
  ref = Rb_element
FEATURE [App::DocumentObjectGroupPython] G4_Rb  # scripted group (container) (typed FeaturePython)
  Dunit = g/cm3
  Dvalue = 1.532
  Group = -> [Rb_element001]
  conduct = 2
  density = 1
  expand = 3
  formula = Rb
  name = G4_Rb
  specific = 4
FEATURE [App::DocumentObjectGroupPython] Sr_element001  label="Sr_element : 1"  # scripted group (container) (typed FeaturePython)
  n = 1
  ref = Sr_element
FEATURE [App::DocumentObjectGroupPython] G4_Sr  # scripted group (container) (typed FeaturePython)
  Dunit = g/cm3
  Dvalue = 2.54
  Group = -> [Sr_element001]
  conduct = 2
  density = 1
  expand = 3
  formula = Sr
  name = G4_Sr
  specific = 4
FEATURE [App::DocumentObjectGroupPython] Y_element001  label="Y_element : 1"  # scripted group (container) (typed FeaturePython)
  n = 1
  ref = Y_element
FEATURE [App::DocumentObjectGroupPython] G4_Y  # scripted group (container) (typed FeaturePython)
  Dunit = g/cm3
  Dvalue = 4.469
  Group = -> [Y_element001]
  conduct = 2
  density = 1
  expand = 3
  formula = Y
  name = G4_Y
  specific = 4
FEATURE [App::DocumentObjectGroupPython] Zr_element001  label="Zr_element : 1"  # scripted group (container) (typed FeaturePython)
  n = 1
  ref = Zr_element
FEATURE [App::DocumentObjectGroupPython] G4_Zr  # scripted group (container) (typed FeaturePython)
  Dunit = g/cm3
  Dvalue = 6.506
  Group = -> [Zr_element001]
  conduct = 2
  density = 1
  expand = 3
  formula = Zr
  name = G4_Zr
  specific = 4
FEATURE [App::DocumentObjectGroupPython] Nb_element001  label="Nb_element : 1"  # scripted group (container) (typed FeaturePython)
  n = 1
  ref = Nb_element
FEATURE [App::DocumentObjectGroupPython] G4_Nb  # scripted group (container) (typed FeaturePython)
  Dunit = g/cm3
  Dvalue = 8.57
  Group = -> [Nb_element001]
  conduct = 2
  density = 1
  expand = 3
  formula = Nb
  name = G4_Nb
  specific = 4
FEATURE [App::DocumentObjectGroupPython] Mo_element001  label="Mo_element : 1"  # scripted group (container) (typed FeaturePython)
  n = 1
  ref = Mo_element
FEATURE [App::DocumentObjectGroupPython] G4_Mo  # scripted group (container) (typed FeaturePython)
  Dunit = g/cm3
  Dvalue = 10.22
  Group = -> [Mo_element001]
  conduct = 2
  density = 1
  expand = 3
  formula = Mo
  name = G4_Mo
  specific = 4
FEATURE [App::DocumentObjectGroupPython] Tc_element001  label="Tc_element : 1"  # scripted group (container) (typed FeaturePython)
  n = 1
  ref = Tc_element
FEATURE [App::DocumentObjectGroupPython] G4_Tc  # scripted group (container) (typed FeaturePython)
  Dunit = g/cm3
  Dvalue = 11.5
  Group = -> [Tc_element001]
  conduct = 2
  density = 1
  expand = 3
  formula = Tc
  name = G4_Tc
  specific = 4
FEATURE [App::DocumentObjectGroupPython] Ru_element001  label="Ru_element : 1"  # scripted group (container) (typed FeaturePython)
  n = 1
  ref = Ru_element
FEATURE [App::DocumentObjectGroupPython] G4_Ru  # scripted group (container) (typed FeaturePython)
  Dunit = g/cm3
  Dvalue = 12.41
  Group = -> [Ru_element001]
  conduct = 2
  density = 1
  expand = 3
  formula = Ru
  name = G4_Ru
  specific = 4
FEATURE [App::DocumentObjectGroupPython] Rh_element001  label="Rh_element : 1"  # scripted group (container) (typed FeaturePython)
  n = 1
  ref = Rh_element
FEATURE [App::DocumentObjectGroupPython] G4_Rh  # scripted group (container) (typed FeaturePython)
  Dunit = g/cm3
  Dvalue = 12.41
  Group = -> [Rh_element001]
  conduct = 2
  density = 1
  expand = 3
  formula = Rh
  name = G4_Rh
  specific = 4
FEATURE [App::DocumentObjectGroupPython] Pd_element001  label="Pd_element : 1"  # scripted group (container) (typed FeaturePython)
  n = 1
  ref = Pd_element
FEATURE [App::DocumentObjectGroupPython] G4_Pd  # scripted group (container) (typed FeaturePython)
  Dunit = g/cm3
  Dvalue = 12.02
  Group = -> [Pd_element001]
  conduct = 2
  density = 1
  expand = 3
  formula = Pd
  name = G4_Pd
  specific = 4
FEATURE [App::DocumentObjectGroupPython] Ag_element006  label="Ag_element : 004"  # scripted group (container) (typed FeaturePython)
  n = 1
  ref = Ag_element
FEATURE [App::DocumentObjectGroupPython] G4_Ag  # scripted group (container) (typed FeaturePython)
  Dunit = g/cm3
  Dvalue = 10.5
  Group = -> [Ag_element006]
  conduct = 2
  density = 1
  expand = 3
  formula = Ag
  name = G4_Ag
  specific = 4
FEATURE [App::DocumentObjectGroupPython] Cd_element003  label="Cd_element : 003"  # scripted group (container) (typed FeaturePython)
  n = 1
  ref = Cd_element
FEATURE [App::DocumentObjectGroupPython] G4_Cd  # scripted group (container) (typed FeaturePython)
  Dunit = g/cm3
  Dvalue = 8.65
  Group = -> [Cd_element003]
  conduct = 2
  density = 1
  expand = 3
  formula = Cd
  name = G4_Cd
  specific = 4
FEATURE [App::DocumentObjectGroupPython] In_element001  label="In_element : 1"  # scripted group (container) (typed FeaturePython)
  n = 1
  ref = In_element
FEATURE [App::DocumentObjectGroupPython] G4_In  # scripted group (container) (typed FeaturePython)
  Dunit = g/cm3
  Dvalue = 7.31
  Group = -> [In_element001]
  conduct = 2
  density = 1
  expand = 3
  formula = In
  name = G4_In
  specific = 4
FEATURE [App::DocumentObjectGroupPython] Sn_element001  label="Sn_element : 1"  # scripted group (container) (typed FeaturePython)
  n = 1
  ref = Sn_element
FEATURE [App::DocumentObjectGroupPython] G4_Sn  # scripted group (container) (typed FeaturePython)
  Dunit = g/cm3
  Dvalue = 7.31
  Group = -> [Sn_element001]
  conduct = 2
  density = 1
  expand = 3
  formula = Sn
  name = G4_Sn
  specific = 4
FEATURE [App::DocumentObjectGroupPython] Sb_element001  label="Sb_element : 1"  # scripted group (container) (typed FeaturePython)
  n = 1
  ref = Sb_element
FEATURE [App::DocumentObjectGroupPython] G4_Sb  # scripted group (container) (typed FeaturePython)
  Dunit = g/cm3
  Dvalue = 6.691
  Group = -> [Sb_element001]
  conduct = 2
  density = 1
  expand = 3
  formula = Sb
  name = G4_Sb
  specific = 4
FEATURE [App::DocumentObjectGroupPython] Te_element002  label="Te_element : 002"  # scripted group (container) (typed FeaturePython)
  n = 1
  ref = Te_element
FEATURE [App::DocumentObjectGroupPython] G4_Te  # scripted group (container) (typed FeaturePython)
  Dunit = g/cm3
  Dvalue = 6.24
  Group = -> [Te_element002]
  conduct = 2
  density = 1
  expand = 3
  formula = Te
  name = G4_Te
  specific = 4
FEATURE [App::DocumentObjectGroupPython] I_element010  label="I_element : 006"  # scripted group (container) (typed FeaturePython)
  n = 1
  ref = I_element
FEATURE [App::DocumentObjectGroupPython] G4_I  # scripted group (container) (typed FeaturePython)
  Dunit = g/cm3
  Dvalue = 4.93
  Group = -> [I_element010]
  conduct = 2
  density = 1
  expand = 3
  formula = I
  name = G4_I
  specific = 4
FEATURE [App::DocumentObjectGroupPython] Xe_element001  label="Xe_element : 1"  # scripted group (container) (typed FeaturePython)
  n = 1
  ref = Xe_element
FEATURE [App::DocumentObjectGroupPython] G4_Xe  # scripted group (container) (typed FeaturePython)
  Dunit = g/cm3
  Dvalue = 0.00548536
  Group = -> [Xe_element001]
  conduct = 2
  density = 1
  expand = 3
  formula = Xe
  name = G4_Xe
  specific = 4
FEATURE [App::DocumentObjectGroupPython] Cs_element003  label="Cs_element : 003"  # scripted group (container) (typed FeaturePython)
  n = 1
  ref = Cs_element
FEATURE [App::DocumentObjectGroupPython] G4_Cs  # scripted group (container) (typed FeaturePython)
  Dunit = g/cm3
  Dvalue = 1.873
  Group = -> [Cs_element003]
  conduct = 2
  density = 1
  expand = 3
  formula = Cs
  name = G4_Cs
  specific = 4
FEATURE [App::DocumentObjectGroupPython] Ba_element003  label="Ba_element : 003"  # scripted group (container) (typed FeaturePython)
  n = 1
  ref = Ba_element
FEATURE [App::DocumentObjectGroupPython] G4_Ba  # scripted group (container) (typed FeaturePython)
  Dunit = g/cm3
  Dvalue = 3.5
  Group = -> [Ba_element003]
  conduct = 2
  density = 1
  expand = 3
  formula = Ba
  name = G4_Ba
  specific = 4
FEATURE [App::DocumentObjectGroupPython] La_element003  label="La_element : 003"  # scripted group (container) (typed FeaturePython)
  n = 1
  ref = La_element
FEATURE [App::DocumentObjectGroupPython] G4_La  # scripted group (container) (typed FeaturePython)
  Dunit = g/cm3
  Dvalue = 6.154
  Group = -> [La_element003]
  conduct = 2
  density = 1
  expand = 3
  formula = La
  name = G4_La
  specific = 4
FEATURE [App::DocumentObjectGroupPython] Ce_element002  label="Ce_element : 1"  # scripted group (container) (typed FeaturePython)
  n = 1
  ref = Ce_element
FEATURE [App::DocumentObjectGroupPython] G4_Ce  # scripted group (container) (typed FeaturePython)
  Dunit = g/cm3
  Dvalue = 6.657
  Group = -> [Ce_element002]
  conduct = 2
  density = 1
  expand = 3
  formula = Ce
  name = G4_Ce
  specific = 4
FEATURE [App::DocumentObjectGroupPython] Pr_element001  label="Pr_element : 1"  # scripted group (container) (typed FeaturePython)
  n = 1
  ref = Pr_element
FEATURE [App::DocumentObjectGroupPython] G4_Pr  # scripted group (container) (typed FeaturePython)
  Dunit = g/cm3
  Dvalue = 6.71
  Group = -> [Pr_element001]
  conduct = 2
  density = 1
  expand = 3
  formula = Pr
  name = G4_Pr
  specific = 4
FEATURE [App::DocumentObjectGroupPython] Nd_element001  label="Nd_element : 1"  # scripted group (container) (typed FeaturePython)
  n = 1
  ref = Nd_element
FEATURE [App::DocumentObjectGroupPython] G4_Nd  # scripted group (container) (typed FeaturePython)
  Dunit = g/cm3
  Dvalue = 6.9
  Group = -> [Nd_element001]
  conduct = 2
  density = 1
  expand = 3
  formula = Nd
  name = G4_Nd
  specific = 4
FEATURE [App::DocumentObjectGroupPython] Pm_element001  label="Pm_element : 1"  # scripted group (container) (typed FeaturePython)
  n = 1
  ref = Pm_element
FEATURE [App::DocumentObjectGroupPython] G4_Pm  # scripted group (container) (typed FeaturePython)
  Dunit = g/cm3
  Dvalue = 7.22
  Group = -> [Pm_element001]
  conduct = 2
  density = 1
  expand = 3
  formula = Pm
  name = G4_Pm
  specific = 4
FEATURE [App::DocumentObjectGroupPython] Sm_element001  label="Sm_element : 1"  # scripted group (container) (typed FeaturePython)
  n = 1
  ref = Sm_element
FEATURE [App::DocumentObjectGroupPython] G4_Sm  # scripted group (container) (typed FeaturePython)
  Dunit = g/cm3
  Dvalue = 7.46
  Group = -> [Sm_element001]
  conduct = 2
  density = 1
  expand = 3
  formula = Sm
  name = G4_Sm
  specific = 4
FEATURE [App::DocumentObjectGroupPython] Eu_element001  label="Eu_element : 1"  # scripted group (container) (typed FeaturePython)
  n = 1
  ref = Eu_element
FEATURE [App::DocumentObjectGroupPython] G4_Eu  # scripted group (container) (typed FeaturePython)
  Dunit = g/cm3
  Dvalue = 5.243
  Group = -> [Eu_element001]
  conduct = 2
  density = 1
  expand = 3
  formula = Eu
  name = G4_Eu
  specific = 4
FEATURE [App::DocumentObjectGroupPython] Gd_element002  label="Gd_element : 1"  # scripted group (container) (typed FeaturePython)
  n = 1
  ref = Gd_element
FEATURE [App::DocumentObjectGroupPython] G4_Gd  # scripted group (container) (typed FeaturePython)
  Dunit = g/cm3
  Dvalue = 7.9004
  Group = -> [Gd_element002]
  conduct = 2
  density = 1
  expand = 3
  formula = Gd
  name = G4_Gd
  specific = 4
FEATURE [App::DocumentObjectGroupPython] Tb_element001  label="Tb_element : 1"  # scripted group (container) (typed FeaturePython)
  n = 1
  ref = Tb_element
FEATURE [App::DocumentObjectGroupPython] G4_Tb  # scripted group (container) (typed FeaturePython)
  Dunit = g/cm3
  Dvalue = 8.229
  Group = -> [Tb_element001]
  conduct = 2
  density = 1
  expand = 3
  formula = Tb
  name = G4_Tb
  specific = 4
FEATURE [App::DocumentObjectGroupPython] Dy_element001  label="Dy_element : 1"  # scripted group (container) (typed FeaturePython)
  n = 1
  ref = Dy_element
FEATURE [App::DocumentObjectGroupPython] G4_Dy  # scripted group (container) (typed FeaturePython)
  Dunit = g/cm3
  Dvalue = 8.55
  Group = -> [Dy_element001]
  conduct = 2
  density = 1
  expand = 3
  formula = Dy
  name = G4_Dy
  specific = 4
FEATURE [App::DocumentObjectGroupPython] Ho_element001  label="Ho_element : 1"  # scripted group (container) (typed FeaturePython)
  n = 1
  ref = Ho_element
FEATURE [App::DocumentObjectGroupPython] G4_Ho  # scripted group (container) (typed FeaturePython)
  Dunit = g/cm3
  Dvalue = 8.795
  Group = -> [Ho_element001]
  conduct = 2
  density = 1
  expand = 3
  formula = Ho
  name = G4_Ho
  specific = 4
FEATURE [App::DocumentObjectGroupPython] Er_element001  label="Er_element : 1"  # scripted group (container) (typed FeaturePython)
  n = 1
  ref = Er_element
FEATURE [App::DocumentObjectGroupPython] G4_Er  # scripted group (container) (typed FeaturePython)
  Dunit = g/cm3
  Dvalue = 9.066
  Group = -> [Er_element001]
  conduct = 2
  density = 1
  expand = 3
  formula = Er
  name = G4_Er
  specific = 4
FEATURE [App::DocumentObjectGroupPython] Tm_element001  label="Tm_element : 1"  # scripted group (container) (typed FeaturePython)
  n = 1
  ref = Tm_element
FEATURE [App::DocumentObjectGroupPython] G4_Tm  # scripted group (container) (typed FeaturePython)
  Dunit = g/cm3
  Dvalue = 9.321
  Group = -> [Tm_element001]
  conduct = 2
  density = 1
  expand = 3
  formula = Tm
  name = G4_Tm
  specific = 4
FEATURE [App::DocumentObjectGroupPython] Yb_element001  label="Yb_element : 1"  # scripted group (container) (typed FeaturePython)
  n = 1
  ref = Yb_element
FEATURE [App::DocumentObjectGroupPython] G4_Yb  # scripted group (container) (typed FeaturePython)
  Dunit = g/cm3
  Dvalue = 6.73
  Group = -> [Yb_element001]
  conduct = 2
  density = 1
  expand = 3
  formula = Yb
  name = G4_Yb
  specific = 4
FEATURE [App::DocumentObjectGroupPython] Lu_element001  label="Lu_element : 1"  # scripted group (container) (typed FeaturePython)
  n = 1
  ref = Lu_element
FEATURE [App::DocumentObjectGroupPython] G4_Lu  # scripted group (container) (typed FeaturePython)
  Dunit = g/cm3
  Dvalue = 9.84
  Group = -> [Lu_element001]
  conduct = 2
  density = 1
  expand = 3
  formula = Lu
  name = G4_Lu
  specific = 4
FEATURE [App::DocumentObjectGroupPython] Hf_element001  label="Hf_element : 1"  # scripted group (container) (typed FeaturePython)
  n = 1
  ref = Hf_element
FEATURE [App::DocumentObjectGroupPython] G4_Hf  # scripted group (container) (typed FeaturePython)
  Dunit = g/cm3
  Dvalue = 13.31
  Group = -> [Hf_element001]
  conduct = 2
  density = 1
  expand = 3
  formula = Hf
  name = G4_Hf
  specific = 4
FEATURE [App::DocumentObjectGroupPython] Ta_element001  label="Ta_element : 1"  # scripted group (container) (typed FeaturePython)
  n = 1
  ref = Ta_element
FEATURE [App::DocumentObjectGroupPython] G4_Ta  # scripted group (container) (typed FeaturePython)
  Dunit = g/cm3
  Dvalue = 16.654
  Group = -> [Ta_element001]
  conduct = 2
  density = 1
  expand = 3
  formula = Ta
  name = G4_Ta
  specific = 4
FEATURE [App::DocumentObjectGroupPython] W_element004  label="W_element : 004"  # scripted group (container) (typed FeaturePython)
  n = 1
  ref = W_element
FEATURE [App::DocumentObjectGroupPython] G4_W  # scripted group (container) (typed FeaturePython)
  Dunit = g/cm3
  Dvalue = 19.3
  Group = -> [W_element004]
  conduct = 2
  density = 1
  expand = 3
  formula = W
  name = G4_W
  specific = 4
FEATURE [App::DocumentObjectGroupPython] Re_element001  label="Re_element : 1"  # scripted group (container) (typed FeaturePython)
  n = 1
  ref = Re_element
FEATURE [App::DocumentObjectGroupPython] G4_Re  # scripted group (container) (typed FeaturePython)
  Dunit = g/cm3
  Dvalue = 21.02
  Group = -> [Re_element001]
  conduct = 2
  density = 1
  expand = 3
  formula = Re
  name = G4_Re
  specific = 4
FEATURE [App::DocumentObjectGroupPython] Os_element001  label="Os_element : 1"  # scripted group (container) (typed FeaturePython)
  n = 1
  ref = Os_element
FEATURE [App::DocumentObjectGroupPython] G4_Os  # scripted group (container) (typed FeaturePython)
  Dunit = g/cm3
  Dvalue = 22.57
  Group = -> [Os_element001]
  conduct = 2
  density = 1
  expand = 3
  formula = Os
  name = G4_Os
  specific = 4
FEATURE [App::DocumentObjectGroupPython] Ir_element001  label="Ir_element : 1"  # scripted group (container) (typed FeaturePython)
  n = 1
  ref = Ir_element
FEATURE [App::DocumentObjectGroupPython] G4_Ir  # scripted group (container) (typed FeaturePython)
  Dunit = g/cm3
  Dvalue = 22.42
  Group = -> [Ir_element001]
  conduct = 2
  density = 1
  expand = 3
  formula = Ir
  name = G4_Ir
  specific = 4
FEATURE [App::DocumentObjectGroupPython] Pt_element001  label="Pt_element : 1"  # scripted group (container) (typed FeaturePython)
  n = 1
  ref = Pt_element
FEATURE [App::DocumentObjectGroupPython] G4_Pt  # scripted group (container) (typed FeaturePython)
  Dunit = g/cm3
  Dvalue = 21.45
  Group = -> [Pt_element001]
  conduct = 2
  density = 1
  expand = 3
  formula = Pt
  name = G4_Pt
  specific = 4
FEATURE [App::DocumentObjectGroupPython] Au_element001  label="Au_element : 1"  # scripted group (container) (typed FeaturePython)
  n = 1
  ref = Au_element
FEATURE [App::DocumentObjectGroupPython] G4_Au  # scripted group (container) (typed FeaturePython)
  Dunit = g/cm3
  Dvalue = 19.32
  Group = -> [Au_element001]
  conduct = 2
  density = 1
  expand = 3
  formula = Au
  name = G4_Au
  specific = 4
FEATURE [App::DocumentObjectGroupPython] Hg_element002  label="Hg_element : 002"  # scripted group (container) (typed FeaturePython)
  n = 1
  ref = Hg_element
FEATURE [App::DocumentObjectGroupPython] G4_Hg  # scripted group (container) (typed FeaturePython)
  Dunit = g/cm3
  Dvalue = 13.546
  Group = -> [Hg_element002]
  conduct = 2
  density = 1
  expand = 3
  formula = Hg
  name = G4_Hg
  specific = 4
FEATURE [App::DocumentObjectGroupPython] Tl_element002  label="Tl_element : 002"  # scripted group (container) (typed FeaturePython)
  n = 1
  ref = Tl_element
FEATURE [App::DocumentObjectGroupPython] G4_Tl  # scripted group (container) (typed FeaturePython)
  Dunit = g/cm3
  Dvalue = 11.72
  Group = -> [Tl_element002]
  conduct = 2
  density = 1
  expand = 3
  formula = Tl
  name = G4_Tl
  specific = 4
FEATURE [App::DocumentObjectGroupPython] Pb_element003  label="Pb_element : 1"  # scripted group (container) (typed FeaturePython)
  n = 1
  ref = Pb_element
FEATURE [App::DocumentObjectGroupPython] G4_Pb  # scripted group (container) (typed FeaturePython)
  Dunit = g/cm3
  Dvalue = 11.35
  Group = -> [Pb_element003]
  conduct = 2
  density = 1
  expand = 3
  formula = Pb
  name = G4_Pb
  specific = 4
FEATURE [App::DocumentObjectGroupPython] Bi_element002  label="Bi_element : 1"  # scripted group (container) (typed FeaturePython)
  n = 1
  ref = Bi_element
FEATURE [App::DocumentObjectGroupPython] G4_Bi  # scripted group (container) (typed FeaturePython)
  Dunit = g/cm3
  Dvalue = 9.747
  Group = -> [Bi_element002]
  conduct = 2
  density = 1
  expand = 3
  formula = Bi
  name = G4_Bi
  specific = 4
FEATURE [App::DocumentObjectGroupPython] Po_element001  label="Po_element : 1"  # scripted group (container) (typed FeaturePython)
  n = 1
  ref = Po_element
FEATURE [App::DocumentObjectGroupPython] G4_Po  # scripted group (container) (typed FeaturePython)
  Dunit = g/cm3
  Dvalue = 9.32
  Group = -> [Po_element001]
  conduct = 2
  density = 1
  expand = 3
  formula = Po
  name = G4_Po
  specific = 4
FEATURE [App::DocumentObjectGroupPython] At_element001  label="At_element : 1"  # scripted group (container) (typed FeaturePython)
  n = 1
  ref = At_element
FEATURE [App::DocumentObjectGroupPython] G4_At  # scripted group (container) (typed FeaturePython)
  Dunit = g/cm3
  Dvalue = 9.32
  Group = -> [At_element001]
  conduct = 2
  density = 1
  expand = 3
  formula = At
  name = G4_At
  specific = 4
FEATURE [App::DocumentObjectGroupPython] Rn_element001  label="Rn_element : 1"  # scripted group (container) (typed FeaturePython)
  n = 1
  ref = Rn_element
FEATURE [App::DocumentObjectGroupPython] G4_Rn  # scripted group (container) (typed FeaturePython)
  Dunit = g/cm3
  Dvalue = 0.00900662
  Group = -> [Rn_element001]
  conduct = 2
  density = 1
  expand = 3
  formula = Rn
  name = G4_Rn
  specific = 4
FEATURE [App::DocumentObjectGroupPython] Fr_element001  label="Fr_element : 1"  # scripted group (container) (typed FeaturePython)
  n = 1
  ref = Fr_element
FEATURE [App::DocumentObjectGroupPython] G4_Fr  # scripted group (container) (typed FeaturePython)
  Dunit = g/cm3
  Dvalue = 1
  Group = -> [Fr_element001]
  conduct = 2
  density = 1
  expand = 3
  formula = Fr
  name = G4_Fr
  specific = 4
FEATURE [App::DocumentObjectGroupPython] Ra_element001  label="Ra_element : 1"  # scripted group (container) (typed FeaturePython)
  n = 1
  ref = Ra_element
FEATURE [App::DocumentObjectGroupPython] G4_Ra  # scripted group (container) (typed FeaturePython)
  Dunit = g/cm3
  Dvalue = 5
  Group = -> [Ra_element001]
  conduct = 2
  density = 1
  expand = 3
  formula = Ra
  name = G4_Ra
  specific = 4
FEATURE [App::DocumentObjectGroupPython] Ac_element001  label="Ac_element : 1"  # scripted group (container) (typed FeaturePython)
  n = 1
  ref = Ac_element
FEATURE [App::DocumentObjectGroupPython] G4_Ac  # scripted group (container) (typed FeaturePython)
  Dunit = g/cm3
  Dvalue = 10.07
  Group = -> [Ac_element001]
  conduct = 2
  density = 1
  expand = 3
  formula = Ac
  name = G4_Ac
  specific = 4
FEATURE [App::DocumentObjectGroupPython] Th_element001  label="Th_element : 1"  # scripted group (container) (typed FeaturePython)
  n = 1
  ref = Th_element
FEATURE [App::DocumentObjectGroupPython] G4_Th  # scripted group (container) (typed FeaturePython)
  Dunit = g/cm3
  Dvalue = 11.72
  Group = -> [Th_element001]
  conduct = 2
  density = 1
  expand = 3
  formula = Th
  name = G4_Th
  specific = 4
FEATURE [App::DocumentObjectGroupPython] Pa_element001  label="Pa_element : 1"  # scripted group (container) (typed FeaturePython)
  n = 1
  ref = Pa_element
FEATURE [App::DocumentObjectGroupPython] G4_Pa  # scripted group (container) (typed FeaturePython)
  Dunit = g/cm3
  Dvalue = 15.37
  Group = -> [Pa_element001]
  conduct = 2
  density = 1
  expand = 3
  formula = Pa
  name = G4_Pa
  specific = 4
FEATURE [App::DocumentObjectGroupPython] U_element004  label="U_element : 004"  # scripted group (container) (typed FeaturePython)
  n = 1
  ref = U_element
FEATURE [App::DocumentObjectGroupPython] G4_U  # scripted group (container) (typed FeaturePython)
  Dunit = g/cm3
  Dvalue = 18.95
  Group = -> [U_element004]
  conduct = 2
  density = 1
  expand = 3
  formula = U
  name = G4_U
  specific = 4
FEATURE [App::DocumentObjectGroupPython] Np_element001  label="Np_element : 1"  # scripted group (container) (typed FeaturePython)
  n = 1
  ref = Np_element
FEATURE [App::DocumentObjectGroupPython] G4_Np  # scripted group (container) (typed FeaturePython)
  Dunit = g/cm3
  Dvalue = 20.25
  Group = -> [Np_element001]
  conduct = 2
  density = 1
  expand = 3
  formula = Np
  name = G4_Np
  specific = 4
FEATURE [App::DocumentObjectGroupPython] Pu_element002  label="Pu_element : 002"  # scripted group (container) (typed FeaturePython)
  n = 1
  ref = Pu_element
FEATURE [App::DocumentObjectGroupPython] G4_Pu  # scripted group (container) (typed FeaturePython)
  Dunit = g/cm3
  Dvalue = 19.84
  Group = -> [Pu_element002]
  conduct = 2
  density = 1
  expand = 3
  formula = Pu
  name = G4_Pu
  specific = 4
FEATURE [App::DocumentObjectGroupPython] Am_element001  label="Am_element : 1"  # scripted group (container) (typed FeaturePython)
  n = 1
  ref = Am_element
FEATURE [App::DocumentObjectGroupPython] G4_Am  # scripted group (container) (typed FeaturePython)
  Dunit = g/cm3
  Dvalue = 13.67
  Group = -> [Am_element001]
  conduct = 2
  density = 1
  expand = 3
  formula = Am
  name = G4_Am
  specific = 4
FEATURE [App::DocumentObjectGroupPython] Cm_element001  label="Cm_element : 1"  # scripted group (container) (typed FeaturePython)
  n = 1
  ref = Cm_element
FEATURE [App::DocumentObjectGroupPython] G4_Cm  # scripted group (container) (typed FeaturePython)
  Dunit = g/cm3
  Dvalue = 13.51
  Group = -> [Cm_element001]
  conduct = 2
  density = 1
  expand = 3
  formula = Cm
  name = G4_Cm
  specific = 4
FEATURE [App::DocumentObjectGroupPython] Bk_element001  label="Bk_element : 1"  # scripted group (container) (typed FeaturePython)
  n = 1
  ref = Bk_element
FEATURE [App::DocumentObjectGroupPython] G4_Bk  # scripted group (container) (typed FeaturePython)
  Dunit = g/cm3
  Dvalue = 14
  Group = -> [Bk_element001]
  conduct = 2
  density = 1
  expand = 3
  formula = Bk
  name = G4_Bk
  specific = 4
FEATURE [App::DocumentObjectGroupPython] Cf_element001  label="Cf_element : 1"  # scripted group (container) (typed FeaturePython)
  n = 1
  ref = Cf_element
FEATURE [App::DocumentObjectGroupPython] G4_Cf  # scripted group (container) (typed FeaturePython)
  Dunit = g/cm3
  Dvalue = 10
  Group = -> [Cf_element001]
  conduct = 2
  density = 1
  expand = 3
  formula = Cf
  name = G4_Cf
  specific = 4
FEATURE [App::DocumentObjectGroupPython] Element  # scripted group (container) (typed FeaturePython)
  Group = -> [G4_H,G4_He,G4_Li,G4_Be,G4_B,G4_C,G4_N,G4_O,G4_F,G4_Ne,G4_Na,G4_Mg,G4_Al,G4_Si,G4_P,G4_S,G4_Cl,G4_Ar,G4_K,G4_Ca,G4_Sc,G4_Ti,G4_V,G4_Cr,G4_Mn,G4_Fe,G4_Co,G4_Ni,G4_Cu,G4_Zn,G4_Ga,G4_Ge,G4_As,G4_Se,G4_Br,G4_Kr,G4_Rb,G4_Sr,G4_Y,G4_Zr,G4_Nb,G4_Mo,G4_Tc,G4_Ru,G4_Rh,G4_Pd,G4_Ag,G4_Cd,G4_In,G4_Sn,G4_Sb,G4_Te,G4_I,G4_Xe,G4_Cs,G4_Ba,G4_La,G4_Ce,G4_Pr,G4_Nd,G4_Pm,G4_Sm,G4_Eu,G4_Gd,G4_Tb,G4_Dy,G4_Ho,G4_Er,+30 more]
FEATURE [App::DocumentObjectGroupPython] H_element114  label="H_element : 063"  # scripted group (container) (typed FeaturePython)
  n = 2
  ref = H_element
FEATURE [App::DocumentObjectGroupPython] G4_lH2  # scripted group (container) (typed FeaturePython)
  Dunit = g/cm3
  Dvalue = 0.0708
  Group = -> [H_element114]
  conduct = 2
  density = 1
  expand = 3
  formula = G4_lH2
  name = G4_lH2
  specific = 4
FEATURE [App::DocumentObjectGroupPython] N_element049  label="N_element : 022"  # scripted group (container) (typed FeaturePython)
  n = 2
  ref = N_element
FEATURE [App::DocumentObjectGroupPython] G4_lN2  # scripted group (container) (typed FeaturePython)
  Dunit = g/cm3
  Dvalue = 0.807
  Group = -> [N_element049]
  conduct = 2
  density = 1
  expand = 3
  formula = G4_lN2
  name = G4_lN2
  specific = 4
FEATURE [App::DocumentObjectGroupPython] O_element106  label="O_element : 060"  # scripted group (container) (typed FeaturePython)
  n = 2
  ref = O_element
FEATURE [App::DocumentObjectGroupPython] G4_lO2  # scripted group (container) (typed FeaturePython)
  Dunit = g/cm3
  Dvalue = 1.141
  Group = -> [O_element106]
  conduct = 2
  density = 1
  expand = 3
  formula = G4_lO2
  name = G4_lO2
  specific = 4
FEATURE [App::DocumentObjectGroupPython] Ar  label="Ar : 1"  # scripted group (container) (typed FeaturePython)
  n = 1
  ref = Ar
FEATURE [App::DocumentObjectGroupPython] G4_lAr  # scripted group (container) (typed FeaturePython)
  Dunit = g/cm3
  Dvalue = 1.396
  Group = -> [Ar]
  conduct = 2
  density = 1
  expand = 3
  formula = G4_lAr
  name = G4_lAr
  specific = 4
FEATURE [App::DocumentObjectGroupPython] Br  label="Br : 1"  # scripted group (container) (typed FeaturePython)
  n = 1
  ref = Br
FEATURE [App::DocumentObjectGroupPython] G4_lBr  # scripted group (container) (typed FeaturePython)
  Dunit = g/cm3
  Dvalue = 3.1028
  Group = -> [Br]
  conduct = 2
  density = 1
  expand = 3
  formula = G4_lBr
  name = G4_lBr
  specific = 4
FEATURE [App::DocumentObjectGroupPython] Kr  label="Kr : 1"  # scripted group (container) (typed FeaturePython)
  n = 1
  ref = Kr
FEATURE [App::DocumentObjectGroupPython] G4_lKr  # scripted group (container) (typed FeaturePython)
  Dunit = g/cm3
  Dvalue = 2.418
  Group = -> [Kr]
  conduct = 2
  density = 1
  expand = 3
  formula = G4_lKr
  name = G4_lKr
  specific = 4
FEATURE [App::DocumentObjectGroupPython] Xe  label="Xe : 1"  # scripted group (container) (typed FeaturePython)
  n = 1
  ref = Xe
FEATURE [App::DocumentObjectGroupPython] G4_lXe  # scripted group (container) (typed FeaturePython)
  Dunit = g/cm3
  Dvalue = 2.953
  Group = -> [Xe]
  conduct = 2
  density = 1
  expand = 3
  formula = G4_lXe
  name = G4_lXe
  specific = 4
FEATURE [App::DocumentObjectGroupPython] O_element107  label="O_element : 061"  # scripted group (container) (typed FeaturePython)
  n = 4
  ref = O_element
FEATURE [App::DocumentObjectGroupPython] Pb_element004  label="Pb_element : 002"  # scripted group (container) (typed FeaturePython)
  n = 1
  ref = Pb_element
FEATURE [App::DocumentObjectGroupPython] W_element005  label="W_element : 005"  # scripted group (container) (typed FeaturePython)
  n = 1
  ref = W_element
FEATURE [App::DocumentObjectGroupPython] G4_PbWO4  # scripted group (container) (typed FeaturePython)
  Dunit = g/cm3
  Dvalue = 8.28
  Group = -> [O_element107,Pb_element004,W_element005]
  conduct = 2
  density = 1
  expand = 3
  formula = G4_PbWO4
  name = G4_PbWO4
  specific = 4
FEATURE [App::DocumentObjectGroupPython] alactic  label="alactic : 1"  # scripted group (container) (typed FeaturePython)
  n = 1
  ref = alactic
FEATURE [App::DocumentObjectGroupPython] G4_Galactic  # scripted group (container) (typed FeaturePython)
  Dunit = g/cm3
  Dvalue = 0
  Group = -> [alactic]
  conduct = 2
  density = 1
  expand = 3
  formula = G4_Galactic
  name = G4_Galactic
  specific = 4
FEATURE [App::DocumentObjectGroupPython] RAPHITE_POROUS  label="RAPHITE_POROUS : 1"  # scripted group (container) (typed FeaturePython)
  n = 1
  ref = RAPHITE_POROUS
FEATURE [App::DocumentObjectGroupPython] G4_GRAPHITE_POROUS  # scripted group (container) (typed FeaturePython)
  Dunit = g/cm3
  Dvalue = 1.7
  Group = -> [RAPHITE_POROUS]
  conduct = 2
  density = 1
  expand = 3
  formula = G4_GRAPHITE_POROUS
  name = G4_GRAPHITE_POROUS
  specific = 4
FEATURE [App::DocumentObjectGroupPython] H_element115  label="H_element : 0.150"  # scripted group (container) (typed FeaturePython)
  n = 0.080538
FEATURE [App::DocumentObjectGroupPython] C_element125  label="C_element : 0.600"  # scripted group (container) (typed FeaturePython)
  n = 0.599848
FEATURE [App::DocumentObjectGroupPython] O_element108  label="O_element : 0.320"  # scripted group (container) (typed FeaturePython)
  n = 0.319614
FEATURE [App::DocumentObjectGroupPython] G4_LUCITE  # scripted group (container) (typed FeaturePython)
  Dunit = g/cm3
  Dvalue = 1.19
  Group = -> [H_element115,C_element125,O_element108]
  conduct = 2
  density = 1
  expand = 3
  formula = G4_LUCITE
  name = G4_LUCITE
  specific = 4
FEATURE [App::DocumentObjectGroupPython] Cu_element002  label="Cu_element : 62"  # scripted group (container) (typed FeaturePython)
  n = 62
  ref = Cu_element
FEATURE [App::DocumentObjectGroupPython] Zn_element002  label="Zn_element : 35"  # scripted group (container) (typed FeaturePython)
  n = 35
  ref = Zn_element
FEATURE [App::DocumentObjectGroupPython] Pb_element005  label="Pb_element : 3"  # scripted group (container) (typed FeaturePython)
  n = 3
  ref = Pb_element
FEATURE [App::DocumentObjectGroupPython] G4_BRASS  # scripted group (container) (typed FeaturePython)
  Dunit = g/cm3
  Dvalue = 8.52
  Group = -> [Cu_element002,Zn_element002,Pb_element005]
  conduct = 2
  density = 1
  expand = 3
  formula = G4_BRASS
  name = G4_BRASS
  specific = 4
FEATURE [App::DocumentObjectGroupPython] Cu_element003  label="Cu_element : 89"  # scripted group (container) (typed FeaturePython)
  n = 89
  ref = Cu_element
FEATURE [App::DocumentObjectGroupPython] Zn_element003  label="Zn_element : 9"  # scripted group (container) (typed FeaturePython)
  n = 9
  ref = Zn_element
FEATURE [App::DocumentObjectGroupPython] Pb_element006  label="Pb_element : 2"  # scripted group (container) (typed FeaturePython)
  n = 2
  ref = Pb_element
FEATURE [App::DocumentObjectGroupPython] G4_BRONZE  # scripted group (container) (typed FeaturePython)
  Dunit = g/cm3
  Dvalue = 8.82
  Group = -> [Cu_element003,Zn_element003,Pb_element006]
  conduct = 2
  density = 1
  expand = 3
  formula = G4_BRONZE
  name = G4_BRONZE
  specific = 4
FEATURE [App::DocumentObjectGroupPython] Fe_element008  label="Fe_element : 74"  # scripted group (container) (typed FeaturePython)
  n = 74
  ref = Fe_element
FEATURE [App::DocumentObjectGroupPython] Cr_element002  label="Cr_element : 18"  # scripted group (container) (typed FeaturePython)
  n = 18
  ref = Cr_element
FEATURE [App::DocumentObjectGroupPython] Ni_element002  label="Ni_element : 8"  # scripted group (container) (typed FeaturePython)
  n = 8
  ref = Ni_element
FEATURE [App::DocumentObjectGroupPython] G4_STAINLESS_STEEL  label="G4_STAINLESS-STEEL"  # scripted group (container) (typed FeaturePython)
  Dunit = g/cm3
  Dvalue = 8
  Group = -> [Fe_element008,Cr_element002,Ni_element002]
  conduct = 2
  density = 1
  expand = 3
  formula = G4_STAINLESS-STEEL
  name = G4_STAINLESS-STEEL
  specific = 4
FEATURE [App::DocumentObjectGroupPython] H_element116  label="H_element : 064"  # scripted group (container) (typed FeaturePython)
  n = 18
  ref = H_element
FEATURE [App::DocumentObjectGroupPython] C_element126  label="C_element : 071"  # scripted group (container) (typed FeaturePython)
  n = 12
  ref = C_element
FEATURE [App::DocumentObjectGroupPython] O_element109  label="O_element : 062"  # scripted group (container) (typed FeaturePython)
  n = 7
  ref = O_element
FEATURE [App::DocumentObjectGroupPython] G4_CR39  # scripted group (container) (typed FeaturePython)
  Dunit = g/cm3
  Dvalue = 1.32
  Group = -> [H_element116,C_element126,O_element109]
  conduct = 2
  density = 1
  expand = 3
  formula = G4_CR39
  name = G4_CR39
  specific = 4
FEATURE [App::DocumentObjectGroupPython] H_element117  label="H_element : 38"  # scripted group (container) (typed FeaturePython)
  n = 38
  ref = H_element
FEATURE [App::DocumentObjectGroupPython] C_element127  label="C_element : 072"  # scripted group (container) (typed FeaturePython)
  n = 18
  ref = C_element
FEATURE [App::DocumentObjectGroupPython] O_element110  label="O_element : 063"  # scripted group (container) (typed FeaturePython)
  n = 1
  ref = O_element
FEATURE [App::DocumentObjectGroupPython] G4_OCTADECANOL  # scripted group (container) (typed FeaturePython)
  Dunit = g/cm3
  Dvalue = 0.812
  Group = -> [H_element117,C_element127,O_element110]
  conduct = 2
  density = 1
  expand = 3
  formula = G4_OCTADECANOL
  name = G4_OCTADECANOL
  specific = 4
FEATURE [App::DocumentObjectGroupPython] HEP  # scripted group (container) (typed FeaturePython)
  Group = -> [G4_lH2,G4_lN2,G4_lO2,G4_lAr,G4_lBr,G4_lKr,G4_lXe,G4_PbWO4,G4_Galactic,G4_GRAPHITE_POROUS,G4_LUCITE,G4_BRASS,G4_BRONZE,G4_STAINLESS_STEEL,G4_CR39,G4_OCTADECANOL]
FEATURE [App::DocumentObjectGroupPython] C_element128  label="C_element : 073"  # scripted group (container) (typed FeaturePython)
  n = 14
  ref = C_element
FEATURE [App::DocumentObjectGroupPython] H_element118  label="H_element : 065"  # scripted group (container) (typed FeaturePython)
  n = 10
  ref = H_element
FEATURE [App::DocumentObjectGroupPython] O_element111  label="O_element : 064"  # scripted group (container) (typed FeaturePython)
  n = 2
  ref = O_element
FEATURE [App::DocumentObjectGroupPython] N_element050  label="N_element : 023"  # scripted group (container) (typed FeaturePython)
  n = 2
  ref = N_element
FEATURE [App::DocumentObjectGroupPython] G4_KEVLAR  # scripted group (container) (typed FeaturePython)
  Dunit = g/cm3
  Dvalue = 1.44
  Group = -> [C_element128,H_element118,O_element111,N_element050]
  conduct = 2
  density = 1
  expand = 3
  formula = G4_KEVLAR
  name = G4_KEVLAR
  specific = 4
FEATURE [App::DocumentObjectGroupPython] C_element129  label="C_element : 074"  # scripted group (container) (typed FeaturePython)
  n = 10
  ref = C_element
FEATURE [App::DocumentObjectGroupPython] H_element119  label="H_element : 066"  # scripted group (container) (typed FeaturePython)
  n = 8
  ref = H_element
FEATURE [App::DocumentObjectGroupPython] O_element112  label="O_element : 065"  # scripted group (container) (typed FeaturePython)
  n = 4
  ref = O_element
FEATURE [App::DocumentObjectGroupPython] G4_DACRON  # scripted group (container) (typed FeaturePython)
  Dunit = g/cm3
  Dvalue = 1.4
  Group = -> [C_element129,H_element119,O_element112]
  conduct = 2
  density = 1
  expand = 3
  formula = G4_DACRON
  name = G4_DACRON
  specific = 4
FEATURE [App::DocumentObjectGroupPython] C_element130  label="C_element : 075"  # scripted group (container) (typed FeaturePython)
  n = 4
  ref = C_element
FEATURE [App::DocumentObjectGroupPython] H_element120  label="H_element : 067"  # scripted group (container) (typed FeaturePython)
  n = 5
  ref = H_element
FEATURE [App::DocumentObjectGroupPython] Cl_element030  label="Cl_element : 016"  # scripted group (container) (typed FeaturePython)
  n = 1
  ref = Cl_element
FEATURE [App::DocumentObjectGroupPython] G4_NEOPRENE  # scripted group (container) (typed FeaturePython)
  Dunit = g/cm3
  Dvalue = 1.23
  Group = -> [C_element130,H_element120,Cl_element030]
  conduct = 2
  density = 1
  expand = 3
  formula = G4_NEOPRENE
  name = G4_NEOPRENE
  specific = 4
FEATURE [App::DocumentObjectGroupPython] Space  # scripted group (container) (typed FeaturePython)
  Group = -> [G4_KEVLAR,G4_DACRON,G4_NEOPRENE]
FEATURE [App::DocumentObjectGroupPython] H_element121  label="H_element : 068"  # scripted group (container) (typed FeaturePython)
  n = 5
  ref = H_element
FEATURE [App::DocumentObjectGroupPython] C_element131  label="C_element : 076"  # scripted group (container) (typed FeaturePython)
  n = 4
  ref = C_element
FEATURE [App::DocumentObjectGroupPython] N_element051  label="N_element : 3"  # scripted group (container) (typed FeaturePython)
  n = 3
  ref = N_element
FEATURE [App::DocumentObjectGroupPython] O_element113  label="O_element : 066"  # scripted group (container) (typed FeaturePython)
  n = 1
  ref = O_element
FEATURE [App::DocumentObjectGroupPython] G4_CYTOSINE  # scripted group (container) (typed FeaturePython)
  Dunit = g/cm3
  Dvalue = 1.55
  Group = -> [H_element121,C_element131,N_element051,O_element113]
  conduct = 2
  density = 1
  expand = 3
  formula = G4_CYTOSINE
  name = G4_CYTOSINE
  specific = 4
FEATURE [App::DocumentObjectGroupPython] H_element122  label="H_element : 069"  # scripted group (container) (typed FeaturePython)
  n = 6
  ref = H_element
FEATURE [App::DocumentObjectGroupPython] C_element132  label="C_element : 077"  # scripted group (container) (typed FeaturePython)
  n = 5
  ref = C_element
FEATURE [App::DocumentObjectGroupPython] N_element052  label="N_element : 024"  # scripted group (container) (typed FeaturePython)
  n = 2
  ref = N_element
FEATURE [App::DocumentObjectGroupPython] O_element114  label="O_element : 067"  # scripted group (container) (typed FeaturePython)
  n = 2
  ref = O_element
FEATURE [App::DocumentObjectGroupPython] G4_THYMINE  # scripted group (container) (typed FeaturePython)
  Dunit = g/cm3
  Dvalue = 1.23
  Group = -> [H_element122,C_element132,N_element052,O_element114]
  conduct = 2
  density = 1
  expand = 3
  formula = G4_THYMINE
  name = G4_THYMINE
  specific = 4
FEATURE [App::DocumentObjectGroupPython] H_element123  label="H_element : 070"  # scripted group (container) (typed FeaturePython)
  n = 4
  ref = H_element
FEATURE [App::DocumentObjectGroupPython] C_element133  label="C_element : 078"  # scripted group (container) (typed FeaturePython)
  n = 4
  ref = C_element
FEATURE [App::DocumentObjectGroupPython] N_element053  label="N_element : 025"  # scripted group (container) (typed FeaturePython)
  n = 2
  ref = N_element
FEATURE [App::DocumentObjectGroupPython] O_element115  label="O_element : 068"  # scripted group (container) (typed FeaturePython)
  n = 2
  ref = O_element
FEATURE [App::DocumentObjectGroupPython] G4_URACIL  # scripted group (container) (typed FeaturePython)
  Dunit = g/cm3
  Dvalue = 1.32
  Group = -> [H_element123,C_element133,N_element053,O_element115]
  conduct = 2
  density = 1
  expand = 3
  formula = G4_URACIL
  name = G4_URACIL
  specific = 4
FEATURE [App::DocumentObjectGroupPython] H_element124  label="H_element : 071"  # scripted group (container) (typed FeaturePython)
  n = 4
  ref = H_element
FEATURE [App::DocumentObjectGroupPython] C_element134  label="C_element : 079"  # scripted group (container) (typed FeaturePython)
  n = 5
  ref = C_element
FEATURE [App::DocumentObjectGroupPython] N_element054  label="N_element : 026"  # scripted group (container) (typed FeaturePython)
  n = 5
  ref = N_element
FEATURE [App::DocumentObjectGroupPython] G4_DNA_ADENINE  # scripted group (container) (typed FeaturePython)
  Dunit = g/cm3
  Dvalue = 1
  Group = -> [H_element124,C_element134,N_element054]
  conduct = 2
  density = 1
  expand = 3
  formula = G4_DNA_ADENINE
  name = G4_DNA_ADENINE
  specific = 4
FEATURE [App::DocumentObjectGroupPython] H_element125  label="H_element : 072"  # scripted group (container) (typed FeaturePython)
  n = 4
  ref = H_element
FEATURE [App::DocumentObjectGroupPython] C_element135  label="C_element : 080"  # scripted group (container) (typed FeaturePython)
  n = 5
  ref = C_element
FEATURE [App::DocumentObjectGroupPython] N_element055  label="N_element : 027"  # scripted group (container) (typed FeaturePython)
  n = 5
  ref = N_element
FEATURE [App::DocumentObjectGroupPython] O_element116  label="O_element : 069"  # scripted group (container) (typed FeaturePython)
  n = 1
  ref = O_element
FEATURE [App::DocumentObjectGroupPython] G4_DNA_GUANINE  # scripted group (container) (typed FeaturePython)
  Dunit = g/cm3
  Dvalue = 1
  Group = -> [H_element125,C_element135,N_element055,O_element116]
  conduct = 2
  density = 1
  expand = 3
  formula = G4_DNA_GUANINE
  name = G4_DNA_GUANINE
  specific = 4
FEATURE [App::DocumentObjectGroupPython] H_element126  label="H_element : 073"  # scripted group (container) (typed FeaturePython)
  n = 4
  ref = H_element
FEATURE [App::DocumentObjectGroupPython] C_element136  label="C_element : 081"  # scripted group (container) (typed FeaturePython)
  n = 4
  ref = C_element
FEATURE [App::DocumentObjectGroupPython] N_element056  label="N_element : 028"  # scripted group (container) (typed FeaturePython)
  n = 3
  ref = N_element
FEATURE [App::DocumentObjectGroupPython] O_element117  label="O_element : 070"  # scripted group (container) (typed FeaturePython)
  n = 1
  ref = O_element
FEATURE [App::DocumentObjectGroupPython] G4_DNA_CYTOSINE  # scripted group (container) (typed FeaturePython)
  Dunit = g/cm3
  Dvalue = 1
  Group = -> [H_element126,C_element136,N_element056,O_element117]
  conduct = 2
  density = 1
  expand = 3
  formula = G4_DNA_CYTOSINE
  name = G4_DNA_CYTOSINE
  specific = 4
FEATURE [App::DocumentObjectGroupPython] H_element127  label="H_element : 074"  # scripted group (container) (typed FeaturePython)
  n = 5
  ref = H_element
FEATURE [App::DocumentObjectGroupPython] C_element137  label="C_element : 082"  # scripted group (container) (typed FeaturePython)
  n = 5
  ref = C_element
FEATURE [App::DocumentObjectGroupPython] N_element057  label="N_element : 029"  # scripted group (container) (typed FeaturePython)
  n = 2
  ref = N_element
FEATURE [App::DocumentObjectGroupPython] O_element118  label="O_element : 071"  # scripted group (container) (typed FeaturePython)
  n = 2
  ref = O_element
FEATURE [App::DocumentObjectGroupPython] G4_DNA_THYMINE  # scripted group (container) (typed FeaturePython)
  Dunit = g/cm3
  Dvalue = 1
  Group = -> [H_element127,C_element137,N_element057,O_element118]
  conduct = 2
  density = 1
  expand = 3
  formula = G4_DNA_THYMINE
  name = G4_DNA_THYMINE
  specific = 4
FEATURE [App::DocumentObjectGroupPython] H_element128  label="H_element : 075"  # scripted group (container) (typed FeaturePython)
  n = 3
  ref = H_element
FEATURE [App::DocumentObjectGroupPython] C_element138  label="C_element : 083"  # scripted group (container) (typed FeaturePython)
  n = 4
  ref = C_element
FEATURE [App::DocumentObjectGroupPython] N_element058  label="N_element : 030"  # scripted group (container) (typed FeaturePython)
  n = 2
  ref = N_element
FEATURE [App::DocumentObjectGroupPython] O_element119  label="O_element : 072"  # scripted group (container) (typed FeaturePython)
  n = 2
  ref = O_element
FEATURE [App::DocumentObjectGroupPython] G4_DNA_URACIL  # scripted group (container) (typed FeaturePython)
  Dunit = g/cm3
  Dvalue = 1
  Group = -> [H_element128,C_element138,N_element058,O_element119]
  conduct = 2
  density = 1
  expand = 3
  formula = G4_DNA_URACIL
  name = G4_DNA_URACIL
  specific = 4
FEATURE [App::DocumentObjectGroupPython] H_element129  label="H_element : 076"  # scripted group (container) (typed FeaturePython)
  n = 10
  ref = H_element
FEATURE [App::DocumentObjectGroupPython] C_element139  label="C_element : 084"  # scripted group (container) (typed FeaturePython)
  n = 10
  ref = C_element
FEATURE [App::DocumentObjectGroupPython] N_element059  label="N_element : 031"  # scripted group (container) (typed FeaturePython)
  n = 5
  ref = N_element
FEATURE [App::DocumentObjectGroupPython] O_element120  label="O_element : 073"  # scripted group (container) (typed FeaturePython)
  n = 4
  ref = O_element
FEATURE [App::DocumentObjectGroupPython] G4_DNA_ADENOSINE  # scripted group (container) (typed FeaturePython)
  Dunit = g/cm3
  Dvalue = 1
  Group = -> [H_element129,C_element139,N_element059,O_element120]
  conduct = 2
  density = 1
  expand = 3
  formula = G4_DNA_ADENOSINE
  name = G4_DNA_ADENOSINE
  specific = 4
FEATURE [App::DocumentObjectGroupPython] H_element130  label="H_element : 077"  # scripted group (container) (typed FeaturePython)
  n = 10
  ref = H_element
FEATURE [App::DocumentObjectGroupPython] C_element140  label="C_element : 085"  # scripted group (container) (typed FeaturePython)
  n = 10
  ref = C_element
FEATURE [App::DocumentObjectGroupPython] N_element060  label="N_element : 032"  # scripted group (container) (typed FeaturePython)
  n = 5
  ref = N_element
FEATURE [App::DocumentObjectGroupPython] O_element121  label="O_element : 074"  # scripted group (container) (typed FeaturePython)
  n = 5
  ref = O_element
FEATURE [App::DocumentObjectGroupPython] G4_DNA_GUANOSINE  # scripted group (container) (typed FeaturePython)
  Dunit = g/cm3
  Dvalue = 1
  Group = -> [H_element130,C_element140,N_element060,O_element121]
  conduct = 2
  density = 1
  expand = 3
  formula = G4_DNA_GUANOSINE
  name = G4_DNA_GUANOSINE
  specific = 4
FEATURE [App::DocumentObjectGroupPython] H_element131  label="H_element : 078"  # scripted group (container) (typed FeaturePython)
  n = 10
  ref = H_element
FEATURE [App::DocumentObjectGroupPython] C_element141  label="C_element : 086"  # scripted group (container) (typed FeaturePython)
  n = 9
  ref = C_element
FEATURE [App::DocumentObjectGroupPython] N_element061  label="N_element : 033"  # scripted group (container) (typed FeaturePython)
  n = 3
  ref = N_element
FEATURE [App::DocumentObjectGroupPython] O_element122  label="O_element : 075"  # scripted group (container) (typed FeaturePython)
  n = 5
  ref = O_element
FEATURE [App::DocumentObjectGroupPython] G4_DNA_CYTIDINE  # scripted group (container) (typed FeaturePython)
  Dunit = g/cm3
  Dvalue = 1
  Group = -> [H_element131,C_element141,N_element061,O_element122]
  conduct = 2
  density = 1
  expand = 3
  formula = G4_DNA_CYTIDINE
  name = G4_DNA_CYTIDINE
  specific = 4
FEATURE [App::DocumentObjectGroupPython] H_element132  label="H_element : 079"  # scripted group (container) (typed FeaturePython)
  n = 9
  ref = H_element
FEATURE [App::DocumentObjectGroupPython] C_element142  label="C_element : 087"  # scripted group (container) (typed FeaturePython)
  n = 9
  ref = C_element
FEATURE [App::DocumentObjectGroupPython] N_element062  label="N_element : 034"  # scripted group (container) (typed FeaturePython)
  n = 2
  ref = N_element
FEATURE [App::DocumentObjectGroupPython] O_element123  label="O_element : 076"  # scripted group (container) (typed FeaturePython)
  n = 6
  ref = O_element
FEATURE [App::DocumentObjectGroupPython] G4_DNA_URIDINE  # scripted group (container) (typed FeaturePython)
  Dunit = g/cm3
  Dvalue = 1
  Group = -> [H_element132,C_element142,N_element062,O_element123]
  conduct = 2
  density = 1
  expand = 3
  formula = G4_DNA_URIDINE
  name = G4_DNA_URIDINE
  specific = 4
FEATURE [App::DocumentObjectGroupPython] H_element133  label="H_element : 080"  # scripted group (container) (typed FeaturePython)
  n = 11
  ref = H_element
FEATURE [App::DocumentObjectGroupPython] C_element143  label="C_element : 088"  # scripted group (container) (typed FeaturePython)
  n = 10
  ref = C_element
FEATURE [App::DocumentObjectGroupPython] N_element063  label="N_element : 035"  # scripted group (container) (typed FeaturePython)
  n = 2
  ref = N_element
FEATURE [App::DocumentObjectGroupPython] O_element124  label="O_element : 077"  # scripted group (container) (typed FeaturePython)
  n = 6
  ref = O_element
FEATURE [App::DocumentObjectGroupPython] G4_DNA_METHYLURIDINE  # scripted group (container) (typed FeaturePython)
  Dunit = g/cm3
  Dvalue = 1
  Group = -> [H_element133,C_element143,N_element063,O_element124]
  conduct = 2
  density = 1
  expand = 3
  formula = G4_DNA_METHYLURIDINE
  name = G4_DNA_METHYLURIDINE
  specific = 4
FEATURE [App::DocumentObjectGroupPython] P_element014  label="P_element : 003"  # scripted group (container) (typed FeaturePython)
  n = 1
  ref = P_element
FEATURE [App::DocumentObjectGroupPython] O_element125  label="O_element : 078"  # scripted group (container) (typed FeaturePython)
  n = 3
  ref = O_element
FEATURE [App::DocumentObjectGroupPython] G4_DNA_MONOPHOSPHATE  # scripted group (container) (typed FeaturePython)
  Dunit = g/cm3
  Dvalue = 1
  Group = -> [P_element014,O_element125]
  conduct = 2
  density = 1
  expand = 3
  formula = G4_DNA_MONOPHOSPHATE
  name = G4_DNA_MONOPHOSPHATE
  specific = 4
FEATURE [App::DocumentObjectGroupPython] H_element134  label="H_element : 081"  # scripted group (container) (typed FeaturePython)
  n = 10
  ref = H_element
FEATURE [App::DocumentObjectGroupPython] C_element144  label="C_element : 089"  # scripted group (container) (typed FeaturePython)
  n = 10
  ref = C_element
FEATURE [App::DocumentObjectGroupPython] N_element064  label="N_element : 036"  # scripted group (container) (typed FeaturePython)
  n = 5
  ref = N_element
FEATURE [App::DocumentObjectGroupPython] O_element126  label="O_element : 079"  # scripted group (container) (typed FeaturePython)
  n = 7
  ref = O_element
FEATURE [App::DocumentObjectGroupPython] P_element015  label="P_element : 004"  # scripted group (container) (typed FeaturePython)
  n = 1
  ref = P_element
FEATURE [App::DocumentObjectGroupPython] G4_DNA_A  # scripted group (container) (typed FeaturePython)
  Dunit = g/cm3
  Dvalue = 1
  Group = -> [H_element134,C_element144,N_element064,O_element126,P_element015]
  conduct = 2
  density = 1
  expand = 3
  formula = G4_DNA_A
  name = G4_DNA_A
  specific = 4
FEATURE [App::DocumentObjectGroupPython] H_element135  label="H_element : 082"  # scripted group (container) (typed FeaturePython)
  n = 10
  ref = H_element
FEATURE [App::DocumentObjectGroupPython] C_element145  label="C_element : 090"  # scripted group (container) (typed FeaturePython)
  n = 10
  ref = C_element
FEATURE [App::DocumentObjectGroupPython] N_element065  label="N_element : 037"  # scripted group (container) (typed FeaturePython)
  n = 5
  ref = N_element
FEATURE [App::DocumentObjectGroupPython] O_element127  label="O_element : 8"  # scripted group (container) (typed FeaturePython)
  n = 8
  ref = O_element
FEATURE [App::DocumentObjectGroupPython] P_element016  label="P_element : 005"  # scripted group (container) (typed FeaturePython)
  n = 1
  ref = P_element
FEATURE [App::DocumentObjectGroupPython] G4_DNA_G  # scripted group (container) (typed FeaturePython)
  Dunit = g/cm3
  Dvalue = 1
  Group = -> [H_element135,C_element145,N_element065,O_element127,P_element016]
  conduct = 2
  density = 1
  expand = 3
  formula = G4_DNA_G
  name = G4_DNA_G
  specific = 4
FEATURE [App::DocumentObjectGroupPython] H_element136  label="H_element : 083"  # scripted group (container) (typed FeaturePython)
  n = 10
  ref = H_element
FEATURE [App::DocumentObjectGroupPython] C_element146  label="C_element : 091"  # scripted group (container) (typed FeaturePython)
  n = 9
  ref = C_element
FEATURE [App::DocumentObjectGroupPython] N_element066  label="N_element : 038"  # scripted group (container) (typed FeaturePython)
  n = 3
  ref = N_element
FEATURE [App::DocumentObjectGroupPython] O_element128  label="O_element : 080"  # scripted group (container) (typed FeaturePython)
  n = 8
  ref = O_element
FEATURE [App::DocumentObjectGroupPython] P_element017  label="P_element : 006"  # scripted group (container) (typed FeaturePython)
  n = 1
  ref = P_element
FEATURE [App::DocumentObjectGroupPython] G4_DNA_C  # scripted group (container) (typed FeaturePython)
  Dunit = g/cm3
  Dvalue = 1
  Group = -> [H_element136,C_element146,N_element066,O_element128,P_element017]
  conduct = 2
  density = 1
  expand = 3
  formula = G4_DNA_C
  name = G4_DNA_C
  specific = 4
FEATURE [App::DocumentObjectGroupPython] H_element137  label="H_element : 084"  # scripted group (container) (typed FeaturePython)
  n = 9
  ref = H_element
FEATURE [App::DocumentObjectGroupPython] C_element147  label="C_element : 092"  # scripted group (container) (typed FeaturePython)
  n = 9
  ref = C_element
FEATURE [App::DocumentObjectGroupPython] N_element067  label="N_element : 039"  # scripted group (container) (typed FeaturePython)
  n = 2
  ref = N_element
FEATURE [App::DocumentObjectGroupPython] O_element129  label="O_element : 9"  # scripted group (container) (typed FeaturePython)
  n = 9
  ref = O_element
FEATURE [App::DocumentObjectGroupPython] P_element018  label="P_element : 007"  # scripted group (container) (typed FeaturePython)
  n = 1
  ref = P_element
FEATURE [App::DocumentObjectGroupPython] G4_DNA_U  # scripted group (container) (typed FeaturePython)
  Dunit = g/cm3
  Dvalue = 1
  Group = -> [H_element137,C_element147,N_element067,O_element129,P_element018]
  conduct = 2
  density = 1
  expand = 3
  formula = G4_DNA_U
  name = G4_DNA_U
  specific = 4
FEATURE [App::DocumentObjectGroupPython] H_element138  label="H_element : 085"  # scripted group (container) (typed FeaturePython)
  n = 11
  ref = H_element
FEATURE [App::DocumentObjectGroupPython] C_element148  label="C_element : 093"  # scripted group (container) (typed FeaturePython)
  n = 10
  ref = C_element
FEATURE [App::DocumentObjectGroupPython] N_element068  label="N_element : 040"  # scripted group (container) (typed FeaturePython)
  n = 2
  ref = N_element
FEATURE [App::DocumentObjectGroupPython] O_element130  label="O_element : 081"  # scripted group (container) (typed FeaturePython)
  n = 9
  ref = O_element
FEATURE [App::DocumentObjectGroupPython] P_element019  label="P_element : 008"  # scripted group (container) (typed FeaturePython)
  n = 1
  ref = P_element
FEATURE [App::DocumentObjectGroupPython] G4_DNA_MU  # scripted group (container) (typed FeaturePython)
  Dunit = g/cm3
  Dvalue = 1
  Group = -> [H_element138,C_element148,N_element068,O_element130,P_element019]
  conduct = 2
  density = 1
  expand = 3
  formula = G4_DNA_MU
  name = G4_DNA_MU
  specific = 4
FEATURE [App::DocumentObjectGroupPython] BioChemical  # scripted group (container) (typed FeaturePython)
  Group = -> [G4_CYTOSINE,G4_THYMINE,G4_URACIL,G4_DNA_ADENINE,G4_DNA_GUANINE,G4_DNA_CYTOSINE,G4_DNA_THYMINE,G4_DNA_URACIL,G4_DNA_ADENOSINE,G4_DNA_GUANOSINE,G4_DNA_CYTIDINE,G4_DNA_URIDINE,G4_DNA_METHYLURIDINE,G4_DNA_MONOPHOSPHATE,G4_DNA_A,G4_DNA_G,G4_DNA_C,G4_DNA_U,G4_DNA_MU]
FEATURE [App::DocumentObjectGroupPython] G4Materials  # scripted group (container) (typed FeaturePython)
  Group = -> [NIST,Element,HEP,Space,BioChemical]
  version = 1
FEATURE [App::DocumentObjectGroupPython] Geant4  # scripted group (container) (typed FeaturePython)
  Group = -> [G4Isotopes,G4Elements,G4Materials]
FEATURE [App::DocumentObjectGroupPython] Materials  # scripted group (container) (typed FeaturePython)
  Group = -> [Geant4]
FEATURE [Part::FeaturePython] GDMLBox_WorldBox  # WARN: FeaturePython — macro-defined, semantics opaque (R4)
  lunit = 2
  material = 5
  x = 600
  y = 600
  z = 600
FEATURE [Part::FeaturePython] GDMLSphere_Sphere  # WARN: FeaturePython — macro-defined, semantics opaque (R4)
  Placement = pos=(20,0,0) rot=(0,0,1;0rad)
  aunit = 0
  deltaphi = 2.02
  deltatheta = 2.02
  lunit = 2
  material = 18
  rmax = 20
  rmin = 10
  startphi = 0
  starttheta = 0
FEATURE [Part::FeaturePython] GDMLTorus_Torus  # WARN: FeaturePython — macro-defined, semantics opaque (R4)
  aunit = deg
  deltaphi = 360
  lunit = 2
  material = 5
  rmax = 5
  rmin = 0
  rtor = 10
  startphi = 10
FEATURE [Part::MultiFuse] Fusion
  Shapes = -> [GDMLSphere_Sphere,GDMLTorus_Torus]
  material = 18
FEATURE [Part::FeaturePython] Array  # Draft array (typed FeaturePython)
  Angle = 360
  ArrayType = 0
  Axis = (0,0,1)
  Base = -> Fusion
  Center = (0,0,0)
  Fuse = false
  IntervalAxis = (0,0,0)
  IntervalX = (100,0,0)
  IntervalY = (0,100,0)
  IntervalZ = (0,0,100)
  NumberCircles = 3
  NumberPolar = 5
  NumberX = 2
  NumberY = 2
  NumberZ = 1
  Placement = pos=(-76.5,-45,0) rot=(0,0,1;0rad)
  RadialDistance = 50
  Symmetry = 1
  TangentialDistance = 25
FEATURE [Part::FeaturePython] Clone  label="Array001"  # Draft clone (typed FeaturePython)
  AttacherType = Attacher::AttachEngine3D
  Fuse = false
  Objects = -> [Array]
  Placement = pos=(-76.5,-45,0) rot=(0,0,1;0rad)
  Scale = (2.5,1,1)
  material = 18
FEATURE [App::Part] Part
  Group = -> [Clone]
  Origin = -> Origin001
FEATURE [App::Part] worldVOL
  Group = -> [GDMLBox_WorldBox,Part]
  Origin = -> Origin
